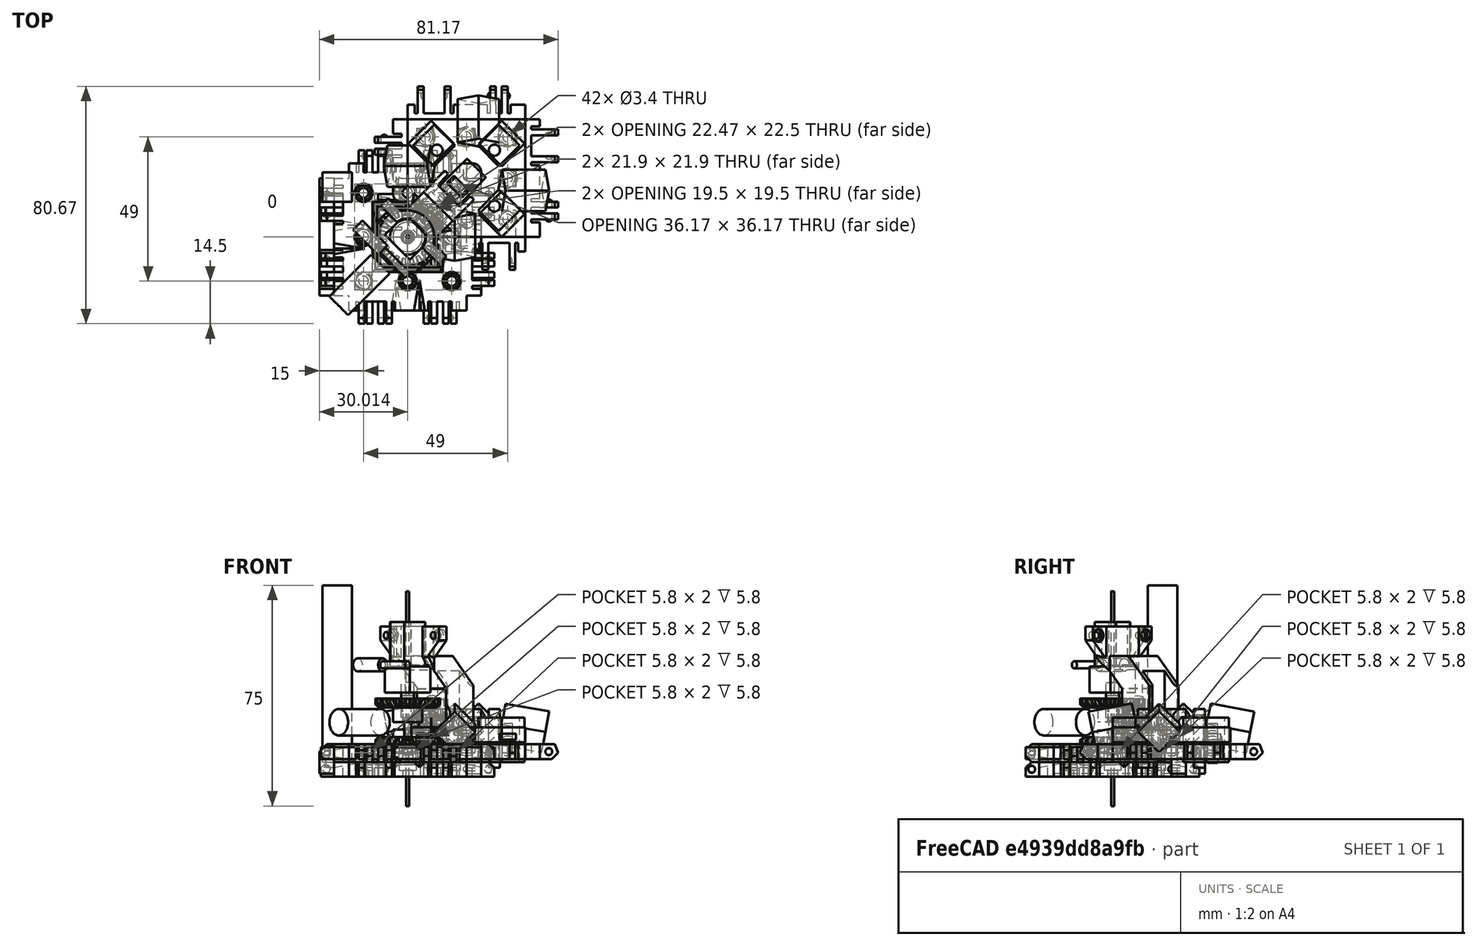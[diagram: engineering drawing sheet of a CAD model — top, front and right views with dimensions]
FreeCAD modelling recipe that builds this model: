
FCSTD DOCUMENT  (FreeCAD 0.18R16146 (Git))
Label: Robot 0.3
License: All rights reserved
LicenseURL: http://en.wikipedia.org/wiki/All_rights_reserved
objects: Part::Box×364, Part::Cut×148, Part::Sphere×107, Part::MultiFuse×99, Part::Cylinder×77, Part::Fuse×47, Part::Feature×40, Part::Chamfer×28, Drawing::FeatureViewAnnotation×12, Part::MultiCommon×5, Part::Fillet×5, App::DocumentObjectGroup×4, Part::FeaturePython×3, Part::Cone×2, Part::Mirroring×2, Drawing::FeaturePage×2
note: 927 computed .brp shape members not serialized (recipe doc carries the construction recipe); baked Part::Feature solids carry a one-line shape summary decoded from their .brp

FEATURE [Part::Box] Box  label="Cube"
  AttacherType = Attacher::AttachEngine3D
  Height = 5
  Length = 40
  Placement = pos=(-20,-20,-2) rot=(0,0,1;0rad)
  Width = 40
FEATURE [Part::Sphere] Sphere003  label="Mag Hole 3"
  Angle1 = -90
  Angle2 = 90
  Angle3 = 360
  AttacherType = Attacher::AttachEngine3D
  Placement = pos=(-15,15,1.7) rot=(0,0,1;0rad)
  Radius = 2.83
FEATURE [Part::Sphere] Sphere005  label="Mag Hole 2"
  Angle1 = -90
  Angle2 = 90
  Angle3 = 360
  AttacherType = Attacher::AttachEngine3D
  Placement = pos=(15,0,1.7) rot=(0,0,1;0rad)
  Radius = 2.825
FEATURE [Part::Sphere] Sphere  label="Mag Hole"
  Angle1 = -90
  Angle2 = 90
  Angle3 = 360
  AttacherType = Attacher::AttachEngine3D
  Placement = pos=(-15,-15,1.7) rot=(0,0,1;0rad)
  Radius = 2.83
FEATURE [Part::MultiFuse] Fusion004  label="Ball Holes"
  Shapes = -> [Sphere,Sphere005,Sphere003]
FEATURE [Part::Cut] Cut003
  Base = -> Box
  Tool = -> Fusion004
FEATURE [Part::Box] Box001  label="Cube001"
  AttacherType = Attacher::AttachEngine3D
  Height = 7
  Length = 5
  Placement = pos=(-5,0,-2) rot=(0,0,1;0rad)
  Width = 40
FEATURE [Part::Box] Box002  label="Cube002"
  AttacherType = Attacher::AttachEngine3D
  Height = 7
  Length = 10
  Placement = pos=(-15,6,-2) rot=(0,0,1;0rad)
  Width = 2
FEATURE [Part::Box] Box003  label="Cube003"
  AttacherType = Attacher::AttachEngine3D
  Height = 7
  Length = 10
  Placement = pos=(-15,10,-2) rot=(0,0,1;0rad)
  Width = 2
FEATURE [Part::Box] Box004  label="Cube004"
  AttacherType = Attacher::AttachEngine3D
  Height = 7
  Length = 10
  Placement = pos=(-15,25.4,-2) rot=(0,0,1;0rad)
  Width = 2
FEATURE [Part::Box] Box005  label="Cube005"
  AttacherType = Attacher::AttachEngine3D
  Height = 7
  Length = 10
  Placement = pos=(-15,34.6,-2) rot=(0,0,1;0rad)
  Width = 2
FEATURE [Part::Sphere] Sphere008
  Angle1 = -90
  Angle2 = 90
  Angle3 = 360
  AttacherType = Attacher::AttachEngine3D
  Placement = pos=(-7.5,6.5,0.5) rot=(0,0,1;0rad)
  Radius = 1.25
FEATURE [Part::Box] Box006  label="Chamfer Cube"
  AttacherType = Attacher::AttachEngine3D
  Height = 10
  Length = 13
  Placement = pos=(-11.69,0,-1.19) rot=(0,-1,0;0.785398rad)
  Width = 40
FEATURE [Part::Sphere] Sphere009
  Angle1 = -90
  Angle2 = 90
  Angle3 = 360
  AttacherType = Attacher::AttachEngine3D
  Placement = pos=(-7.5,11.5,0.5) rot=(0,0,1;0rad)
  Radius = 1.25
FEATURE [Part::Sphere] Sphere010
  Angle1 = -90
  Angle2 = 90
  Angle3 = 360
  AttacherType = Attacher::AttachEngine3D
  Placement = pos=(-7.5,28,0.5) rot=(0,0,1;0rad)
  Radius = 1.5
FEATURE [Part::Sphere] Sphere011
  Angle1 = -90
  Angle2 = 90
  Angle3 = 360
  AttacherType = Attacher::AttachEngine3D
  Placement = pos=(-7.5,34,0.5) rot=(0,0,1;0rad)
  Radius = 1.5
FEATURE [Part::Box] Box007  label="Cube007"
  AttacherType = Attacher::AttachEngine3D
  Height = 7
  Length = 4
  Placement = pos=(-6,5,-2) rot=(0,0,1;0rad)
  Width = 1
FEATURE [Part::Box] Box008  label="Cube008"
  AttacherType = Attacher::AttachEngine3D
  Height = 7
  Length = 4
  Placement = pos=(-6,8,-2) rot=(0,0,1;0rad)
  Width = 2
FEATURE [Part::Box] Box009  label="Cube009"
  AttacherType = Attacher::AttachEngine3D
  Height = 7
  Length = 4
  Placement = pos=(-6,12,-2) rot=(0,0,1;0rad)
  Width = 1
FEATURE [Part::Box] Box010  label="Cube010"
  AttacherType = Attacher::AttachEngine3D
  Height = 7
  Length = 4
  Placement = pos=(-6,24.4,-2) rot=(0,0,1;0rad)
  Width = 1
FEATURE [Part::Box] Box011  label="Cube011"
  AttacherType = Attacher::AttachEngine3D
  Height = 7
  Length = 4
  Placement = pos=(-6,36.6,-2) rot=(0,0,1;0rad)
  Width = 1
FEATURE [Part::Box] Box012  label="Cube012"
  AttacherType = Attacher::AttachEngine3D
  Height = 7
  Length = 4
  Placement = pos=(-6,27.4,-2) rot=(0,0,1;0rad)
  Width = 7.2
FEATURE [Part::MultiFuse] Fusion003  label="Extra Holes for Clips"
  Shapes = -> [Box012,Box009,Box011,Box008,Box010,Box007]
FEATURE [Part::Box] Box013  label="Re-level Edge Clip Block"
  AttacherType = Attacher::AttachEngine3D
  Height = 10
  Length = 20
  Placement = pos=(-19,-2,3) rot=(0,0,1;0rad)
  Width = 44
FEATURE [Part::Box] Box014  label="Cube014"
  AttacherType = Attacher::AttachEngine3D
  Height = 7
  Length = 10
  Placement = pos=(-10,34.6,0) rot=(0,0,1;0rad)
  Width = 2
FEATURE [Part::Box] Box015  label="Cube015"
  AttacherType = Attacher::AttachEngine3D
  Height = 7
  Length = 5
  Width = 40
FEATURE [Part::Box] Box016  label="Cube016"
  AttacherType = Attacher::AttachEngine3D
  Height = 7
  Length = 10
  Placement = pos=(-10,25.4,0) rot=(0,0,1;0rad)
  Width = 2
FEATURE [Part::Box] Box017  label="Cube017"
  AttacherType = Attacher::AttachEngine3D
  Height = 7
  Length = 10
  Placement = pos=(-10,10,0) rot=(0,0,1;0rad)
  Width = 2
FEATURE [Part::Box] Box018  label="Cube018"
  AttacherType = Attacher::AttachEngine3D
  Height = 7
  Length = 10
  Placement = pos=(-10,6,0) rot=(0,0,1;0rad)
  Width = 2
FEATURE [Part::Sphere] Sphere012
  Angle1 = -90
  Angle2 = 90
  Angle3 = 360
  AttacherType = Attacher::AttachEngine3D
  Placement = pos=(-3,6.5,2.5) rot=(0,0,1;0rad)
  Radius = 1.25
FEATURE [Part::Box] Box019  label="Cube019"
  AttacherType = Attacher::AttachEngine3D
  Height = 10
  Length = 13
  Placement = pos=(-10.19,0,-1.19) rot=(0,-1,0;0.785398rad)
  Width = 40
FEATURE [Part::Sphere] Sphere013
  Angle1 = -90
  Angle2 = 90
  Angle3 = 360
  AttacherType = Attacher::AttachEngine3D
  Placement = pos=(-3,11.5,2.5) rot=(0,0,1;0rad)
  Radius = 1.25
FEATURE [Part::Sphere] Sphere014
  Angle1 = -90
  Angle2 = 90
  Angle3 = 360
  AttacherType = Attacher::AttachEngine3D
  Placement = pos=(-3,28,2.5) rot=(0,0,1;0rad)
  Radius = 1.5
FEATURE [Part::Sphere] Sphere015
  Angle1 = -90
  Angle2 = 90
  Angle3 = 360
  AttacherType = Attacher::AttachEngine3D
  Placement = pos=(-3,34,2.5) rot=(0,0,1;0rad)
  Radius = 1.5
FEATURE [Part::MultiFuse] Fusion005
  Shapes = -> [Box015,Box018,Box017,Box016,Box014]
FEATURE [Part::Cut] Cut005
  Base = -> Fusion005
  Tool = -> Box019
FEATURE [Part::MultiFuse] Fusion006
  Shapes = -> [Sphere012,Sphere013,Cut005]
FEATURE [Part::MultiFuse] Fusion007
  Shapes = -> [Sphere015,Sphere014]
FEATURE [Part::Cut] Cut006
  Base = -> Fusion006
  Tool = -> Fusion007
FEATURE [Part::Chamfer] Chamfer002
  Base = -> Cut006
  Edges = 4 edges r=4: [Edge31,Edge37,Edge43,Edge46]
FEATURE [Part::Box] Box020  label="Cube020"
  AttacherType = Attacher::AttachEngine3D
  Height = 7
  Length = 4
  Placement = pos=(-1,5,0) rot=(0,0,1;0rad)
  Width = 1
FEATURE [Part::Box] Box021  label="Cube021"
  AttacherType = Attacher::AttachEngine3D
  Height = 7
  Length = 4
  Placement = pos=(-1,8,0) rot=(0,0,1;0rad)
  Width = 2
FEATURE [Part::Box] Box022  label="Cube022"
  AttacherType = Attacher::AttachEngine3D
  Height = 7
  Length = 4
  Placement = pos=(-1,12,0) rot=(0,0,1;0rad)
  Width = 1
FEATURE [Part::Box] Box023  label="Cube023"
  AttacherType = Attacher::AttachEngine3D
  Height = 7
  Length = 4
  Placement = pos=(-1,24.4,0) rot=(0,0,1;0rad)
  Width = 1
FEATURE [Part::Box] Box024  label="Cube024"
  AttacherType = Attacher::AttachEngine3D
  Height = 7
  Length = 4
  Placement = pos=(-1,36.6,0) rot=(0,0,1;0rad)
  Width = 1
FEATURE [Part::Box] Box025  label="Cube025"
  AttacherType = Attacher::AttachEngine3D
  Height = 7
  Length = 4
  Placement = pos=(-1,27.4,0) rot=(0,0,1;0rad)
  Width = 7.2
FEATURE [Part::MultiFuse] Fusion008
  Shapes = -> [Box025,Box022,Box024,Box021,Box023,Box020]
FEATURE [Part::Cut] Cut007
  Base = -> Chamfer002
  Placement = pos=(-5,40,3) rot=(1,0,0;3.14159rad)
  Tool = -> Fusion008
FEATURE [Part::Box] Box026  label="Cube026"
  AttacherType = Attacher::AttachEngine3D
  Height = 10
  Length = 12
  Placement = pos=(-11,-2,-12) rot=(0,0,1;0rad)
  Width = 44
FEATURE [Part::Cut] Cut008
  Base = -> Cut007
  Placement = pos=(40,0,0) rot=(0,0,1;1.5708rad)
  Tool = -> Box026
FEATURE [Part::Box] Box027  label="Cube027"
  AttacherType = Attacher::AttachEngine3D
  Height = 7
  Length = 4
  Placement = pos=(-1,12,0) rot=(0,0,1;0rad)
  Width = 1
FEATURE [Part::Box] Box028  label="Cube028"
  AttacherType = Attacher::AttachEngine3D
  Height = 10
  Length = 13
  Placement = pos=(-10.19,0,-1.19) rot=(0,-1,0;0.785398rad)
  Width = 40
FEATURE [Part::Box] Box029  label="Cube029"
  AttacherType = Attacher::AttachEngine3D
  Height = 7
  Length = 4
  Placement = pos=(-1,27.4,0) rot=(0,0,1;0rad)
  Width = 7.2
FEATURE [Part::Box] Box030  label="Cube030"
  AttacherType = Attacher::AttachEngine3D
  Height = 7
  Length = 4
  Placement = pos=(-1,5,0) rot=(0,0,1;0rad)
  Width = 1
FEATURE [Part::Box] Box031  label="Cube031"
  AttacherType = Attacher::AttachEngine3D
  Height = 7
  Length = 10
  Placement = pos=(-10,6,0) rot=(0,0,1;0rad)
  Width = 2
FEATURE [Part::Box] Box032  label="Cube032"
  AttacherType = Attacher::AttachEngine3D
  Height = 10
  Length = 12
  Placement = pos=(-11,-2,-12) rot=(0,0,1;0rad)
  Width = 44
FEATURE [Part::Sphere] Sphere016
  Angle1 = -90
  Angle2 = 90
  Angle3 = 360
  AttacherType = Attacher::AttachEngine3D
  Placement = pos=(-3,6.5,2.5) rot=(0,0,1;0rad)
  Radius = 1.25
FEATURE [Part::Box] Box033  label="Cube033"
  AttacherType = Attacher::AttachEngine3D
  Height = 7
  Length = 10
  Placement = pos=(-10,25.4,0) rot=(0,0,1;0rad)
  Width = 2
FEATURE [Part::Box] Box034  label="Cube034"
  AttacherType = Attacher::AttachEngine3D
  Height = 7
  Length = 10
  Placement = pos=(-10,10,0) rot=(0,0,1;0rad)
  Width = 2
FEATURE [Part::Sphere] Sphere017
  Angle1 = -90
  Angle2 = 90
  Angle3 = 360
  AttacherType = Attacher::AttachEngine3D
  Placement = pos=(-3,28,2.5) rot=(0,0,1;0rad)
  Radius = 1.5
FEATURE [Part::Sphere] Sphere018
  Angle1 = -90
  Angle2 = 90
  Angle3 = 360
  AttacherType = Attacher::AttachEngine3D
  Placement = pos=(-3,11.5,2.5) rot=(0,0,1;0rad)
  Radius = 1.25
FEATURE [Part::Box] Box035  label="Cube035"
  AttacherType = Attacher::AttachEngine3D
  Height = 7
  Length = 4
  Placement = pos=(-1,36.6,0) rot=(0,0,1;0rad)
  Width = 1
FEATURE [Part::Sphere] Sphere019
  Angle1 = -90
  Angle2 = 90
  Angle3 = 360
  AttacherType = Attacher::AttachEngine3D
  Placement = pos=(-3,34,2.5) rot=(0,0,1;0rad)
  Radius = 1.5
FEATURE [Part::MultiFuse] Fusion011
  Shapes = -> [Sphere019,Sphere017]
FEATURE [Part::Box] Box036  label="Cube036"
  AttacherType = Attacher::AttachEngine3D
  Height = 7
  Length = 4
  Placement = pos=(-1,8,0) rot=(0,0,1;0rad)
  Width = 2
FEATURE [Part::Box] Box037  label="Cube037"
  AttacherType = Attacher::AttachEngine3D
  Height = 7
  Length = 10
  Placement = pos=(-10,34.6,0) rot=(0,0,1;0rad)
  Width = 2
FEATURE [Part::Box] Box038  label="Cube038"
  AttacherType = Attacher::AttachEngine3D
  Height = 7
  Length = 4
  Placement = pos=(-1,24.4,0) rot=(0,0,1;0rad)
  Width = 1
FEATURE [Part::MultiFuse] Fusion009
  Shapes = -> [Box029,Box027,Box035,Box036,Box038,Box030]
FEATURE [Part::Box] Box039  label="Cube039"
  AttacherType = Attacher::AttachEngine3D
  Height = 7
  Length = 5
  Width = 40
FEATURE [Part::MultiFuse] Fusion012
  Shapes = -> [Box039,Box031,Box034,Box033,Box037]
FEATURE [Part::Cut] Cut011
  Base = -> Fusion012
  Tool = -> Box028
FEATURE [Part::MultiFuse] Fusion010
  Shapes = -> [Sphere016,Sphere018,Cut011]
FEATURE [Part::Cut] Cut012
  Base = -> Fusion010
  Tool = -> Fusion011
FEATURE [Part::Chamfer] Chamfer003
  Base = -> Cut012
  Edges = 4 edges r=4: [Edge31,Edge37,Edge43,Edge46]
FEATURE [Part::Cut] Cut010
  Base = -> Chamfer003
  Placement = pos=(-5,40,3) rot=(1,0,0;3.14159rad)
  Tool = -> Fusion009
FEATURE [Part::Cut] Cut009
  Base = -> Cut010
  Placement = pos=(40,40,0) rot=(0,0,1;3.14159rad)
  Tool = -> Box032
FEATURE [Part::Sphere] Sphere020
  Angle1 = -90
  Angle2 = 90
  Angle3 = 360
  AttacherType = Attacher::AttachEngine3D
  Placement = pos=(-3,11.5,2.5) rot=(0,0,1;0rad)
  Radius = 1.25
FEATURE [Part::Box] Box040  label="Cube040"
  AttacherType = Attacher::AttachEngine3D
  Height = 7
  Length = 10
  Placement = pos=(-10,6,0) rot=(0,0,1;0rad)
  Width = 2
FEATURE [Part::Box] Box041  label="Cube041"
  AttacherType = Attacher::AttachEngine3D
  Height = 7
  Length = 4
  Placement = pos=(-1,8,0) rot=(0,0,1;0rad)
  Width = 2
FEATURE [Part::Box] Box042  label="Cube042"
  AttacherType = Attacher::AttachEngine3D
  Height = 7
  Length = 10
  Placement = pos=(-10,10,0) rot=(0,0,1;0rad)
  Width = 2
FEATURE [Part::Box] Box043  label="Cube043"
  AttacherType = Attacher::AttachEngine3D
  Height = 10
  Length = 12
  Placement = pos=(-11,-2,-12) rot=(0,0,1;0rad)
  Width = 44
FEATURE [Part::Box] Box044  label="Cube044"
  AttacherType = Attacher::AttachEngine3D
  Height = 7
  Length = 4
  Placement = pos=(-1,5,0) rot=(0,0,1;0rad)
  Width = 1
FEATURE [Part::Sphere] Sphere021
  Angle1 = -90
  Angle2 = 90
  Angle3 = 360
  AttacherType = Attacher::AttachEngine3D
  Placement = pos=(-3,28,2.5) rot=(0,0,1;0rad)
  Radius = 1.5
FEATURE [Part::Sphere] Sphere022
  Angle1 = -90
  Angle2 = 90
  Angle3 = 360
  AttacherType = Attacher::AttachEngine3D
  Placement = pos=(-3,6.5,2.5) rot=(0,0,1;0rad)
  Radius = 1.25
FEATURE [Part::Sphere] Sphere023
  Angle1 = -90
  Angle2 = 90
  Angle3 = 360
  AttacherType = Attacher::AttachEngine3D
  Placement = pos=(-3,34,2.5) rot=(0,0,1;0rad)
  Radius = 1.5
FEATURE [Part::Box] Box045  label="Cube045"
  AttacherType = Attacher::AttachEngine3D
  Height = 7
  Length = 4
  Placement = pos=(-1,12,0) rot=(0,0,1;0rad)
  Width = 1
FEATURE [Part::Box] Box046  label="Cube046"
  AttacherType = Attacher::AttachEngine3D
  Height = 7
  Length = 5
  Width = 40
FEATURE [Part::Box] Box047  label="Cube047"
  AttacherType = Attacher::AttachEngine3D
  Height = 7
  Length = 4
  Placement = pos=(-1,36.6,0) rot=(0,0,1;0rad)
  Width = 1
FEATURE [Part::Box] Box048  label="Cube048"
  AttacherType = Attacher::AttachEngine3D
  Height = 7
  Length = 4
  Placement = pos=(-1,24.4,0) rot=(0,0,1;0rad)
  Width = 1
FEATURE [Part::Box] Box049  label="Cube049"
  AttacherType = Attacher::AttachEngine3D
  Height = 7
  Length = 10
  Placement = pos=(-10,25.4,0) rot=(0,0,1;0rad)
  Width = 2
FEATURE [Part::Box] Box050  label="Cube050"
  AttacherType = Attacher::AttachEngine3D
  Height = 10
  Length = 13
  Placement = pos=(-10.19,0,-1.19) rot=(0,-1,0;0.785398rad)
  Width = 40
FEATURE [Part::Box] Box051  label="Cube051"
  AttacherType = Attacher::AttachEngine3D
  Height = 7
  Length = 10
  Placement = pos=(-10,34.6,0) rot=(0,0,1;0rad)
  Width = 2
FEATURE [Part::MultiFuse] Fusion015
  Shapes = -> [Box046,Box040,Box042,Box049,Box051]
FEATURE [Part::Cut] Cut013
  Base = -> Fusion015
  Tool = -> Box050
FEATURE [Part::MultiFuse] Fusion013
  Shapes = -> [Sphere022,Sphere020,Cut013]
FEATURE [Part::MultiFuse] Fusion016
  Shapes = -> [Sphere023,Sphere021]
FEATURE [Part::Cut] Cut014
  Base = -> Fusion013
  Tool = -> Fusion016
FEATURE [Part::Chamfer] Chamfer004
  Base = -> Cut014
  Edges = 4 edges r=4: [Edge31,Edge37,Edge43,Edge46]
FEATURE [Part::Box] Box052  label="Cube052"
  AttacherType = Attacher::AttachEngine3D
  Height = 7
  Length = 4
  Placement = pos=(-1,27.4,0) rot=(0,0,1;0rad)
  Width = 7.2
FEATURE [Part::MultiFuse] Fusion014
  Shapes = -> [Box052,Box045,Box047,Box041,Box048,Box044]
FEATURE [Part::Cut] Cut016
  Base = -> Chamfer004
  Placement = pos=(-5,40,3) rot=(1,0,0;3.14159rad)
  Tool = -> Fusion014
FEATURE [Part::Cut] Cut015
  Base = -> Cut016
  Placement = pos=(0,40,0) rot=(0,0,-1;1.5708rad)
  Tool = -> Box043
FEATURE [Part::Box] Box054  label="Cube054"
  AttacherType = Attacher::AttachEngine3D
  Height = 15
  Length = 10
  Placement = pos=(9,2,-3) rot=(0,0,1;0.785398rad)
  Width = 10
FEATURE [Part::Box] Box055  label="Cube055"
  AttacherType = Attacher::AttachEngine3D
  Height = 15
  Length = 10
  Placement = pos=(31,24,-3) rot=(0,0,1;0.785398rad)
  Width = 10
FEATURE [Part::Box] Box056  label="Cube056"
  AttacherType = Attacher::AttachEngine3D
  Height = 15
  Length = 10
  Placement = pos=(31,2,-3) rot=(0,0,1;0.785398rad)
  Width = 10
FEATURE [Part::Box] Box057  label="Cube057"
  AttacherType = Attacher::AttachEngine3D
  Height = 15
  Length = 10
  Placement = pos=(9,24,-3) rot=(0,0,1;0.785398rad)
  Width = 10
FEATURE [Part::MultiFuse] Fusion017
  Shapes = -> [Box054,Box057,Box056,Box055]
FEATURE [Part::Box] Box058  label="Cube058"
  AttacherType = Attacher::AttachEngine3D
  Height = 5
  Length = 40
  Placement = pos=(0,0,3.7) rot=(0,0,1;0rad)
  Width = 40
FEATURE [Part::Box] Box059  label="Square Nut Hole 008"
  AttacherType = Attacher::AttachEngine3D
  Height = 2
  Length = 5.6
  Placement = pos=(17.2,31.2,4.6) rot=(0,0,1;0rad)
  Width = 5.6
FEATURE [Part::Box] Box060  label="Square Nut Hole 009"
  AttacherType = Attacher::AttachEngine3D
  Height = 2
  Length = 5.6
  Placement = pos=(17.2,-0.85,4.6) rot=(0,0,1;0rad)
  Width = 10
FEATURE [Part::Box] Box061  label="Square Nut Hole 010"
  AttacherType = Attacher::AttachEngine3D
  Height = 2
  Length = 5.6
  Placement = pos=(31.2,-0.85,4.6) rot=(0,0,1;0rad)
  Width = 10
FEATURE [Part::Box] Box062  label="Square Nut Hole 011"
  AttacherType = Attacher::AttachEngine3D
  Height = 2
  Length = 5.4
  Placement = pos=(31.3,17.3,4.6) rot=(0,0,1;0rad)
  Width = 5.4
FEATURE [Part::Box] Box063  label="Square Nut Hole 012"
  AttacherType = Attacher::AttachEngine3D
  Height = 2
  Length = 5.7
  Placement = pos=(3.15,31.15,4.6) rot=(0,0,1;0rad)
  Width = 5.7
FEATURE [Part::Box] Box064  label="Square Nut Hole 013"
  AttacherType = Attacher::AttachEngine3D
  Height = 2
  Length = 5.5
  Placement = pos=(31.25,31.25,4.6) rot=(0,0,1;0rad)
  Width = 5.5
FEATURE [Part::Box] Box065  label="Square Nut Hole 014"
  AttacherType = Attacher::AttachEngine3D
  Height = 2
  Length = 5.8
  Placement = pos=(3.1,17.1,4.6) rot=(0,0,1;0rad)
  Width = 5.8
FEATURE [Part::Box] Box066  label="Square Nut Hole 015"
  AttacherType = Attacher::AttachEngine3D
  Height = 2
  Length = 5.6
  Placement = pos=(3.2,-0.85,4.6) rot=(0,0,1;0rad)
  Width = 10
FEATURE [Part::Sphere] Sphere006  label="Nut Clearence1"
  Angle1 = -90
  Angle2 = 90
  Angle3 = 360
  AttacherType = Attacher::AttachEngine3D
  Placement = pos=(6,6,2.4) rot=(0,0,1;0rad)
  Radius = 3.35
FEATURE [Part::Sphere] Sphere024
  Angle1 = -90
  Angle2 = 90
  Angle3 = 360
  AttacherType = Attacher::AttachEngine3D
  Placement = pos=(6,34,2.4) rot=(0,0,1;0rad)
  Radius = 3.35
FEATURE [Part::Sphere] Sphere007
  Angle1 = -90
  Angle2 = 90
  Angle3 = 360
  AttacherType = Attacher::AttachEngine3D
  Placement = pos=(34,20,2.4) rot=(0,0,1;0rad)
  Radius = 3.35
FEATURE [Part::Sphere] Sphere001
  Angle1 = -90
  Angle2 = 90
  Angle3 = 360
  AttacherType = Attacher::AttachEngine3D
  Placement = pos=(34,6,2.4) rot=(0,0,1;0rad)
  Radius = 3.35
FEATURE [Part::Sphere] Sphere025
  Angle1 = -90
  Angle2 = 90
  Angle3 = 360
  AttacherType = Attacher::AttachEngine3D
  Placement = pos=(20,6,2.4) rot=(0,0,1;0rad)
  Radius = 3.35
FEATURE [Part::Sphere] Sphere026
  Angle1 = -90
  Angle2 = 90
  Angle3 = 360
  AttacherType = Attacher::AttachEngine3D
  Placement = pos=(20,34,2.4) rot=(0,0,1;0rad)
  Radius = 3.35
FEATURE [Part::Sphere] Sphere004
  Angle1 = -90
  Angle2 = 90
  Angle3 = 360
  AttacherType = Attacher::AttachEngine3D
  Placement = pos=(6,20,2.4) rot=(0,0,1;0rad)
  Radius = 3.35
FEATURE [Part::Sphere] Sphere002
  Angle1 = -90
  Angle2 = 90
  Angle3 = 360
  AttacherType = Attacher::AttachEngine3D
  Placement = pos=(34,34,2.4) rot=(0,0,1;0rad)
  Radius = 3.35
FEATURE [Part::Cylinder] Cylinder
  Angle = 360
  AttacherType = Attacher::AttachEngine3D
  Height = 10
  Placement = pos=(6,6,0) rot=(0,0,1;0rad)
  Radius = 1.7
FEATURE [Part::Cylinder] Cylinder002
  Angle = 360
  AttacherType = Attacher::AttachEngine3D
  Height = 10
  Placement = pos=(34,6,0) rot=(0,0,1;0rad)
  Radius = 1.7
FEATURE [Part::Cylinder] Cylinder001
  Angle = 360
  AttacherType = Attacher::AttachEngine3D
  Height = 10
  Placement = pos=(20,6,0) rot=(0,0,1;0rad)
  Radius = 1.7
FEATURE [Part::Cylinder] Cylinder003
  Angle = 360
  AttacherType = Attacher::AttachEngine3D
  Height = 10
  Placement = pos=(34,34,0) rot=(0,0,1;0rad)
  Radius = 1.7
FEATURE [Part::Cylinder] Cylinder004
  Angle = 360
  AttacherType = Attacher::AttachEngine3D
  Height = 10
  Placement = pos=(20,34,0) rot=(0,0,1;0rad)
  Radius = 1.7
FEATURE [Part::Cylinder] Cylinder005
  Angle = 360
  AttacherType = Attacher::AttachEngine3D
  Height = 10
  Placement = pos=(6,34,0) rot=(0,0,1;0rad)
  Radius = 1.7
FEATURE [Part::Cylinder] Cylinder006
  Angle = 360
  AttacherType = Attacher::AttachEngine3D
  Height = 10
  Placement = pos=(6,20,0) rot=(0,0,1;0rad)
  Radius = 1.7
FEATURE [Part::Cylinder] Cylinder007
  Angle = 360
  AttacherType = Attacher::AttachEngine3D
  Height = 10
  Placement = pos=(34,20,0) rot=(0,0,1;0rad)
  Radius = 1.7
FEATURE [Part::MultiFuse] Fusion018
  Shapes = -> [Cylinder,Cylinder004,Cylinder007,Cylinder005,Cylinder006,Cylinder001,Cylinder002,Cylinder003]
FEATURE [Part::MultiFuse] Fusion019
  Shapes = -> [Sphere007,Sphere024,Sphere006,Sphere025,Sphere001,Sphere026,Sphere004,Sphere002]
FEATURE [Part::MultiFuse] Fusion020
  Shapes = -> [Box061,Box065,Box062,Box063,Box064,Box066,Box059,Box060]
FEATURE [Part::Cut] Cut017
  Base = -> Box058
  Tool = -> Fusion020
FEATURE [Part::Cut] Cut019
  Base = -> Cut017
  Tool = -> Fusion019
FEATURE [Part::Cut] Cut018
  Base = -> Cut019
  Tool = -> Fusion018
FEATURE [Part::Cylinder] Cylinder008
  Angle = 360
  AttacherType = Attacher::AttachEngine3D
  Height = 20
  Placement = pos=(10,10.5,-5) rot=(0,0,1;0rad)
  Radius = 1.9
FEATURE [Part::Cylinder] Cylinder009
  Angle = 360
  AttacherType = Attacher::AttachEngine3D
  Height = 20
  Placement = pos=(29.5,10.5,-5) rot=(0,0,1;0rad)
  Radius = 1.9
FEATURE [Part::Cylinder] Cylinder010
  Angle = 360
  AttacherType = Attacher::AttachEngine3D
  Height = 20
  Placement = pos=(29.5,29.5,-5) rot=(0,0,1;0rad)
  Radius = 1.9
FEATURE [Part::Cylinder] Cylinder011
  Angle = 360
  AttacherType = Attacher::AttachEngine3D
  Height = 20
  Placement = pos=(10,29.5,-7) rot=(0,0,1;0rad)
  Radius = 1.9
FEATURE [Part::MultiFuse] Fusion021  label="M2 Screw holes"
  Shapes = -> [Cylinder008,Cylinder009,Cylinder011,Cylinder010]
FEATURE [Part::Box] Box067  label="Square Nut Hole 016"
  AttacherType = Attacher::AttachEngine3D
  Height = 2
  Length = 5.8
  Placement = pos=(31.1,17.1,4.6) rot=(0,0,1;0rad)
  Width = 5.8
FEATURE [Part::Box] Box068  label="Square Nut Hole 017"
  AttacherType = Attacher::AttachEngine3D
  Height = 2
  Length = 5.8
  Placement = pos=(17.1,36.9,2.1) rot=(1,0,0;3.14159rad)
  Width = 5.8
FEATURE [Part::Box] Box069  label="Square Nut Hole 018"
  AttacherType = Attacher::AttachEngine3D
  Height = 2
  Length = 5.8
  Placement = pos=(-2.9,2.9,2.1) rot=(1,0,0;3.14159rad)
  Width = 5.8
FEATURE [Part::Box] Box070  label="Square Nut Hole 019"
  AttacherType = Attacher::AttachEngine3D
  Height = 2
  Length = 5.8
  Placement = pos=(3.1,3.1,4.6) rot=(0,0,1;0rad)
  Width = 5.8
FEATURE [Part::Box] Box071  label="Square Nut Hole 020"
  AttacherType = Attacher::AttachEngine3D
  Height = 2
  Length = 5.8
  Placement = pos=(3.1,31.1,4.6) rot=(0,0,1;0rad)
  Width = 5.8
FEATURE [Part::Box] Box072  label="Square Nut Hole 021"
  AttacherType = Attacher::AttachEngine3D
  Height = 2
  Length = 5.8
  Placement = pos=(17.1,31.1,4.6) rot=(0,0,1;0rad)
  Width = 5.8
FEATURE [Part::Box] Box073  label="Square Nut Hole 022"
  AttacherType = Attacher::AttachEngine3D
  Height = 2
  Length = 5.8
  Placement = pos=(31.1,31.1,4.6) rot=(0,0,1;0rad)
  Width = 5.8
FEATURE [Part::Box] Box074  label="Square Nut Hole 023"
  AttacherType = Attacher::AttachEngine3D
  Height = 2
  Length = 5.8
  Placement = pos=(3.1,17.1,4.6) rot=(0,0,1;0rad)
  Width = 5.8
FEATURE [Part::Cylinder] Cylinder012
  Angle = 360
  AttacherType = Attacher::AttachEngine3D
  Height = 10
  Placement = pos=(6,6,0) rot=(0,0,1;0rad)
  Radius = 1.7
FEATURE [Part::Cylinder] Cylinder013
  Angle = 360
  AttacherType = Attacher::AttachEngine3D
  Height = 10
  Placement = pos=(34,34,0) rot=(0,0,1;0rad)
  Radius = 1.7
FEATURE [Part::Cylinder] Cylinder014
  Angle = 360
  AttacherType = Attacher::AttachEngine3D
  Height = 10
  Placement = pos=(20,34,0) rot=(0,0,1;0rad)
  Radius = 1.7
FEATURE [Part::Cylinder] Cylinder015
  Angle = 360
  AttacherType = Attacher::AttachEngine3D
  Height = 10
  Placement = pos=(6,34,0) rot=(0,0,1;0rad)
  Radius = 1.7
FEATURE [Part::Cylinder] Cylinder016
  Angle = 360
  AttacherType = Attacher::AttachEngine3D
  Height = 10
  Placement = pos=(6,20,0) rot=(0,0,1;0rad)
  Radius = 1.7
FEATURE [Part::Cylinder] Cylinder017
  Angle = 360
  AttacherType = Attacher::AttachEngine3D
  Height = 10
  Placement = pos=(34,20,0) rot=(0,0,1;0rad)
  Radius = 1.7
FEATURE [Part::Cylinder] Cylinder018
  Angle = 360
  AttacherType = Attacher::AttachEngine3D
  Height = 10
  Placement = pos=(0,0,6.7) rot=(1,0,0;3.14159rad)
  Radius = 1.7
FEATURE [Part::Cylinder] Cylinder019
  Angle = 360
  AttacherType = Attacher::AttachEngine3D
  Height = 10
  Placement = pos=(20,34,6.7) rot=(1,0,0;3.14159rad)
  Radius = 1.7
FEATURE [Part::Box] Box075  label="Cube059"
  AttacherType = Attacher::AttachEngine3D
  Height = 5
  Length = 40
  Placement = pos=(-20,-20,-2) rot=(0,0,1;0rad)
  Width = 40
FEATURE [Part::Sphere] Sphere027
  Angle1 = -90
  Angle2 = 90
  Angle3 = 360
  AttacherType = Attacher::AttachEngine3D
  Placement = pos=(34,20,2.4) rot=(0,0,1;0rad)
  Radius = 3.35
FEATURE [Part::Sphere] Sphere028  label="Nut Clearence002"
  Angle1 = -90
  Angle2 = 90
  Angle3 = 360
  AttacherType = Attacher::AttachEngine3D
  Placement = pos=(6,6,2.4) rot=(0,0,1;0rad)
  Radius = 3.35
FEATURE [Part::Sphere] Sphere029
  Angle1 = -90
  Angle2 = 90
  Angle3 = 360
  AttacherType = Attacher::AttachEngine3D
  Placement = pos=(34,34,2.4) rot=(0,0,1;0rad)
  Radius = 3.35
FEATURE [Part::Sphere] Sphere030
  Angle1 = -90
  Angle2 = 90
  Angle3 = 360
  AttacherType = Attacher::AttachEngine3D
  Placement = pos=(0,0,4.3) rot=(1,0,0;3.14159rad)
  Radius = 3.35
FEATURE [Part::Sphere] Sphere031
  Angle1 = -90
  Angle2 = 90
  Angle3 = 360
  AttacherType = Attacher::AttachEngine3D
  Placement = pos=(20,34,4.3) rot=(1,0,0;3.14159rad)
  Radius = 3.35
FEATURE [Part::Sphere] Sphere032
  Angle1 = -90
  Angle2 = 90
  Angle3 = 360
  AttacherType = Attacher::AttachEngine3D
  Placement = pos=(6,34,2.4) rot=(0,0,1;0rad)
  Radius = 3.35
FEATURE [Part::Sphere] Sphere033
  Angle1 = -90
  Angle2 = 90
  Angle3 = 360
  AttacherType = Attacher::AttachEngine3D
  Placement = pos=(6,20,2.4) rot=(0,0,1;0rad)
  Radius = 3.35
FEATURE [Part::Sphere] Sphere034
  Angle1 = -90
  Angle2 = 90
  Angle3 = 360
  AttacherType = Attacher::AttachEngine3D
  Placement = pos=(20,34,2.4) rot=(0,0,1;0rad)
  Radius = 3.35
FEATURE [Part::Box] Box076  label="Cube060"
  AttacherType = Attacher::AttachEngine3D
  Height = 15
  Length = 19.5
  Placement = pos=(-9.75,-9.75,-3) rot=(0,0,1;0rad)
  Width = 19.5
FEATURE [Part::Box] Box077  label="Cube061"
  AttacherType = Attacher::AttachEngine3D
  Height = 15
  Length = 11
  Placement = pos=(8,24,-3) rot=(0,0,1;0.785398rad)
  Width = 11
FEATURE [Part::Box] Box078  label="Cube062"
  AttacherType = Attacher::AttachEngine3D
  Height = 15
  Length = 11
  Placement = pos=(8,0,-3) rot=(0,0,1;0.785398rad)
  Width = 11
FEATURE [Part::Box] Box079  label="Cube063"
  AttacherType = Attacher::AttachEngine3D
  Height = 15
  Length = 11
  Placement = pos=(32,0,-3) rot=(0,0,1;0.785398rad)
  Width = 11
FEATURE [Part::Box] Box080  label="Cube064"
  AttacherType = Attacher::AttachEngine3D
  Height = 15
  Length = 11
  Placement = pos=(32,24,-3) rot=(0,0,1;0.785398rad)
  Width = 11
FEATURE [Part::MultiFuse] Fusion022
  Shapes = -> [Box078,Box077,Box079,Box080]
FEATURE [Part::Cylinder] Cylinder020
  Angle = 360
  AttacherType = Attacher::AttachEngine3D
  Height = 20
  Placement = pos=(29.5,10.5,-5) rot=(0,0,1;0rad)
  Radius = 1.9
FEATURE [Part::Cylinder] Cylinder021
  Angle = 360
  AttacherType = Attacher::AttachEngine3D
  Height = 20
  Placement = pos=(10,29.5,-7) rot=(0,0,1;0rad)
  Radius = 1.9
FEATURE [Part::Cylinder] Cylinder022
  Angle = 360
  AttacherType = Attacher::AttachEngine3D
  Height = 20
  Placement = pos=(10,10.5,-5) rot=(0,0,1;0rad)
  Radius = 1.9
FEATURE [Part::Cylinder] Cylinder023
  Angle = 360
  AttacherType = Attacher::AttachEngine3D
  Height = 20
  Placement = pos=(29.5,29.5,-5) rot=(0,0,1;0rad)
  Radius = 1.9
FEATURE [Part::MultiFuse] Fusion023  label="M2 Screw holes001"
  Shapes = -> [Cylinder022,Cylinder020,Cylinder021,Cylinder023]
FEATURE [App::DocumentObjectGroup] Group  label="Cubes"
  Group = -> [Fusion017,Fusion022]
FEATURE [Part::Box] Box083  label="Cube067"
  AttacherType = Attacher::AttachEngine3D
  Height = 10
  Length = 24
  Placement = pos=(-12,-12,2.1) rot=(0,0,1;0rad)
  Width = 24
FEATURE [Part::Box] Box084  label="Cube068"
  AttacherType = Attacher::AttachEngine3D
  Height = 14
  Length = 20
  Placement = pos=(-10,-10,0) rot=(0,0,1;0rad)
  Width = 20
FEATURE [Part::Cut] Cut020
  Base = -> Box083
  Tool = -> Box084
FEATURE [Part::Chamfer] Chamfer007  label="Glue Channel Ball"
  Base = -> Cut020
  Edges = 8 edges r=0.95: [Edge4,Edge5,Edge14,Edge16,Edge17,Edge18,Edge19,Edge20]
FEATURE [Part::Chamfer] Chamfer008  label="Octogon Ball"
  Base = -> Box076
  Edges = 4 edges r=4: [Edge1,Edge3,Edge5,Edge7]
FEATURE [Part::Box] Box085  label="Cube069"
  AttacherType = Attacher::AttachEngine3D
  Height = 15
  Length = 19.5
  Placement = pos=(-9.75,-9.75,-14) rot=(0,0,1;0rad)
  Width = 19.5
FEATURE [Part::Box] Box086  label="Cube070"
  AttacherType = Attacher::AttachEngine3D
  Height = 10
  Length = 10
  Placement = pos=(4,-26,1) rot=(0.205904,-0.974848,-0.085288;0.803573rad)
  Width = 15
FEATURE [Part::Box] Box089  label="Cube073"
  AttacherType = Attacher::AttachEngine3D
  Height = 10
  Length = 10
  Placement = pos=(17,32.0919,9.95) rot=(-0.225436,0.969773,-0.093378;0.807337rad)
  Width = 15
FEATURE [Part::Box] Box090  label="Cube074"
  AttacherType = Attacher::AttachEngine3D
  Height = 10
  Length = 15
  Placement = pos=(30.8481,15.8,2.86019) rot=(0.974848,0.205904,-0.085288;0.803573rad)
  Width = 10
FEATURE [Part::Box] Box091  label="Cube075"
  AttacherType = Attacher::AttachEngine3D
  Height = 10
  Length = 10
  Placement = pos=(7.9081,17,9.95) rot=(-0.450607,0.280623,0.847469;1.65638rad)
  Width = 15
FEATURE [Part::Box] Box092  label="Cube076"
  AttacherType = Attacher::AttachEngine3D
  Height = 10
  Length = 10
  Placement = pos=(23,7.9081,9.95) rot=(-0.381178,-0.08861,0.920245;3.06822rad)
  Width = 15
FEATURE [Part::Box] Box093  label="Cube077"
  AttacherType = Attacher::AttachEngine3D
  Height = 7
  Length = 5
  Width = 40
FEATURE [Part::Box] Box094  label="Cube078"
  AttacherType = Attacher::AttachEngine3D
  Height = 7
  Length = 10
  Placement = pos=(-10,6,0) rot=(0,0,1;0rad)
  Width = 2
FEATURE [Part::Box] Box095  label="Cube079"
  AttacherType = Attacher::AttachEngine3D
  Height = 7
  Length = 10
  Placement = pos=(-10,10,0) rot=(0,0,1;0rad)
  Width = 2
FEATURE [Part::Box] Box096  label="Cube080"
  AttacherType = Attacher::AttachEngine3D
  Height = 7
  Length = 10
  Placement = pos=(-10,25.4,0) rot=(0,0,1;0rad)
  Width = 2
FEATURE [Part::Box] Box097  label="Cube081"
  AttacherType = Attacher::AttachEngine3D
  Height = 7
  Length = 10
  Placement = pos=(-10,34.6,0) rot=(0,0,1;0rad)
  Width = 2
FEATURE [Part::Sphere] Sphere035
  Angle1 = -90
  Angle2 = 90
  Angle3 = 360
  AttacherType = Attacher::AttachEngine3D
  Placement = pos=(-3,6.5,2.5) rot=(0,0,1;0rad)
  Radius = 1.25
FEATURE [Part::Box] Box098  label="Cube082"
  AttacherType = Attacher::AttachEngine3D
  Height = 10
  Length = 13
  Placement = pos=(-10.19,0,-1.19) rot=(0,-1,0;0.785398rad)
  Width = 40
FEATURE [Part::Sphere] Sphere036
  Angle1 = -90
  Angle2 = 90
  Angle3 = 360
  AttacherType = Attacher::AttachEngine3D
  Placement = pos=(-3,11.5,2.5) rot=(0,0,1;0rad)
  Radius = 1.25
FEATURE [Part::Sphere] Sphere037
  Angle1 = -90
  Angle2 = 90
  Angle3 = 360
  AttacherType = Attacher::AttachEngine3D
  Placement = pos=(-3,28,2.5) rot=(0,0,1;0rad)
  Radius = 1.5
FEATURE [Part::Sphere] Sphere038
  Angle1 = -90
  Angle2 = 90
  Angle3 = 360
  AttacherType = Attacher::AttachEngine3D
  Placement = pos=(-3,34,2.5) rot=(0,0,1;0rad)
  Radius = 1.5
FEATURE [Part::MultiFuse] Fusion030
  Shapes = -> [Box093,Box094,Box095,Box096,Box097]
FEATURE [Part::Cut] Cut025
  Base = -> Fusion030
  Tool = -> Box098
FEATURE [Part::MultiFuse] Fusion031
  Shapes = -> [Sphere035,Sphere036,Cut025]
FEATURE [Part::MultiFuse] Fusion032
  Shapes = -> [Sphere038,Sphere037]
FEATURE [Part::Cut] Cut026
  Base = -> Fusion031
  Tool = -> Fusion032
FEATURE [Part::Chamfer] Chamfer009
  Base = -> Cut026
  Edges = 4 edges r=4: [Edge31,Edge37,Edge43,Edge46]
FEATURE [Part::Box] Box099  label="Cube083"
  AttacherType = Attacher::AttachEngine3D
  Height = 7
  Length = 4
  Placement = pos=(-1,5,0) rot=(0,0,1;0rad)
  Width = 1
FEATURE [Part::Box] Box100  label="Cube084"
  AttacherType = Attacher::AttachEngine3D
  Height = 7
  Length = 4
  Placement = pos=(-1,8,0) rot=(0,0,1;0rad)
  Width = 2
FEATURE [Part::Box] Box101  label="Cube085"
  AttacherType = Attacher::AttachEngine3D
  Height = 7
  Length = 4
  Placement = pos=(-1,12,0) rot=(0,0,1;0rad)
  Width = 1
FEATURE [Part::Box] Box102  label="Cube086"
  AttacherType = Attacher::AttachEngine3D
  Height = 7
  Length = 4
  Placement = pos=(-1,24.4,0) rot=(0,0,1;0rad)
  Width = 1
FEATURE [Part::Box] Box103  label="Cube087"
  AttacherType = Attacher::AttachEngine3D
  Height = 7
  Length = 4
  Placement = pos=(-1,36.6,0) rot=(0,0,1;0rad)
  Width = 1
FEATURE [Part::Box] Box104  label="Cube088"
  AttacherType = Attacher::AttachEngine3D
  Height = 7
  Length = 4
  Placement = pos=(-1,27.4,0) rot=(0,0,1;0rad)
  Width = 7.2
FEATURE [Part::MultiFuse] Fusion033
  Shapes = -> [Box104,Box101,Box103,Box100,Box102,Box099]
FEATURE [Part::Cut] Cut027
  Base = -> Chamfer009
  Placement = pos=(-5,40,3) rot=(1,0,0;3.14159rad)
  Tool = -> Fusion033
FEATURE [Part::Box] Box105  label="Cube089"
  AttacherType = Attacher::AttachEngine3D
  Height = 10
  Length = 12
  Placement = pos=(-11,-2,-12) rot=(0,0,1;0rad)
  Width = 44
FEATURE [Part::Cut] Cut028
  Base = -> Cut027
  Tool = -> Box105
FEATURE [Part::Box] Box106  label="Cube090"
  AttacherType = Attacher::AttachEngine3D
  Height = 7
  Length = 10
  Placement = pos=(-10,34.6,0) rot=(0,0,1;0rad)
  Width = 2
FEATURE [Part::Box] Box107  label="Cube091"
  AttacherType = Attacher::AttachEngine3D
  Height = 7
  Length = 5
  Width = 40
FEATURE [Part::Box] Box108  label="Cube092"
  AttacherType = Attacher::AttachEngine3D
  Height = 7
  Length = 10
  Placement = pos=(-10,25.4,0) rot=(0,0,1;0rad)
  Width = 2
FEATURE [Part::Box] Box109  label="Cube093"
  AttacherType = Attacher::AttachEngine3D
  Height = 7
  Length = 10
  Placement = pos=(-10,10,0) rot=(0,0,1;0rad)
  Width = 2
FEATURE [Part::Box] Box110  label="Cube094"
  AttacherType = Attacher::AttachEngine3D
  Height = 7
  Length = 10
  Placement = pos=(-10,6,0) rot=(0,0,1;0rad)
  Width = 2
FEATURE [Part::Sphere] Sphere039
  Angle1 = -90
  Angle2 = 90
  Angle3 = 360
  AttacherType = Attacher::AttachEngine3D
  Placement = pos=(-3,6.5,2.5) rot=(0,0,1;0rad)
  Radius = 1.25
FEATURE [Part::Box] Box111  label="Cube095"
  AttacherType = Attacher::AttachEngine3D
  Height = 10
  Length = 13
  Placement = pos=(-10.19,0,-1.19) rot=(0,-1,0;0.785398rad)
  Width = 40
FEATURE [Part::Sphere] Sphere040
  Angle1 = -90
  Angle2 = 90
  Angle3 = 360
  AttacherType = Attacher::AttachEngine3D
  Placement = pos=(-3,11.5,2.5) rot=(0,0,1;0rad)
  Radius = 1.25
FEATURE [Part::Sphere] Sphere041
  Angle1 = -90
  Angle2 = 90
  Angle3 = 360
  AttacherType = Attacher::AttachEngine3D
  Placement = pos=(-3,28,2.5) rot=(0,0,1;0rad)
  Radius = 1.5
FEATURE [Part::Sphere] Sphere042
  Angle1 = -90
  Angle2 = 90
  Angle3 = 360
  AttacherType = Attacher::AttachEngine3D
  Placement = pos=(-3,34,2.5) rot=(0,0,1;0rad)
  Radius = 1.5
FEATURE [Part::MultiFuse] Fusion034
  Shapes = -> [Box107,Box110,Box109,Box108,Box106]
FEATURE [Part::Cut] Cut029
  Base = -> Fusion034
  Tool = -> Box111
FEATURE [Part::MultiFuse] Fusion035
  Shapes = -> [Sphere039,Sphere040,Cut029]
FEATURE [Part::MultiFuse] Fusion036
  Shapes = -> [Sphere042,Sphere041]
FEATURE [Part::Cut] Cut030
  Base = -> Fusion035
  Tool = -> Fusion036
FEATURE [Part::Chamfer] Chamfer010
  Base = -> Cut030
  Edges = 4 edges r=4: [Edge31,Edge37,Edge43,Edge46]
FEATURE [Part::Box] Box112  label="Cube096"
  AttacherType = Attacher::AttachEngine3D
  Height = 7
  Length = 4
  Placement = pos=(-1,5,0) rot=(0,0,1;0rad)
  Width = 1
FEATURE [Part::Box] Box113  label="Cube097"
  AttacherType = Attacher::AttachEngine3D
  Height = 7
  Length = 4
  Placement = pos=(-1,8,0) rot=(0,0,1;0rad)
  Width = 2
FEATURE [Part::Box] Box114  label="Cube098"
  AttacherType = Attacher::AttachEngine3D
  Height = 7
  Length = 4
  Placement = pos=(-1,12,0) rot=(0,0,1;0rad)
  Width = 1
FEATURE [Part::Box] Box115  label="Cube099"
  AttacherType = Attacher::AttachEngine3D
  Height = 7
  Length = 4
  Placement = pos=(-1,24.4,0) rot=(0,0,1;0rad)
  Width = 1
FEATURE [Part::Box] Box116  label="Cube100"
  AttacherType = Attacher::AttachEngine3D
  Height = 7
  Length = 4
  Placement = pos=(-1,36.6,0) rot=(0,0,1;0rad)
  Width = 1
FEATURE [Part::Box] Box117  label="Cube101"
  AttacherType = Attacher::AttachEngine3D
  Height = 7
  Length = 4
  Placement = pos=(-1,27.4,0) rot=(0,0,1;0rad)
  Width = 7.2
FEATURE [Part::MultiFuse] Fusion037
  Shapes = -> [Box117,Box114,Box116,Box113,Box115,Box112]
FEATURE [Part::Cut] Cut031
  Base = -> Chamfer010
  Placement = pos=(-5,40,3) rot=(1,0,0;3.14159rad)
  Tool = -> Fusion037
FEATURE [Part::Box] Box118  label="Cube102"
  AttacherType = Attacher::AttachEngine3D
  Height = 10
  Length = 12
  Placement = pos=(-11,-2,-12) rot=(0,0,1;0rad)
  Width = 44
FEATURE [Part::Cut] Cut032
  Base = -> Cut031
  Placement = pos=(40,0,0) rot=(0,0,1;1.5708rad)
  Tool = -> Box118
FEATURE [Part::Box] Box119  label="Cube103"
  AttacherType = Attacher::AttachEngine3D
  Height = 7
  Length = 4
  Placement = pos=(-1,12,0) rot=(0,0,1;0rad)
  Width = 1
FEATURE [Part::Box] Box120  label="Cube104"
  AttacherType = Attacher::AttachEngine3D
  Height = 10
  Length = 13
  Placement = pos=(-10.19,0,-1.19) rot=(0,-1,0;0.785398rad)
  Width = 40
FEATURE [Part::Box] Box121  label="Cube105"
  AttacherType = Attacher::AttachEngine3D
  Height = 7
  Length = 4
  Placement = pos=(-1,27.4,0) rot=(0,0,1;0rad)
  Width = 7.2
FEATURE [Part::Box] Box122  label="Cube106"
  AttacherType = Attacher::AttachEngine3D
  Height = 7
  Length = 4
  Placement = pos=(-1,5,0) rot=(0,0,1;0rad)
  Width = 1
FEATURE [Part::Box] Box123  label="Cube107"
  AttacherType = Attacher::AttachEngine3D
  Height = 7
  Length = 10
  Placement = pos=(-10,6,0) rot=(0,0,1;0rad)
  Width = 2
FEATURE [Part::Box] Box124  label="Cube108"
  AttacherType = Attacher::AttachEngine3D
  Height = 10
  Length = 12
  Placement = pos=(-11,-2,-12) rot=(0,0,1;0rad)
  Width = 44
FEATURE [Part::Sphere] Sphere043
  Angle1 = -90
  Angle2 = 90
  Angle3 = 360
  AttacherType = Attacher::AttachEngine3D
  Placement = pos=(-3,6.5,2.5) rot=(0,0,1;0rad)
  Radius = 1.25
FEATURE [Part::Box] Box125  label="Cube109"
  AttacherType = Attacher::AttachEngine3D
  Height = 7
  Length = 10
  Placement = pos=(-10,25.4,0) rot=(0,0,1;0rad)
  Width = 2
FEATURE [Part::Box] Box126  label="Cube110"
  AttacherType = Attacher::AttachEngine3D
  Height = 7
  Length = 10
  Placement = pos=(-10,10,0) rot=(0,0,1;0rad)
  Width = 2
FEATURE [Part::Sphere] Sphere044
  Angle1 = -90
  Angle2 = 90
  Angle3 = 360
  AttacherType = Attacher::AttachEngine3D
  Placement = pos=(-3,28,2.5) rot=(0,0,1;0rad)
  Radius = 1.5
FEATURE [Part::Sphere] Sphere045
  Angle1 = -90
  Angle2 = 90
  Angle3 = 360
  AttacherType = Attacher::AttachEngine3D
  Placement = pos=(-3,11.5,2.5) rot=(0,0,1;0rad)
  Radius = 1.25
FEATURE [Part::Box] Box127  label="Cube111"
  AttacherType = Attacher::AttachEngine3D
  Height = 7
  Length = 4
  Placement = pos=(-1,36.6,0) rot=(0,0,1;0rad)
  Width = 1
FEATURE [Part::Sphere] Sphere046
  Angle1 = -90
  Angle2 = 90
  Angle3 = 360
  AttacherType = Attacher::AttachEngine3D
  Placement = pos=(-3,34,2.5) rot=(0,0,1;0rad)
  Radius = 1.5
FEATURE [Part::MultiFuse] Fusion040
  Shapes = -> [Sphere046,Sphere044]
FEATURE [Part::Box] Box128  label="Cube112"
  AttacherType = Attacher::AttachEngine3D
  Height = 7
  Length = 4
  Placement = pos=(-1,8,0) rot=(0,0,1;0rad)
  Width = 2
FEATURE [Part::Box] Box129  label="Cube113"
  AttacherType = Attacher::AttachEngine3D
  Height = 7
  Length = 10
  Placement = pos=(-10,34.6,0) rot=(0,0,1;0rad)
  Width = 2
FEATURE [Part::Box] Box130  label="Cube114"
  AttacherType = Attacher::AttachEngine3D
  Height = 7
  Length = 4
  Placement = pos=(-1,24.4,0) rot=(0,0,1;0rad)
  Width = 1
FEATURE [Part::MultiFuse] Fusion038
  Shapes = -> [Box121,Box119,Box127,Box128,Box130,Box122]
FEATURE [Part::Box] Box131  label="Cube115"
  AttacherType = Attacher::AttachEngine3D
  Height = 7
  Length = 5
  Width = 40
FEATURE [Part::MultiFuse] Fusion041
  Shapes = -> [Box131,Box123,Box126,Box125,Box129]
FEATURE [Part::Cut] Cut035
  Base = -> Fusion041
  Tool = -> Box120
FEATURE [Part::MultiFuse] Fusion039
  Shapes = -> [Sphere043,Sphere045,Cut035]
FEATURE [Part::Cut] Cut036
  Base = -> Fusion039
  Tool = -> Fusion040
FEATURE [Part::Chamfer] Chamfer011
  Base = -> Cut036
  Edges = 4 edges r=4: [Edge31,Edge37,Edge43,Edge46]
FEATURE [Part::Cut] Cut034
  Base = -> Chamfer011
  Placement = pos=(-5,40,3) rot=(1,0,0;3.14159rad)
  Tool = -> Fusion038
FEATURE [Part::Cut] Cut033
  Base = -> Cut034
  Placement = pos=(40,40,0) rot=(0,0,1;3.14159rad)
  Tool = -> Box124
FEATURE [Part::Sphere] Sphere047
  Angle1 = -90
  Angle2 = 90
  Angle3 = 360
  AttacherType = Attacher::AttachEngine3D
  Placement = pos=(-3,11.5,2.5) rot=(0,0,1;0rad)
  Radius = 1.25
FEATURE [Part::Box] Box132  label="Cube116"
  AttacherType = Attacher::AttachEngine3D
  Height = 7
  Length = 10
  Placement = pos=(-10,6,0) rot=(0,0,1;0rad)
  Width = 2
FEATURE [Part::Box] Box133  label="Cube117"
  AttacherType = Attacher::AttachEngine3D
  Height = 7
  Length = 4
  Placement = pos=(-1,8,0) rot=(0,0,1;0rad)
  Width = 2
FEATURE [Part::Box] Box134  label="Cube118"
  AttacherType = Attacher::AttachEngine3D
  Height = 7
  Length = 10
  Placement = pos=(-10,10,0) rot=(0,0,1;0rad)
  Width = 2
FEATURE [Part::Box] Box135  label="Cube119"
  AttacherType = Attacher::AttachEngine3D
  Height = 10
  Length = 12
  Placement = pos=(-11,-2,-12) rot=(0,0,1;0rad)
  Width = 44
FEATURE [Part::Box] Box136  label="Cube120"
  AttacherType = Attacher::AttachEngine3D
  Height = 7
  Length = 4
  Placement = pos=(-1,5,0) rot=(0,0,1;0rad)
  Width = 1
FEATURE [Part::Sphere] Sphere048
  Angle1 = -90
  Angle2 = 90
  Angle3 = 360
  AttacherType = Attacher::AttachEngine3D
  Placement = pos=(-3,28,2.5) rot=(0,0,1;0rad)
  Radius = 1.5
FEATURE [Part::Sphere] Sphere049
  Angle1 = -90
  Angle2 = 90
  Angle3 = 360
  AttacherType = Attacher::AttachEngine3D
  Placement = pos=(-3,6.5,2.5) rot=(0,0,1;0rad)
  Radius = 1.25
FEATURE [Part::Sphere] Sphere050
  Angle1 = -90
  Angle2 = 90
  Angle3 = 360
  AttacherType = Attacher::AttachEngine3D
  Placement = pos=(-3,34,2.5) rot=(0,0,1;0rad)
  Radius = 1.5
FEATURE [Part::Box] Box137  label="Cube121"
  AttacherType = Attacher::AttachEngine3D
  Height = 7
  Length = 4
  Placement = pos=(-1,12,0) rot=(0,0,1;0rad)
  Width = 1
FEATURE [Part::Box] Box138  label="Cube122"
  AttacherType = Attacher::AttachEngine3D
  Height = 7
  Length = 5
  Width = 40
FEATURE [Part::Box] Box139  label="Cube123"
  AttacherType = Attacher::AttachEngine3D
  Height = 7
  Length = 4
  Placement = pos=(-1,36.6,0) rot=(0,0,1;0rad)
  Width = 1
FEATURE [Part::Box] Box140  label="Cube124"
  AttacherType = Attacher::AttachEngine3D
  Height = 7
  Length = 4
  Placement = pos=(-1,24.4,0) rot=(0,0,1;0rad)
  Width = 1
FEATURE [Part::Box] Box141  label="Cube125"
  AttacherType = Attacher::AttachEngine3D
  Height = 7
  Length = 10
  Placement = pos=(-10,25.4,0) rot=(0,0,1;0rad)
  Width = 2
FEATURE [Part::Box] Box142  label="Cube126"
  AttacherType = Attacher::AttachEngine3D
  Height = 10
  Length = 13
  Placement = pos=(-10.19,0,-1.19) rot=(0,-1,0;0.785398rad)
  Width = 40
FEATURE [Part::Box] Box143  label="Cube127"
  AttacherType = Attacher::AttachEngine3D
  Height = 7
  Length = 10
  Placement = pos=(-10,34.6,0) rot=(0,0,1;0rad)
  Width = 2
FEATURE [Part::MultiFuse] Fusion044
  Shapes = -> [Box138,Box132,Box134,Box141,Box143]
FEATURE [Part::Cut] Cut037
  Base = -> Fusion044
  Tool = -> Box142
FEATURE [Part::MultiFuse] Fusion042
  Shapes = -> [Sphere049,Sphere047,Cut037]
FEATURE [Part::MultiFuse] Fusion045
  Shapes = -> [Sphere050,Sphere048]
FEATURE [Part::Cut] Cut038
  Base = -> Fusion042
  Tool = -> Fusion045
FEATURE [Part::Chamfer] Chamfer012
  Base = -> Cut038
  Edges = 4 edges r=4: [Edge31,Edge37,Edge43,Edge46]
FEATURE [Part::Box] Box144  label="Cube128"
  AttacherType = Attacher::AttachEngine3D
  Height = 7
  Length = 4
  Placement = pos=(-1,27.4,0) rot=(0,0,1;0rad)
  Width = 7.2
FEATURE [Part::MultiFuse] Fusion043
  Shapes = -> [Box144,Box137,Box139,Box133,Box140,Box136]
FEATURE [Part::Cut] Cut040
  Base = -> Chamfer012
  Placement = pos=(-5,40,3) rot=(1,0,0;3.14159rad)
  Tool = -> Fusion043
FEATURE [Part::Cut] Cut039
  Base = -> Cut040
  Placement = pos=(0,40,0) rot=(0,0,-1;1.5708rad)
  Tool = -> Box135
FEATURE [Part::MultiFuse] Fusion048
  Shapes = -> [Box089,Box091,Box090,Box092]
FEATURE [Part::Box] Box145  label="Cube129"
  AttacherType = Attacher::AttachEngine3D
  Height = 15
  Length = 19.5
  Placement = pos=(-9.75,-9.75,-14) rot=(0,0,1;0rad)
  Width = 19.5
FEATURE [Part::Box] Box146  label="Cube130"
  AttacherType = Attacher::AttachEngine3D
  Height = 15
  Length = 19.5
  Placement = pos=(-9.75,-9.75,-3) rot=(0,0,1;0rad)
  Width = 19.5
FEATURE [Part::Chamfer] Chamfer013  label="Octagon"
  Base = -> Box146
  Edges = 4 edges r=4: [Edge1,Edge3,Edge5,Edge7]
FEATURE [Part::Box] Box147  label="Cube131"
  AttacherType = Attacher::AttachEngine3D
  Height = 10
  Length = 24
  Placement = pos=(-12,-12,2.1) rot=(0,0,1;0rad)
  Width = 24
FEATURE [Part::Box] Box148  label="Cube132"
  AttacherType = Attacher::AttachEngine3D
  Height = 14
  Length = 20
  Placement = pos=(-10,-10,0) rot=(0,0,1;0rad)
  Width = 20
FEATURE [Part::Cut] Cut043
  Base = -> Box147
  Tool = -> Box148
FEATURE [Part::Chamfer] Chamfer014  label="Glue Channel"
  Base = -> Cut043
  Edges = 8 edges r=0.95: [Edge4,Edge5,Edge14,Edge16,Edge17,Edge18,Edge19,Edge20]
FEATURE [Part::Cut] Cut047
  Base = -> Cut003
  Tool = -> Chamfer007
FEATURE [Part::Cylinder] Cylinder024
  Angle = 360
  AttacherType = Attacher::AttachEngine3D
  Height = 10
  Placement = pos=(-15,-15,-5) rot=(0,0,1;0rad)
  Radius = 1.7
FEATURE [Part::Cylinder] Cylinder025
  Angle = 360
  AttacherType = Attacher::AttachEngine3D
  Height = 10
  Placement = pos=(15,0,-5) rot=(0,0,1;0rad)
  Radius = 1.7
FEATURE [Part::Cylinder] Cylinder026
  Angle = 360
  AttacherType = Attacher::AttachEngine3D
  Height = 10
  Placement = pos=(-15,15,-5) rot=(0,0,1;0rad)
  Radius = 1.7
FEATURE [Part::MultiFuse] Fusion052  label="Screw Holes to remove ball mags"
  Shapes = -> [Cylinder024,Cylinder025,Cylinder026]
FEATURE [Drawing::FeatureViewAnnotation] Annotation
  Font = Sans
  Rotation = 0
  Scale = 7
  Text = 0.4Added in Holes to Mag plate for removal of magnet
  ViewResult = <g transform="translate(14,23) rotate(0)">\n<text id="Annotation"\n font-family="Sans"\n font-size="7"\n fill="#000000">\n<tspan x="0" dy="1em">0.4Added in Holes to Mag plate for removal of magnet</tspan>\n</text>\n</g>
  Visible = false
  X = 14
  Y = 23
FEATURE [Part::Box] Box149  label="Re-level Edge Clip Block001"
  AttacherType = Attacher::AttachEngine3D
  Height = 10
  Length = 12
  Placement = pos=(-21.5,-2,-7) rot=(0,0,1;0rad)
  Width = 44
FEATURE [Part::Fuse] Fusion  label="Bumps"
  Base = -> Sphere008
  Tool = -> Sphere009
FEATURE [Part::Fuse] Fusion053  label="Holes"
  Base = -> Sphere010
  Tool = -> Sphere011
FEATURE [Part::MultiFuse] Fusion054
  Shapes = -> [Box001,Box002,Box003,Box004,Box005]
FEATURE [Part::Fuse] Fusion055
  Base = -> Fusion
  Tool = -> Fusion054
FEATURE [Part::Cut] Cut
  Base = -> Fusion055
  Tool = -> Fusion053
FEATURE [Part::Cut] Cut056
  Base = -> Cut
  Tool = -> Fusion003
FEATURE [Part::Cut] Cut057
  Base = -> Cut056
  Tool = -> Box013
FEATURE [Part::Cut] Cut058
  Base = -> Cut057
  Tool = -> Box149
FEATURE [Part::Cut] Cut059  label="Edge Clips Master"
  Base = -> Cut058
  Placement = pos=(-20,-20,0) rot=(0,0,1;0rad)
  Tool = -> Box006
FEATURE [Part::Box] Box150  label="Cube133"
  AttacherType = Attacher::AttachEngine3D
  Height = 7
  Length = 5
  Placement = pos=(-5,0,-2) rot=(0,0,1;0rad)
  Width = 40
FEATURE [Part::Box] Box151  label="Cube134"
  AttacherType = Attacher::AttachEngine3D
  Height = 7
  Length = 10
  Placement = pos=(-15,6,-2) rot=(0,0,1;0rad)
  Width = 2
FEATURE [Part::Box] Box152  label="Cube135"
  AttacherType = Attacher::AttachEngine3D
  Height = 7
  Length = 10
  Placement = pos=(-15,10,-2) rot=(0,0,1;0rad)
  Width = 2
FEATURE [Part::Box] Box153  label="Cube136"
  AttacherType = Attacher::AttachEngine3D
  Height = 7
  Length = 10
  Placement = pos=(-15,25.4,-2) rot=(0,0,1;0rad)
  Width = 2
FEATURE [Part::Box] Box154  label="Cube137"
  AttacherType = Attacher::AttachEngine3D
  Height = 7
  Length = 10
  Placement = pos=(-15,34.6,-2) rot=(0,0,1;0rad)
  Width = 2
FEATURE [Part::Sphere] Sphere051
  Angle1 = -90
  Angle2 = 90
  Angle3 = 360
  AttacherType = Attacher::AttachEngine3D
  Placement = pos=(-7.5,6.5,0.5) rot=(0,0,1;0rad)
  Radius = 1.25
FEATURE [Part::Box] Box155  label="Chamfer Cube001"
  AttacherType = Attacher::AttachEngine3D
  Height = 10
  Length = 13
  Placement = pos=(-11.69,0,-1.19) rot=(0,-1,0;0.785398rad)
  Width = 40
FEATURE [Part::Sphere] Sphere052
  Angle1 = -90
  Angle2 = 90
  Angle3 = 360
  AttacherType = Attacher::AttachEngine3D
  Placement = pos=(-7.5,11.5,0.5) rot=(0,0,1;0rad)
  Radius = 1.25
FEATURE [Part::Sphere] Sphere053
  Angle1 = -90
  Angle2 = 90
  Angle3 = 360
  AttacherType = Attacher::AttachEngine3D
  Placement = pos=(-7.5,28,0.5) rot=(0,0,1;0rad)
  Radius = 1.5
FEATURE [Part::Sphere] Sphere054
  Angle1 = -90
  Angle2 = 90
  Angle3 = 360
  AttacherType = Attacher::AttachEngine3D
  Placement = pos=(-7.5,34,0.5) rot=(0,0,1;0rad)
  Radius = 1.5
FEATURE [Part::Box] Box156  label="Cube138"
  AttacherType = Attacher::AttachEngine3D
  Height = 7
  Length = 4
  Placement = pos=(-6,5,-2) rot=(0,0,1;0rad)
  Width = 1
FEATURE [Part::Box] Box157  label="Cube139"
  AttacherType = Attacher::AttachEngine3D
  Height = 7
  Length = 4
  Placement = pos=(-6,8,-2) rot=(0,0,1;0rad)
  Width = 2
FEATURE [Part::Box] Box158  label="Cube140"
  AttacherType = Attacher::AttachEngine3D
  Height = 7
  Length = 4
  Placement = pos=(-6,12,-2) rot=(0,0,1;0rad)
  Width = 1
FEATURE [Part::Box] Box159  label="Cube141"
  AttacherType = Attacher::AttachEngine3D
  Height = 7
  Length = 4
  Placement = pos=(-6,24.4,-2) rot=(0,0,1;0rad)
  Width = 1
FEATURE [Part::Box] Box160  label="Cube142"
  AttacherType = Attacher::AttachEngine3D
  Height = 7
  Length = 4
  Placement = pos=(-6,36.6,-2) rot=(0,0,1;0rad)
  Width = 1
FEATURE [Part::Box] Box161  label="Cube143"
  AttacherType = Attacher::AttachEngine3D
  Height = 7
  Length = 4
  Placement = pos=(-6,27.4,-2) rot=(0,0,1;0rad)
  Width = 7.2
FEATURE [Part::MultiFuse] Fusion056  label="Extra Holes for Clips001"
  Shapes = -> [Box161,Box158,Box160,Box157,Box159,Box156]
FEATURE [Part::Box] Box162  label="Re-level Edge Clip Block002"
  AttacherType = Attacher::AttachEngine3D
  Height = 10
  Length = 20
  Placement = pos=(-19,-2,3) rot=(0,0,1;0rad)
  Width = 44
FEATURE [Part::Box] Box163  label="Re-level Edge Clip Block003"
  AttacherType = Attacher::AttachEngine3D
  Height = 10
  Length = 12
  Placement = pos=(-21.5,-2,-7) rot=(0,0,1;0rad)
  Width = 44
FEATURE [Part::Fuse] Fusion057  label="Bumps001"
  Base = -> Sphere051
  Tool = -> Sphere052
FEATURE [Part::Fuse] Fusion058  label="Holes001"
  Base = -> Sphere053
  Tool = -> Sphere054
FEATURE [Part::MultiFuse] Fusion059
  Shapes = -> [Box150,Box151,Box152,Box153,Box154]
FEATURE [Part::Fuse] Fusion060
  Base = -> Fusion057
  Tool = -> Fusion059
FEATURE [Part::Cut] Cut060
  Base = -> Fusion060
  Tool = -> Fusion058
FEATURE [Part::Cut] Cut061
  Base = -> Cut060
  Tool = -> Fusion056
FEATURE [Part::Cut] Cut062
  Base = -> Cut061
  Tool = -> Box162
FEATURE [Part::Cut] Cut063
  Base = -> Cut062
  Tool = -> Box163
FEATURE [Part::Cut] Cut064  label="Copy Edge Clip"
  Base = -> Cut063
  Placement = pos=(-27,20,-7) rot=(0.707107,0,-0.707107;3.14159rad)
  Tool = -> Box155
FEATURE [Part::Box] Box164  label="Cube144"
  AttacherType = Attacher::AttachEngine3D
  Height = 7
  Length = 5
  Placement = pos=(-5,0,-2) rot=(0,0,1;0rad)
  Width = 40
FEATURE [Part::Box] Box165  label="Cube145"
  AttacherType = Attacher::AttachEngine3D
  Height = 7
  Length = 10
  Placement = pos=(-15,6,-2) rot=(0,0,1;0rad)
  Width = 2
FEATURE [Part::Box] Box166  label="Cube146"
  AttacherType = Attacher::AttachEngine3D
  Height = 7
  Length = 10
  Placement = pos=(-15,10,-2) rot=(0,0,1;0rad)
  Width = 2
FEATURE [Part::Box] Box167  label="Cube147"
  AttacherType = Attacher::AttachEngine3D
  Height = 7
  Length = 10
  Placement = pos=(-15,25.4,-2) rot=(0,0,1;0rad)
  Width = 2
FEATURE [Part::Box] Box168  label="Cube148"
  AttacherType = Attacher::AttachEngine3D
  Height = 7
  Length = 10
  Placement = pos=(-15,34.6,-2) rot=(0,0,1;0rad)
  Width = 2
FEATURE [Part::Sphere] Sphere055
  Angle1 = -90
  Angle2 = 90
  Angle3 = 360
  AttacherType = Attacher::AttachEngine3D
  Placement = pos=(-7.5,6.5,0.5) rot=(0,0,1;0rad)
  Radius = 1.25
FEATURE [Part::Box] Box169  label="Chamfer Cube002"
  AttacherType = Attacher::AttachEngine3D
  Height = 10
  Length = 13
  Placement = pos=(-11.69,0,-1.19) rot=(0,-1,0;0.785398rad)
  Width = 40
FEATURE [Part::Sphere] Sphere056
  Angle1 = -90
  Angle2 = 90
  Angle3 = 360
  AttacherType = Attacher::AttachEngine3D
  Placement = pos=(-7.5,11.5,0.5) rot=(0,0,1;0rad)
  Radius = 1.25
FEATURE [Part::Sphere] Sphere057
  Angle1 = -90
  Angle2 = 90
  Angle3 = 360
  AttacherType = Attacher::AttachEngine3D
  Placement = pos=(-7.5,28,0.5) rot=(0,0,1;0rad)
  Radius = 1.5
FEATURE [Part::Sphere] Sphere058
  Angle1 = -90
  Angle2 = 90
  Angle3 = 360
  AttacherType = Attacher::AttachEngine3D
  Placement = pos=(-7.5,34,0.5) rot=(0,0,1;0rad)
  Radius = 1.5
FEATURE [Part::Box] Box170  label="Cube149"
  AttacherType = Attacher::AttachEngine3D
  Height = 7
  Length = 4
  Placement = pos=(-6,5,-2) rot=(0,0,1;0rad)
  Width = 1
FEATURE [Part::Box] Box171  label="Cube150"
  AttacherType = Attacher::AttachEngine3D
  Height = 7
  Length = 4
  Placement = pos=(-6,8,-2) rot=(0,0,1;0rad)
  Width = 2
FEATURE [Part::Box] Box172  label="Cube151"
  AttacherType = Attacher::AttachEngine3D
  Height = 7
  Length = 4
  Placement = pos=(-6,12,-2) rot=(0,0,1;0rad)
  Width = 1
FEATURE [Part::Box] Box173  label="Cube152"
  AttacherType = Attacher::AttachEngine3D
  Height = 7
  Length = 4
  Placement = pos=(-6,24.4,-2) rot=(0,0,1;0rad)
  Width = 1
FEATURE [Part::Box] Box174  label="Cube153"
  AttacherType = Attacher::AttachEngine3D
  Height = 7
  Length = 4
  Placement = pos=(-6,36.6,-2) rot=(0,0,1;0rad)
  Width = 1
FEATURE [Part::Box] Box175  label="Cube154"
  AttacherType = Attacher::AttachEngine3D
  Height = 7
  Length = 4
  Placement = pos=(-6,27.4,-2) rot=(0,0,1;0rad)
  Width = 7.2
FEATURE [Part::MultiFuse] Fusion061  label="Extra Holes for Clips002"
  Shapes = -> [Box175,Box172,Box174,Box171,Box173,Box170]
FEATURE [Part::Box] Box176  label="Re-level Edge Clip Block004"
  AttacherType = Attacher::AttachEngine3D
  Height = 10
  Length = 20
  Placement = pos=(-19,-2,3) rot=(0,0,1;0rad)
  Width = 44
FEATURE [Part::Box] Box177  label="Re-level Edge Clip Block005"
  AttacherType = Attacher::AttachEngine3D
  Height = 10
  Length = 12
  Placement = pos=(-21.5,-2,-7) rot=(0,0,1;0rad)
  Width = 44
FEATURE [Part::Fuse] Fusion062  label="Bumps002"
  Base = -> Sphere055
  Tool = -> Sphere056
FEATURE [Part::Fuse] Fusion063  label="Holes002"
  Base = -> Sphere057
  Tool = -> Sphere058
FEATURE [Part::MultiFuse] Fusion064
  Shapes = -> [Box164,Box165,Box166,Box167,Box168]
FEATURE [Part::Fuse] Fusion065
  Base = -> Fusion062
  Tool = -> Fusion064
FEATURE [Part::Cut] Cut065
  Base = -> Fusion065
  Tool = -> Fusion063
FEATURE [Part::Cut] Cut066
  Base = -> Cut065
  Tool = -> Fusion061
FEATURE [Part::Cut] Cut067
  Base = -> Cut066
  Tool = -> Box176
FEATURE [Part::Cut] Cut068
  Base = -> Cut067
  Tool = -> Box177
FEATURE [Part::Cut] Cut069  label="Edge Clips001"
  Base = -> Cut068
  Placement = pos=(20,-20,0) rot=(0,0,1;1.5708rad)
  Tool = -> Box169
FEATURE [Part::Box] Box178  label="Cube155"
  AttacherType = Attacher::AttachEngine3D
  Height = 7
  Length = 5
  Placement = pos=(-5,0,-2) rot=(0,0,1;0rad)
  Width = 40
FEATURE [Part::Box] Box179  label="Cube156"
  AttacherType = Attacher::AttachEngine3D
  Height = 7
  Length = 10
  Placement = pos=(-15,10,-2) rot=(0,0,1;0rad)
  Width = 2
FEATURE [Part::Box] Box180  label="Re-level Edge Clip Block006"
  AttacherType = Attacher::AttachEngine3D
  Height = 10
  Length = 20
  Placement = pos=(-19,-2,3) rot=(0,0,1;0rad)
  Width = 44
FEATURE [Part::Box] Box181  label="Cube157"
  AttacherType = Attacher::AttachEngine3D
  Height = 7
  Length = 4
  Placement = pos=(-6,27.4,-2) rot=(0,0,1;0rad)
  Width = 7.2
FEATURE [Part::Box] Box182  label="Cube158"
  AttacherType = Attacher::AttachEngine3D
  Height = 7
  Length = 4
  Placement = pos=(-6,12,-2) rot=(0,0,1;0rad)
  Width = 1
FEATURE [Part::Sphere] Sphere059
  Angle1 = -90
  Angle2 = 90
  Angle3 = 360
  AttacherType = Attacher::AttachEngine3D
  Placement = pos=(-7.5,6.5,0.5) rot=(0,0,1;0rad)
  Radius = 1.25
FEATURE [Part::Box] Box183  label="Cube159"
  AttacherType = Attacher::AttachEngine3D
  Height = 7
  Length = 10
  Placement = pos=(-15,25.4,-2) rot=(0,0,1;0rad)
  Width = 2
FEATURE [Part::Box] Box184  label="Cube160"
  AttacherType = Attacher::AttachEngine3D
  Height = 7
  Length = 4
  Placement = pos=(-6,36.6,-2) rot=(0,0,1;0rad)
  Width = 1
FEATURE [Part::Sphere] Sphere060
  Angle1 = -90
  Angle2 = 90
  Angle3 = 360
  AttacherType = Attacher::AttachEngine3D
  Placement = pos=(-7.5,34,0.5) rot=(0,0,1;0rad)
  Radius = 1.5
FEATURE [Part::Box] Box185  label="Cube161"
  AttacherType = Attacher::AttachEngine3D
  Height = 7
  Length = 4
  Placement = pos=(-6,24.4,-2) rot=(0,0,1;0rad)
  Width = 1
FEATURE [Part::Box] Box186  label="Cube162"
  AttacherType = Attacher::AttachEngine3D
  Height = 7
  Length = 4
  Placement = pos=(-6,8,-2) rot=(0,0,1;0rad)
  Width = 2
FEATURE [Part::Box] Box187  label="Re-level Edge Clip Block007"
  AttacherType = Attacher::AttachEngine3D
  Height = 10
  Length = 12
  Placement = pos=(-21.5,-2,-7) rot=(0,0,1;0rad)
  Width = 44
FEATURE [Part::Sphere] Sphere061
  Angle1 = -90
  Angle2 = 90
  Angle3 = 360
  AttacherType = Attacher::AttachEngine3D
  Placement = pos=(-7.5,11.5,0.5) rot=(0,0,1;0rad)
  Radius = 1.25
FEATURE [Part::Sphere] Sphere062
  Angle1 = -90
  Angle2 = 90
  Angle3 = 360
  AttacherType = Attacher::AttachEngine3D
  Placement = pos=(-7.5,28,0.5) rot=(0,0,1;0rad)
  Radius = 1.5
FEATURE [Part::Fuse] Fusion066  label="Holes003"
  Base = -> Sphere062
  Tool = -> Sphere060
FEATURE [Part::Box] Box188  label="Cube163"
  AttacherType = Attacher::AttachEngine3D
  Height = 7
  Length = 10
  Placement = pos=(-15,34.6,-2) rot=(0,0,1;0rad)
  Width = 2
FEATURE [Part::Box] Box189  label="Cube164"
  AttacherType = Attacher::AttachEngine3D
  Height = 7
  Length = 4
  Placement = pos=(-6,5,-2) rot=(0,0,1;0rad)
  Width = 1
FEATURE [Part::MultiFuse] Fusion067  label="Extra Holes for Clips003"
  Shapes = -> [Box181,Box182,Box184,Box186,Box185,Box189]
FEATURE [Part::Box] Box190  label="Cube165"
  AttacherType = Attacher::AttachEngine3D
  Height = 7
  Length = 10
  Placement = pos=(-15,6,-2) rot=(0,0,1;0rad)
  Width = 2
FEATURE [Part::MultiFuse] Fusion069
  Shapes = -> [Box178,Box190,Box179,Box183,Box188]
FEATURE [Part::Fuse] Fusion070  label="Bumps003"
  Base = -> Sphere059
  Tool = -> Sphere061
FEATURE [Part::Fuse] Fusion068
  Base = -> Fusion070
  Tool = -> Fusion069
FEATURE [Part::Cut] Cut073
  Base = -> Fusion068
  Tool = -> Fusion066
FEATURE [Part::Cut] Cut070
  Base = -> Cut073
  Tool = -> Fusion067
FEATURE [Part::Cut] Cut071
  Base = -> Cut070
  Tool = -> Box180
FEATURE [Part::Cut] Cut072
  Base = -> Cut071
  Tool = -> Box187
FEATURE [Part::Box] Box191  label="Chamfer Cube003"
  AttacherType = Attacher::AttachEngine3D
  Height = 10
  Length = 13
  Placement = pos=(-11.69,0,-1.19) rot=(0,-1,0;0.785398rad)
  Width = 40
FEATURE [Part::Cut] Cut074  label="Edge Clips002"
  Base = -> Cut072
  Placement = pos=(20,20,0) rot=(0,0,1;3.14159rad)
  Tool = -> Box191
FEATURE [Part::Box] Box192  label="Cube166"
  AttacherType = Attacher::AttachEngine3D
  Height = 7
  Length = 10
  Placement = pos=(-15,6,-2) rot=(0,0,1;0rad)
  Width = 2
FEATURE [Part::Box] Box193  label="Chamfer Cube004"
  AttacherType = Attacher::AttachEngine3D
  Height = 10
  Length = 13
  Placement = pos=(-11.69,0,-1.19) rot=(0,-1,0;0.785398rad)
  Width = 40
FEATURE [Part::Box] Box194  label="Re-level Edge Clip Block008"
  AttacherType = Attacher::AttachEngine3D
  Height = 10
  Length = 20
  Placement = pos=(-19,-2,3) rot=(0,0,1;0rad)
  Width = 44
FEATURE [Part::Box] Box195  label="Cube167"
  AttacherType = Attacher::AttachEngine3D
  Height = 7
  Length = 10
  Placement = pos=(-15,10,-2) rot=(0,0,1;0rad)
  Width = 2
FEATURE [Part::Box] Box196  label="Cube168"
  AttacherType = Attacher::AttachEngine3D
  Height = 7
  Length = 5
  Placement = pos=(-5,0,-2) rot=(0,0,1;0rad)
  Width = 40
FEATURE [Part::Box] Box197  label="Cube169"
  AttacherType = Attacher::AttachEngine3D
  Height = 7
  Length = 4
  Placement = pos=(-6,5,-2) rot=(0,0,1;0rad)
  Width = 1
FEATURE [Part::Box] Box198  label="Cube170"
  AttacherType = Attacher::AttachEngine3D
  Height = 7
  Length = 4
  Placement = pos=(-6,12,-2) rot=(0,0,1;0rad)
  Width = 1
FEATURE [Part::Box] Box199  label="Cube171"
  AttacherType = Attacher::AttachEngine3D
  Height = 7
  Length = 4
  Placement = pos=(-6,27.4,-2) rot=(0,0,1;0rad)
  Width = 7.2
FEATURE [Part::Box] Box200  label="Cube172"
  AttacherType = Attacher::AttachEngine3D
  Height = 7
  Length = 4
  Placement = pos=(-6,24.4,-2) rot=(0,0,1;0rad)
  Width = 1
FEATURE [Part::Sphere] Sphere063
  Angle1 = -90
  Angle2 = 90
  Angle3 = 360
  AttacherType = Attacher::AttachEngine3D
  Placement = pos=(-7.5,28,0.5) rot=(0,0,1;0rad)
  Radius = 1.5
FEATURE [Part::Sphere] Sphere064
  Angle1 = -90
  Angle2 = 90
  Angle3 = 360
  AttacherType = Attacher::AttachEngine3D
  Placement = pos=(-7.5,11.5,0.5) rot=(0,0,1;0rad)
  Radius = 1.25
FEATURE [Part::Box] Box201  label="Cube173"
  AttacherType = Attacher::AttachEngine3D
  Height = 7
  Length = 4
  Placement = pos=(-6,8,-2) rot=(0,0,1;0rad)
  Width = 2
FEATURE [Part::Box] Box202  label="Cube174"
  AttacherType = Attacher::AttachEngine3D
  Height = 7
  Length = 10
  Placement = pos=(-15,25.4,-2) rot=(0,0,1;0rad)
  Width = 2
FEATURE [Part::Sphere] Sphere065
  Angle1 = -90
  Angle2 = 90
  Angle3 = 360
  AttacherType = Attacher::AttachEngine3D
  Placement = pos=(-7.5,6.5,0.5) rot=(0,0,1;0rad)
  Radius = 1.25
FEATURE [Part::Fuse] Fusion073  label="Bumps004"
  Base = -> Sphere065
  Tool = -> Sphere064
FEATURE [Part::Sphere] Sphere066
  Angle1 = -90
  Angle2 = 90
  Angle3 = 360
  AttacherType = Attacher::AttachEngine3D
  Placement = pos=(-7.5,34,0.5) rot=(0,0,1;0rad)
  Radius = 1.5
FEATURE [Part::Fuse] Fusion071  label="Holes004"
  Base = -> Sphere063
  Tool = -> Sphere066
FEATURE [Part::Box] Box203  label="Re-level Edge Clip Block009"
  AttacherType = Attacher::AttachEngine3D
  Height = 10
  Length = 12
  Placement = pos=(-21.5,-2,-7) rot=(0,0,1;0rad)
  Width = 44
FEATURE [Part::Box] Box204  label="Cube175"
  AttacherType = Attacher::AttachEngine3D
  Height = 7
  Length = 4
  Placement = pos=(-6,36.6,-2) rot=(0,0,1;0rad)
  Width = 1
FEATURE [Part::MultiFuse] Fusion074  label="Extra Holes for Clips004"
  Shapes = -> [Box199,Box198,Box204,Box201,Box200,Box197]
FEATURE [Part::Box] Box205  label="Cube176"
  AttacherType = Attacher::AttachEngine3D
  Height = 7
  Length = 10
  Placement = pos=(-15,34.6,-2) rot=(0,0,1;0rad)
  Width = 2
FEATURE [Part::MultiFuse] Fusion072
  Shapes = -> [Box196,Box192,Box195,Box202,Box205]
FEATURE [Part::Fuse] Fusion075
  Base = -> Fusion073
  Tool = -> Fusion072
FEATURE [Part::Cut] Cut075
  Base = -> Fusion075
  Tool = -> Fusion071
FEATURE [Part::Cut] Cut076
  Base = -> Cut075
  Tool = -> Fusion074
FEATURE [Part::Cut] Cut078
  Base = -> Cut076
  Tool = -> Box194
FEATURE [Part::Cut] Cut077
  Base = -> Cut078
  Tool = -> Box203
FEATURE [Part::Cut] Cut079  label="Edge Clips003"
  Base = -> Cut077
  Placement = pos=(-20,20,0) rot=(0,0,-1;1.5708rad)
  Tool = -> Box193
FEATURE [Part::MultiFuse] Fusion076  label="Edge Clips Fusion"
  Shapes = -> [Cut059,Cut069,Cut074,Cut079]
FEATURE [Part::Box] Box206  label="Cube177"
  AttacherType = Attacher::AttachEngine3D
  Height = 10
  Length = 10
  Placement = pos=(26,4,1) rot=(0.442189,-0.287968,0.849437;1.66134rad)
  Width = 15
FEATURE [Part::Box] Box207  label="Cube178"
  AttacherType = Attacher::AttachEngine3D
  Height = 10
  Length = 10
  Placement = pos=(-4,26,1) rot=(0.381439,0.080566,0.920876;3.07487rad)
  Width = 15
FEATURE [Part::Box] Box208  label="Cube179"
  AttacherType = Attacher::AttachEngine3D
  Height = 10
  Length = 10
  Placement = pos=(-26,-4,1) rot=(-0.273007,-0.419215,-0.865867;1.78566rad)
  Width = 15
FEATURE [Part::MultiFuse] Fusion078  label="Glue Dents"
  Shapes = -> [Box086,Box208,Box207,Box206]
FEATURE [Part::Box] Box209  label="Cube180"
  AttacherType = Attacher::AttachEngine3D
  Height = 7
  Length = 5
  Placement = pos=(-5,0,-2) rot=(0,0,1;0rad)
  Width = 40
FEATURE [Part::Box] Box210  label="Cube181"
  AttacherType = Attacher::AttachEngine3D
  Height = 7
  Length = 10
  Placement = pos=(-15,6,-2) rot=(0,0,1;0rad)
  Width = 2
FEATURE [Part::Box] Box211  label="Cube182"
  AttacherType = Attacher::AttachEngine3D
  Height = 7
  Length = 10
  Placement = pos=(-15,10,-2) rot=(0,0,1;0rad)
  Width = 2
FEATURE [Part::Box] Box212  label="Cube183"
  AttacherType = Attacher::AttachEngine3D
  Height = 7
  Length = 10
  Placement = pos=(-15,25.4,-2) rot=(0,0,1;0rad)
  Width = 2
FEATURE [Part::Box] Box213  label="Cube184"
  AttacherType = Attacher::AttachEngine3D
  Height = 7
  Length = 10
  Placement = pos=(-15,34.6,-2) rot=(0,0,1;0rad)
  Width = 2
FEATURE [Part::Sphere] Sphere067
  Angle1 = -90
  Angle2 = 90
  Angle3 = 360
  AttacherType = Attacher::AttachEngine3D
  Placement = pos=(-7.5,6.5,0.5) rot=(0,0,1;0rad)
  Radius = 1.25
FEATURE [Part::Box] Box214  label="Chamfer Cube005"
  AttacherType = Attacher::AttachEngine3D
  Height = 10
  Length = 13
  Placement = pos=(-11.69,0,-1.19) rot=(0,-1,0;0.785398rad)
  Width = 40
FEATURE [Part::Sphere] Sphere068
  Angle1 = -90
  Angle2 = 90
  Angle3 = 360
  AttacherType = Attacher::AttachEngine3D
  Placement = pos=(-7.5,11.5,0.5) rot=(0,0,1;0rad)
  Radius = 1.25
FEATURE [Part::Sphere] Sphere069
  Angle1 = -90
  Angle2 = 90
  Angle3 = 360
  AttacherType = Attacher::AttachEngine3D
  Placement = pos=(-7.5,28,0.5) rot=(0,0,1;0rad)
  Radius = 1.5
FEATURE [Part::Sphere] Sphere070
  Angle1 = -90
  Angle2 = 90
  Angle3 = 360
  AttacherType = Attacher::AttachEngine3D
  Placement = pos=(-7.5,34,0.5) rot=(0,0,1;0rad)
  Radius = 1.5
FEATURE [Part::Box] Box215  label="Cube185"
  AttacherType = Attacher::AttachEngine3D
  Height = 7
  Length = 4
  Placement = pos=(-6,5,-2) rot=(0,0,1;0rad)
  Width = 1
FEATURE [Part::Box] Box216  label="Cube186"
  AttacherType = Attacher::AttachEngine3D
  Height = 7
  Length = 4
  Placement = pos=(-6,8,-2) rot=(0,0,1;0rad)
  Width = 2
FEATURE [Part::Box] Box217  label="Cube187"
  AttacherType = Attacher::AttachEngine3D
  Height = 7
  Length = 4
  Placement = pos=(-6,12,-2) rot=(0,0,1;0rad)
  Width = 1
FEATURE [Part::Box] Box218  label="Cube188"
  AttacherType = Attacher::AttachEngine3D
  Height = 7
  Length = 4
  Placement = pos=(-6,24.4,-2) rot=(0,0,1;0rad)
  Width = 1
FEATURE [Part::Box] Box219  label="Cube189"
  AttacherType = Attacher::AttachEngine3D
  Height = 7
  Length = 4
  Placement = pos=(-6,36.6,-2) rot=(0,0,1;0rad)
  Width = 1
FEATURE [Part::Box] Box220  label="Cube190"
  AttacherType = Attacher::AttachEngine3D
  Height = 7
  Length = 4
  Placement = pos=(-6,27.4,-2) rot=(0,0,1;0rad)
  Width = 7.2
FEATURE [Part::MultiFuse] Fusion079  label="Extra Holes for Clips005"
  Shapes = -> [Box220,Box217,Box219,Box216,Box218,Box215]
FEATURE [Part::Box] Box221  label="Re-level Edge Clip Block010"
  AttacherType = Attacher::AttachEngine3D
  Height = 10
  Length = 20
  Placement = pos=(-19,-2,3) rot=(0,0,1;0rad)
  Width = 44
FEATURE [Part::Box] Box222  label="Re-level Edge Clip Block011"
  AttacherType = Attacher::AttachEngine3D
  Height = 10
  Length = 12
  Placement = pos=(-21.5,-2,-7) rot=(0,0,1;0rad)
  Width = 44
FEATURE [Part::Fuse] Fusion080  label="Bumps005"
  Base = -> Sphere067
  Tool = -> Sphere068
FEATURE [Part::Fuse] Fusion081  label="Holes005"
  Base = -> Sphere069
  Tool = -> Sphere070
FEATURE [Part::MultiFuse] Fusion082
  Shapes = -> [Box209,Box210,Box211,Box212,Box213]
FEATURE [Part::Fuse] Fusion083
  Base = -> Fusion080
  Tool = -> Fusion082
FEATURE [Part::Cut] Cut082
  Base = -> Fusion083
  Tool = -> Fusion081
FEATURE [Part::Cut] Cut083
  Base = -> Cut082
  Tool = -> Fusion079
FEATURE [Part::Cut] Cut084
  Base = -> Cut083
  Tool = -> Box221
FEATURE [Part::Cut] Cut085
  Base = -> Cut084
  Tool = -> Box222
FEATURE [Part::Cut] Cut086  label="Edge Clips Master001"
  Base = -> Cut085
  Placement = pos=(-20,-20,0) rot=(0,0,1;0rad)
  Tool = -> Box214
FEATURE [Part::Box] Box223  label="Cube191"
  AttacherType = Attacher::AttachEngine3D
  Height = 7
  Length = 5
  Placement = pos=(-5,0,-2) rot=(0,0,1;0rad)
  Width = 40
FEATURE [Part::Box] Box224  label="Cube192"
  AttacherType = Attacher::AttachEngine3D
  Height = 7
  Length = 4
  Placement = pos=(-6,8,-2) rot=(0,0,1;0rad)
  Width = 2
FEATURE [Part::Box] Box225  label="Chamfer Cube006"
  AttacherType = Attacher::AttachEngine3D
  Height = 10
  Length = 13
  Placement = pos=(-11.69,0,-1.19) rot=(0,-1,0;0.785398rad)
  Width = 40
FEATURE [Part::Box] Box226  label="Cube193"
  AttacherType = Attacher::AttachEngine3D
  Height = 7
  Length = 10
  Placement = pos=(-15,6,-2) rot=(0,0,1;0rad)
  Width = 2
FEATURE [Part::Sphere] Sphere071
  Angle1 = -90
  Angle2 = 90
  Angle3 = 360
  AttacherType = Attacher::AttachEngine3D
  Placement = pos=(-7.5,11.5,0.5) rot=(0,0,1;0rad)
  Radius = 1.25
FEATURE [Part::Box] Box227  label="Cube194"
  AttacherType = Attacher::AttachEngine3D
  Height = 7
  Length = 4
  Placement = pos=(-6,27.4,-2) rot=(0,0,1;0rad)
  Width = 7.2
FEATURE [Part::Box] Box228  label="Cube195"
  AttacherType = Attacher::AttachEngine3D
  Height = 7
  Length = 4
  Placement = pos=(-6,12,-2) rot=(0,0,1;0rad)
  Width = 1
FEATURE [Part::Box] Box229  label="Cube196"
  AttacherType = Attacher::AttachEngine3D
  Height = 7
  Length = 4
  Placement = pos=(-6,24.4,-2) rot=(0,0,1;0rad)
  Width = 1
FEATURE [Part::Sphere] Sphere072
  Angle1 = -90
  Angle2 = 90
  Angle3 = 360
  AttacherType = Attacher::AttachEngine3D
  Placement = pos=(-7.5,6.5,0.5) rot=(0,0,1;0rad)
  Radius = 1.25
FEATURE [Part::Box] Box230  label="Cube197"
  AttacherType = Attacher::AttachEngine3D
  Height = 7
  Length = 4
  Placement = pos=(-6,36.6,-2) rot=(0,0,1;0rad)
  Width = 1
FEATURE [Part::Box] Box231  label="Cube198"
  AttacherType = Attacher::AttachEngine3D
  Height = 7
  Length = 10
  Placement = pos=(-15,10,-2) rot=(0,0,1;0rad)
  Width = 2
FEATURE [Part::Sphere] Sphere073
  Angle1 = -90
  Angle2 = 90
  Angle3 = 360
  AttacherType = Attacher::AttachEngine3D
  Placement = pos=(-7.5,34,0.5) rot=(0,0,1;0rad)
  Radius = 1.5
FEATURE [Part::Box] Box232  label="Cube199"
  AttacherType = Attacher::AttachEngine3D
  Height = 7
  Length = 4
  Placement = pos=(-6,5,-2) rot=(0,0,1;0rad)
  Width = 1
FEATURE [Part::MultiFuse] Fusion085  label="Extra Holes for Clips006"
  Shapes = -> [Box227,Box228,Box230,Box224,Box229,Box232]
FEATURE [Part::Box] Box233  label="Re-level Edge Clip Block012"
  AttacherType = Attacher::AttachEngine3D
  Height = 10
  Length = 20
  Placement = pos=(-19,-2,3) rot=(0,0,1;0rad)
  Width = 44
FEATURE [Part::Box] Box234  label="Cube200"
  AttacherType = Attacher::AttachEngine3D
  Height = 7
  Length = 10
  Placement = pos=(-15,34.6,-2) rot=(0,0,1;0rad)
  Width = 2
FEATURE [Part::Box] Box235  label="Cube201"
  AttacherType = Attacher::AttachEngine3D
  Height = 7
  Length = 10
  Placement = pos=(-15,25.4,-2) rot=(0,0,1;0rad)
  Width = 2
FEATURE [Part::MultiFuse] Fusion086
  Shapes = -> [Box223,Box226,Box231,Box235,Box234]
FEATURE [Part::Fuse] Fusion087  label="Bumps006"
  Base = -> Sphere072
  Tool = -> Sphere071
FEATURE [Part::Fuse] Fusion084
  Base = -> Fusion087
  Tool = -> Fusion086
FEATURE [Part::Sphere] Sphere074
  Angle1 = -90
  Angle2 = 90
  Angle3 = 360
  AttacherType = Attacher::AttachEngine3D
  Placement = pos=(-7.5,28,0.5) rot=(0,0,1;0rad)
  Radius = 1.5
FEATURE [Part::Fuse] Fusion088  label="Holes006"
  Base = -> Sphere074
  Tool = -> Sphere073
FEATURE [Part::Box] Box236  label="Re-level Edge Clip Block013"
  AttacherType = Attacher::AttachEngine3D
  Height = 10
  Length = 12
  Placement = pos=(-21.5,-2,-7) rot=(0,0,1;0rad)
  Width = 44
FEATURE [Part::Cut] Cut087
  Base = -> Fusion084
  Tool = -> Fusion088
FEATURE [Part::Cut] Cut088
  Base = -> Cut087
  Tool = -> Fusion085
FEATURE [Part::Cut] Cut089
  Base = -> Cut088
  Tool = -> Box233
FEATURE [Part::Cut] Cut090
  Base = -> Cut089
  Tool = -> Box236
FEATURE [Part::Cut] Cut091  label="Edge Clips004"
  Base = -> Cut090
  Placement = pos=(20,-20,0) rot=(0,0,1;1.5708rad)
  Tool = -> Box225
FEATURE [Part::Box] Box237  label="Re-level Edge Clip Block014"
  AttacherType = Attacher::AttachEngine3D
  Height = 10
  Length = 12
  Placement = pos=(-21.5,-2,-7) rot=(0,0,1;0rad)
  Width = 44
FEATURE [Part::Box] Box238  label="Cube202"
  AttacherType = Attacher::AttachEngine3D
  Height = 7
  Length = 4
  Placement = pos=(-6,36.6,-2) rot=(0,0,1;0rad)
  Width = 1
FEATURE [Part::Box] Box239  label="Cube203"
  AttacherType = Attacher::AttachEngine3D
  Height = 7
  Length = 10
  Placement = pos=(-15,10,-2) rot=(0,0,1;0rad)
  Width = 2
FEATURE [Part::Box] Box240  label="Cube204"
  AttacherType = Attacher::AttachEngine3D
  Height = 7
  Length = 10
  Placement = pos=(-15,25.4,-2) rot=(0,0,1;0rad)
  Width = 2
FEATURE [Part::Box] Box241  label="Re-level Edge Clip Block015"
  AttacherType = Attacher::AttachEngine3D
  Height = 10
  Length = 20
  Placement = pos=(-19,-2,3) rot=(0,0,1;0rad)
  Width = 44
FEATURE [Part::Box] Box242  label="Cube205"
  AttacherType = Attacher::AttachEngine3D
  Height = 7
  Length = 10
  Placement = pos=(-15,34.6,-2) rot=(0,0,1;0rad)
  Width = 2
FEATURE [Part::Sphere] Sphere075
  Angle1 = -90
  Angle2 = 90
  Angle3 = 360
  AttacherType = Attacher::AttachEngine3D
  Placement = pos=(-7.5,34,0.5) rot=(0,0,1;0rad)
  Radius = 1.5
FEATURE [Part::Sphere] Sphere076
  Angle1 = -90
  Angle2 = 90
  Angle3 = 360
  AttacherType = Attacher::AttachEngine3D
  Placement = pos=(-7.5,28,0.5) rot=(0,0,1;0rad)
  Radius = 1.5
FEATURE [Part::Fuse] Fusion089  label="Holes007"
  Base = -> Sphere076
  Tool = -> Sphere075
FEATURE [Part::Box] Box243  label="Cube206"
  AttacherType = Attacher::AttachEngine3D
  Height = 7
  Length = 4
  Placement = pos=(-6,5,-2) rot=(0,0,1;0rad)
  Width = 1
FEATURE [Part::Box] Box244  label="Cube207"
  AttacherType = Attacher::AttachEngine3D
  Height = 7
  Length = 4
  Placement = pos=(-6,24.4,-2) rot=(0,0,1;0rad)
  Width = 1
FEATURE [Part::Sphere] Sphere077
  Angle1 = -90
  Angle2 = 90
  Angle3 = 360
  AttacherType = Attacher::AttachEngine3D
  Placement = pos=(-7.5,11.5,0.5) rot=(0,0,1;0rad)
  Radius = 1.25
FEATURE [Part::Box] Box245  label="Cube208"
  AttacherType = Attacher::AttachEngine3D
  Height = 7
  Length = 4
  Placement = pos=(-6,12,-2) rot=(0,0,1;0rad)
  Width = 1
FEATURE [Part::Box] Box246  label="Chamfer Cube007"
  AttacherType = Attacher::AttachEngine3D
  Height = 10
  Length = 13
  Placement = pos=(-11.69,0,-1.19) rot=(0,-1,0;0.785398rad)
  Width = 40
FEATURE [Part::Sphere] Sphere078
  Angle1 = -90
  Angle2 = 90
  Angle3 = 360
  AttacherType = Attacher::AttachEngine3D
  Placement = pos=(-7.5,6.5,0.5) rot=(0,0,1;0rad)
  Radius = 1.25
FEATURE [Part::Fuse] Fusion090  label="Bumps007"
  Base = -> Sphere078
  Tool = -> Sphere077
FEATURE [Part::Box] Box247  label="Cube209"
  AttacherType = Attacher::AttachEngine3D
  Height = 7
  Length = 5
  Placement = pos=(-5,0,-2) rot=(0,0,1;0rad)
  Width = 40
FEATURE [Part::Box] Box248  label="Cube210"
  AttacherType = Attacher::AttachEngine3D
  Height = 7
  Length = 4
  Placement = pos=(-6,27.4,-2) rot=(0,0,1;0rad)
  Width = 7.2
FEATURE [Part::Box] Box249  label="Cube211"
  AttacherType = Attacher::AttachEngine3D
  Height = 7
  Length = 4
  Placement = pos=(-6,8,-2) rot=(0,0,1;0rad)
  Width = 2
FEATURE [Part::MultiFuse] Fusion091  label="Extra Holes for Clips007"
  Shapes = -> [Box248,Box245,Box238,Box249,Box244,Box243]
FEATURE [Part::Box] Box250  label="Cube212"
  AttacherType = Attacher::AttachEngine3D
  Height = 7
  Length = 10
  Placement = pos=(-15,6,-2) rot=(0,0,1;0rad)
  Width = 2
FEATURE [Part::MultiFuse] Fusion092
  Shapes = -> [Box247,Box250,Box239,Box240,Box242]
FEATURE [Part::Fuse] Fusion093
  Base = -> Fusion090
  Tool = -> Fusion092
FEATURE [Part::Cut] Cut093
  Base = -> Fusion093
  Tool = -> Fusion089
FEATURE [Part::Cut] Cut094
  Base = -> Cut093
  Tool = -> Fusion091
FEATURE [Part::Cut] Cut095
  Base = -> Cut094
  Tool = -> Box241
FEATURE [Part::Cut] Cut096
  Base = -> Cut095
  Tool = -> Box237
FEATURE [Part::Cut] Cut092  label="Edge Clips005"
  Base = -> Cut096
  Placement = pos=(20,20,0) rot=(0,0,1;3.14159rad)
  Tool = -> Box246
FEATURE [Part::Box] Box251  label="Re-level Edge Clip Block016"
  AttacherType = Attacher::AttachEngine3D
  Height = 10
  Length = 12
  Placement = pos=(-21.5,-2,-7) rot=(0,0,1;0rad)
  Width = 44
FEATURE [Part::Box] Box252  label="Cube213"
  AttacherType = Attacher::AttachEngine3D
  Height = 7
  Length = 10
  Placement = pos=(-15,10,-2) rot=(0,0,1;0rad)
  Width = 2
FEATURE [Part::Box] Box253  label="Cube214"
  AttacherType = Attacher::AttachEngine3D
  Height = 7
  Length = 4
  Placement = pos=(-6,12,-2) rot=(0,0,1;0rad)
  Width = 1
FEATURE [Part::Box] Box254  label="Chamfer Cube008"
  AttacherType = Attacher::AttachEngine3D
  Height = 10
  Length = 13
  Placement = pos=(-11.69,0,-1.19) rot=(0,-1,0;0.785398rad)
  Width = 40
FEATURE [Part::Sphere] Sphere079
  Angle1 = -90
  Angle2 = 90
  Angle3 = 360
  AttacherType = Attacher::AttachEngine3D
  Placement = pos=(-7.5,6.5,0.5) rot=(0,0,1;0rad)
  Radius = 1.25
FEATURE [Part::Box] Box255  label="Cube215"
  AttacherType = Attacher::AttachEngine3D
  Height = 7
  Length = 5
  Placement = pos=(-5,0,-2) rot=(0,0,1;0rad)
  Width = 40
FEATURE [Part::Box] Box256  label="Cube216"
  AttacherType = Attacher::AttachEngine3D
  Height = 7
  Length = 4
  Placement = pos=(-6,27.4,-2) rot=(0,0,1;0rad)
  Width = 7.2
FEATURE [Part::Box] Box257  label="Cube217"
  AttacherType = Attacher::AttachEngine3D
  Height = 7
  Length = 4
  Placement = pos=(-6,8,-2) rot=(0,0,1;0rad)
  Width = 2
FEATURE [Part::Box] Box258  label="Cube218"
  AttacherType = Attacher::AttachEngine3D
  Height = 7
  Length = 10
  Placement = pos=(-15,6,-2) rot=(0,0,1;0rad)
  Width = 2
FEATURE [Part::Sphere] Sphere080
  Angle1 = -90
  Angle2 = 90
  Angle3 = 360
  AttacherType = Attacher::AttachEngine3D
  Placement = pos=(-7.5,28,0.5) rot=(0,0,1;0rad)
  Radius = 1.5
FEATURE [Part::Box] Box259  label="Cube219"
  AttacherType = Attacher::AttachEngine3D
  Height = 7
  Length = 4
  Placement = pos=(-6,5,-2) rot=(0,0,1;0rad)
  Width = 1
FEATURE [Part::Box] Box260  label="Cube220"
  AttacherType = Attacher::AttachEngine3D
  Height = 7
  Length = 4
  Placement = pos=(-6,24.4,-2) rot=(0,0,1;0rad)
  Width = 1
FEATURE [Part::Sphere] Sphere081
  Angle1 = -90
  Angle2 = 90
  Angle3 = 360
  AttacherType = Attacher::AttachEngine3D
  Placement = pos=(-7.5,11.5,0.5) rot=(0,0,1;0rad)
  Radius = 1.25
FEATURE [Part::Box] Box261  label="Re-level Edge Clip Block017"
  AttacherType = Attacher::AttachEngine3D
  Height = 10
  Length = 20
  Placement = pos=(-19,-2,3) rot=(0,0,1;0rad)
  Width = 44
FEATURE [Part::Box] Box262  label="Cube221"
  AttacherType = Attacher::AttachEngine3D
  Height = 7
  Length = 10
  Placement = pos=(-15,34.6,-2) rot=(0,0,1;0rad)
  Width = 2
FEATURE [Part::Box] Box263  label="Cube222"
  AttacherType = Attacher::AttachEngine3D
  Height = 7
  Length = 10
  Placement = pos=(-15,25.4,-2) rot=(0,0,1;0rad)
  Width = 2
FEATURE [Part::MultiFuse] Fusion096
  Shapes = -> [Box255,Box258,Box252,Box263,Box262]
FEATURE [Part::Box] Box264  label="Cube223"
  AttacherType = Attacher::AttachEngine3D
  Height = 7
  Length = 4
  Placement = pos=(-6,36.6,-2) rot=(0,0,1;0rad)
  Width = 1
FEATURE [Part::MultiFuse] Fusion095  label="Extra Holes for Clips008"
  Shapes = -> [Box256,Box253,Box264,Box257,Box260,Box259]
FEATURE [Part::Fuse] Fusion098  label="Bumps008"
  Base = -> Sphere079
  Tool = -> Sphere081
FEATURE [Part::Fuse] Fusion094
  Base = -> Fusion098
  Tool = -> Fusion096
FEATURE [Part::Sphere] Sphere082
  Angle1 = -90
  Angle2 = 90
  Angle3 = 360
  AttacherType = Attacher::AttachEngine3D
  Placement = pos=(-7.5,34,0.5) rot=(0,0,1;0rad)
  Radius = 1.5
FEATURE [Part::Fuse] Fusion097  label="Holes008"
  Base = -> Sphere080
  Tool = -> Sphere082
FEATURE [Part::Cut] Cut101
  Base = -> Fusion094
  Tool = -> Fusion097
FEATURE [Part::Cut] Cut097
  Base = -> Cut101
  Tool = -> Fusion095
FEATURE [Part::Cut] Cut098
  Base = -> Cut097
  Tool = -> Box261
FEATURE [Part::Cut] Cut099
  Base = -> Cut098
  Tool = -> Box251
FEATURE [Part::Cut] Cut100  label="Edge Clips006"
  Base = -> Cut099
  Placement = pos=(-20,20,0) rot=(0,0,-1;1.5708rad)
  Tool = -> Box254
FEATURE [Part::Box] Box265  label="Cube224"
  AttacherType = Attacher::AttachEngine3D
  Height = 10
  Length = 10
  Placement = pos=(4,-26,1) rot=(0.205904,-0.974848,-0.085288;0.803573rad)
  Width = 15
FEATURE [Part::Box] Box266  label="Cube225"
  AttacherType = Attacher::AttachEngine3D
  Height = 10
  Length = 10
  Placement = pos=(-26,-4,1) rot=(-0.273007,-0.419215,-0.865867;1.78566rad)
  Width = 15
FEATURE [Part::Box] Box267  label="Cube226"
  AttacherType = Attacher::AttachEngine3D
  Height = 10
  Length = 10
  Placement = pos=(-4,26,1) rot=(0.381439,0.080566,0.920876;3.07487rad)
  Width = 15
FEATURE [Part::Box] Box268  label="Cube227"
  AttacherType = Attacher::AttachEngine3D
  Height = 10
  Length = 10
  Placement = pos=(26,4,1) rot=(0.442189,-0.287968,0.849437;1.66134rad)
  Width = 15
FEATURE [Part::MultiFuse] Fusion099  label="Glue Dents001"
  Shapes = -> [Box265,Box266,Box267,Box268]
FEATURE [Part::MultiFuse] Fusion100  label="Edge Clips Fusion001"
  Shapes = -> [Cut100,Cut086,Cut091,Cut092]
FEATURE [Drawing::FeatureViewAnnotation] Annotation001
  Font = Sans
  Rotation = 0
  Scale = 7
  Text = 0.5 rejigged whole thing, stopped clips overhang and moved bump and holes back 0.5
  ViewResult = <g transform="translate(14,30) rotate(0)">\n<text id="Annotation001"\n font-family="Sans"\n font-size="7"\n fill="#000000">\n<tspan x="0" dy="1em">0.5 rejigged whole thing, stopped clips overhang and moved bump and holes back 0.5</tspan>\n</text>\n</g>
  Visible = false
  X = 14
  Y = 30
FEATURE [Part::Cylinder] Cylinder027  label="z-axis"
  Angle = 360
  AttacherType = Attacher::AttachEngine3D
  Height = 73
  Placement = pos=(0,0,-18) rot=(0,0,1;0rad)
  Radius = 0.5
FEATURE [Part::MultiFuse] Fusion101
  Placement = pos=(-15,-15,0) rot=(0,0,1;0rad)
  Shapes = -> [Box069,Cylinder018,Sphere030]
FEATURE [App::DocumentObjectGroup] Group002  label="Old 0.1"
  Group = -> [Sphere027,Sphere028,Sphere029,Sphere031,Sphere032,Sphere033,Sphere034,Cylinder012,Cylinder016,Cylinder015,Cylinder014,Cylinder013,Cylinder017,Cylinder019,Box067,Box073,Box071,Box068,Box070,Box072,Box074]
FEATURE [Part::Box] Box269  label="Square Nut Hole 024"
  AttacherType = Attacher::AttachEngine3D
  Height = 2
  Length = 5.8
  Placement = pos=(-2.9,2.9,2.1) rot=(1,0,0;3.14159rad)
  Width = 5.8
FEATURE [Part::Cylinder] Cylinder028
  Angle = 360
  AttacherType = Attacher::AttachEngine3D
  Height = 10
  Placement = pos=(0,0,6.7) rot=(1,0,0;3.14159rad)
  Radius = 1.7
FEATURE [Part::Sphere] Sphere083
  Angle1 = -90
  Angle2 = 90
  Angle3 = 360
  AttacherType = Attacher::AttachEngine3D
  Placement = pos=(0,0,4.3) rot=(1,0,0;3.14159rad)
  Radius = 3.35
FEATURE [Part::MultiFuse] Fusion102
  Placement = pos=(-15,0,0) rot=(0,0,1;0rad)
  Shapes = -> [Box269,Cylinder028,Sphere083]
FEATURE [Part::Fuse] Fusion103
  Base = -> Fusion101
  Tool = -> Fusion102
FEATURE [Part::Feature] Fusion103001
  Placement = pos=(0,0,0) rot=(0,0,1;1.5708rad)
  shape: bbox 21.7 x 6.7 x 10.95 mm, 18 faces, 2 solids (baked)
FEATURE [Part::Feature] Fusion103002
  Placement = pos=(0,0,0) rot=(0,0,1;3.14159rad)
  shape: bbox 6.7 x 21.7 x 10.95 mm, 18 faces, 2 solids (baked)
FEATURE [Part::Feature] Fusion103003
  Placement = pos=(0,0,0) rot=(0,0,-1;1.5708rad)
  shape: bbox 21.7 x 6.7 x 10.95 mm, 18 faces, 2 solids (baked)
FEATURE [Part::MultiFuse] Fusion103004  label="Nut Holes"
  Shapes = -> [Fusion103,Fusion103001,Fusion103002,Fusion103003]
FEATURE [Part::Fuse] Fusion103005  label="Cube with Edge Clips"
  Base = -> Box075
  Tool = -> Fusion100
FEATURE [Part::Cut] Cut102
  Base = -> Fusion103005
  Tool = -> Fusion099
FEATURE [Part::Cut] Cut103
  Base = -> Cut102
  Tool = -> Fusion103004
FEATURE [Part::Cut] Cut104
  Base = -> Cut103
  Tool = -> Chamfer014
FEATURE [Part::Cut] Cut105
  Base = -> Cut104
  Tool = -> Chamfer013
FEATURE [Part::Cut] Cut106  label="Nut Plate 1.1"
  Base = -> Cut105
  Tool = -> Box145
FEATURE [Part::Fuse] Fusion103006
  Base = -> Cut047
  Tool = -> Fusion076
FEATURE [Part::Cut] Cut107
  Base = -> Fusion103006
  Tool = -> Fusion052
FEATURE [Part::Cut] Cut108
  Base = -> Cut107
  Tool = -> Chamfer008
FEATURE [Part::Cut] Cut109
  Base = -> Cut108
  Tool = -> Box085
FEATURE [Part::Cut] Cut110  label="Ball Plate 1.1"
  Base = -> Cut109
  Tool = -> Fusion078
FEATURE [Drawing::FeatureViewAnnotation] Annotation002
  Font = Sans
  Rotation = 0
  Scale = 7
  ViewResult = <g transform="translate(10,10) rotate(0)">\n<text id="Annotation002"\n font-family="Sans"\n font-size="7"\n fill="#000000">\n<tspan x="0" dy="1em"></tspan>\n</text>\n</g>
  Visible = true
  X = 10
  Y = 10
FEATURE [Drawing::FeatureViewAnnotation] Annotation003
  Font = Sans
  Rotation = 0
  Scale = 7
  Text = Robot 0.X
  ViewResult = <g transform="translate(14,18) rotate(0)">\n<text id="Annotation003"\n font-family="Sans"\n font-size="7"\n fill="#000000">\n<tspan x="0" dy="1em">Robot 0.X</tspan>\n</text>\n</g>
  Visible = true
  X = 14
  Y = 18
FEATURE [Drawing::FeatureViewAnnotation] Annotation004
  Font = Sans
  Rotation = 0
  Scale = 7
  ViewResult = <g transform="translate(10,10) rotate(0)">\n<text id="Annotation004"\n font-family="Sans"\n font-size="7"\n fill="#000000">\n<tspan x="0" dy="1em"></tspan>\n</text>\n</g>
  Visible = true
  X = 10
  Y = 10
FEATURE [Drawing::FeatureViewAnnotation] Annotation005
  Font = Sans
  Rotation = 0
  Scale = 5
  Text = Robot 0.1 - AB added Gripper Mecanism to SB\'s Plates
  ViewResult = <g transform="translate(10,30) rotate(0)">\n<text id="Annotation005"\n font-family="Sans"\n font-size="5"\n fill="#000000">\n<tspan x="0" dy="1em">Robot 0.1 - AB added Gripper Mecanism to SB\'s Plates</tspan>\n</text>\n</g>
  Visible = true
  X = 10
  Y = 30
FEATURE [Drawing::FeatureViewAnnotation] Annotation006
  Font = Sans
  Rotation = 0
  Scale = 5
  Text = Robot 0.2 - Reduced tooth size on small gear
  ViewResult = <g transform="translate(10,40) rotate(0)">\n<text id="Annotation006"\n font-family="Sans"\n font-size="5"\n fill="#000000">\n<tspan x="0" dy="1em">Robot 0.2 - Reduced tooth size on small gear</tspan>\n<tspan x="0" dy="1em"></tspan>\n</text>\n</g>
  Visible = true
  X = 10
  Y = 40
FEATURE [Part::Cylinder] Cylinder029
  Angle = 360
  AttacherType = Attacher::AttachEngine3D
  Height = 10
  Placement = pos=(15,-15,-5) rot=(0,0,1;1.5708rad)
  Radius = 1.7
FEATURE [Part::Sphere] Sphere084  label="Mag Hole001"
  Angle1 = -90
  Angle2 = 90
  Angle3 = 360
  AttacherType = Attacher::AttachEngine3D
  Placement = pos=(15,-15,1.7) rot=(0,0,1;1.5708rad)
  Radius = 2.83
FEATURE [Part::Sphere] Sphere085  label="Mag Hole002"
  Angle1 = -90
  Angle2 = 90
  Angle3 = 360
  AttacherType = Attacher::AttachEngine3D
  Placement = pos=(15,15,1.7) rot=(0,0,1;3.14159rad)
  Radius = 2.83
FEATURE [Part::Sphere] Sphere086  label="Mag Hole 004"
  Angle1 = -90
  Angle2 = 90
  Angle3 = 360
  AttacherType = Attacher::AttachEngine3D
  Placement = pos=(3e-15,15,1.7) rot=(0,0,1;1.5708rad)
  Radius = 2.825
FEATURE [Part::Sphere] Sphere087  label="Mag Hole 005"
  Angle1 = -90
  Angle2 = 90
  Angle3 = 360
  AttacherType = Attacher::AttachEngine3D
  Placement = pos=(-15,2e-15,1.7) rot=(0,0,1;3.14159rad)
  Radius = 2.825
FEATURE [Part::Sphere] Sphere088  label="Mag Hole 006"
  Angle1 = -90
  Angle2 = 90
  Angle3 = 360
  AttacherType = Attacher::AttachEngine3D
  Placement = pos=(-3e-15,-15,1.7) rot=(0,0,-1;1.5708rad)
  Radius = 2.825
FEATURE [Part::Cylinder] Cylinder030
  Angle = 360
  AttacherType = Attacher::AttachEngine3D
  Height = 10
  Placement = pos=(15,15,-5) rot=(0,0,1;3.14159rad)
  Radius = 1.7
FEATURE [Part::Cylinder] Cylinder031
  Angle = 360
  AttacherType = Attacher::AttachEngine3D
  Height = 10
  Placement = pos=(3e-15,15,-5) rot=(0,0,1;1.5708rad)
  Radius = 1.7
FEATURE [Part::Cylinder] Cylinder032
  Angle = 360
  AttacherType = Attacher::AttachEngine3D
  Height = 10
  Placement = pos=(-15,6e-15,-5) rot=(0,0,1;3.14159rad)
  Radius = 1.7
FEATURE [Part::Cylinder] Cylinder033
  Angle = 360
  AttacherType = Attacher::AttachEngine3D
  Height = 10
  Placement = pos=(-9e-15,-15,-5) rot=(0,0,-1;1.5708rad)
  Radius = 1.7
FEATURE [Part::MultiFuse] Fusion103007
  Shapes = -> [Cylinder029,Sphere087,Sphere084,Sphere086,Sphere088,Cylinder032,Cylinder033,Sphere085,Cylinder031,Cylinder030]
FEATURE [Part::Cut] Cut111  label="Ball Plate with Extra Holes"
  Base = -> Cut110
  Tool = -> Fusion103007
FEATURE [Part::Cylinder] Cylinder034
  Angle = 360
  AttacherType = Attacher::AttachEngine3D
  Height = 4
  Placement = pos=(-9.75,-9.75,-3) rot=(0,0,1;0rad)
  Radius = 1.5
FEATURE [Part::Cylinder] Cylinder035
  Angle = 360
  AttacherType = Attacher::AttachEngine3D
  Height = 4
  Placement = pos=(9.75,9.75,-3) rot=(0,0,1;0rad)
  Radius = 1.5
FEATURE [Part::Cylinder] Cylinder036
  Angle = 360
  AttacherType = Attacher::AttachEngine3D
  Height = 4
  Placement = pos=(-9.75,9.75,-3) rot=(0,0,1;0rad)
  Radius = 1.5
FEATURE [Part::Cylinder] Cylinder037
  Angle = 360
  AttacherType = Attacher::AttachEngine3D
  Height = 4
  Placement = pos=(9.75,-9.75,-3) rot=(0,0,1;0rad)
  Radius = 1.5
FEATURE [Part::MultiFuse] Fusion103008
  Shapes = -> [Cylinder034,Cylinder037,Cylinder036,Cylinder035]
FEATURE [Part::Cut] Cut112  label="Ball Plate 1.2"
  Base = -> Cut111
  Tool = -> Fusion103008
FEATURE [Part::Cylinder] Cylinder038
  Angle = 360
  AttacherType = Attacher::AttachEngine3D
  Height = 4
  Placement = pos=(-9.75,-9.75,-3) rot=(0,0,1;0rad)
  Radius = 1.5
FEATURE [Part::Cylinder] Cylinder039
  Angle = 360
  AttacherType = Attacher::AttachEngine3D
  Height = 4
  Placement = pos=(9.75,-9.75,-3) rot=(0,0,1;0rad)
  Radius = 1.5
FEATURE [Part::Cylinder] Cylinder040
  Angle = 360
  AttacherType = Attacher::AttachEngine3D
  Height = 4
  Placement = pos=(-9.75,9.75,-3) rot=(0,0,1;0rad)
  Radius = 1.5
FEATURE [Part::Cylinder] Cylinder041
  Angle = 360
  AttacherType = Attacher::AttachEngine3D
  Height = 4
  Placement = pos=(9.75,9.75,-3) rot=(0,0,1;0rad)
  Radius = 1.5
FEATURE [Part::MultiFuse] Fusion103009
  Shapes = -> [Cylinder038,Cylinder041,Cylinder039,Cylinder040]
FEATURE [Part::Cut] Cut113  label="Nut Plate 1.2"
  Base = -> Cut106
  Tool = -> Fusion103009
FEATURE [Drawing::FeatureViewAnnotation] Annotation007
  Font = Sans
  Rotation = 0
  Scale = 7
  ViewResult = <g transform="translate(10,10) rotate(0)">\n<text id="Annotation007"\n font-family="Sans"\n font-size="7"\n fill="#000000">\n<tspan x="0" dy="1em"></tspan>\n</text>\n</g>
  Visible = true
  X = 10
  Y = 10
FEATURE [Drawing::FeatureViewAnnotation] Annotation008
  Font = Sans
  Rotation = 0
  Scale = 7
  ViewResult = <g transform="translate(10,10) rotate(0)">\n<text id="Annotation008"\n font-family="Sans"\n font-size="7"\n fill="#000000">\n<tspan x="0" dy="1em"></tspan>\n</text>\n</g>
  Visible = true
  X = 10
  Y = 10
FEATURE [Drawing::FeatureViewAnnotation] Annotation009
  Font = Sans
  Rotation = 0
  Scale = 5
  Text = Robot 0.3 Reduced size of tooth on big gear and added boss. Rotated 180
  ViewResult = <g transform="translate(10,50) rotate(0)">\n<text id="Annotation009"\n font-family="Sans"\n font-size="5"\n fill="#000000">\n<tspan x="0" dy="1em">Robot 0.3 Reduced size of tooth on big gear and added boss. Rotated 180</tspan>\n<tspan x="0" dy="1em"></tspan>\n<tspan x="0" dy="1em"></tspan>\n</text>\n</g>
  Visible = true
  X = 10
  Y = 50
FEATURE [Part::Feature] Fusion103010
  Placement = pos=(0,0,0) rot=(0,0,-1;1.5708rad)
  shape: bbox 21.7 x 6.7 x 10.95 mm, 18 faces, 2 solids (baked)
FEATURE [Part::Feature] Fusion103011
  Placement = pos=(0,0,0) rot=(0,0,1;3.14159rad)
  shape: bbox 6.7 x 21.7 x 10.95 mm, 18 faces, 2 solids (baked)
FEATURE [Part::Feature] Fusion103012
  Placement = pos=(0,0,0) rot=(0,0,1;1.5708rad)
  shape: bbox 21.7 x 6.7 x 10.95 mm, 18 faces, 2 solids (baked)
FEATURE [Part::Box] Box270  label="Square Nut Hole 025"
  AttacherType = Attacher::AttachEngine3D
  Height = 2
  Length = 5.8
  Placement = pos=(-2.9,2.9,2.1) rot=(1,0,0;3.14159rad)
  Width = 5.8
FEATURE [Part::Cylinder] Cylinder042
  Angle = 360
  AttacherType = Attacher::AttachEngine3D
  Height = 10
  Placement = pos=(0,0,6.7) rot=(1,0,0;3.14159rad)
  Radius = 1.7
FEATURE [Part::Box] Box271  label="Cube228"
  AttacherType = Attacher::AttachEngine3D
  Height = 5
  Length = 40
  Placement = pos=(-20,-20,-2) rot=(0,0,1;0rad)
  Width = 40
FEATURE [Part::Sphere] Sphere089
  Angle1 = -90
  Angle2 = 90
  Angle3 = 360
  AttacherType = Attacher::AttachEngine3D
  Placement = pos=(0,0,4.3) rot=(1,0,0;3.14159rad)
  Radius = 3.35
FEATURE [Part::Box] Box272  label="Cube229"
  AttacherType = Attacher::AttachEngine3D
  Height = 15
  Length = 19.5
  Placement = pos=(-9.75,-9.75,-14) rot=(0,0,1;0rad)
  Width = 19.5
FEATURE [Part::Box] Box273  label="Cube230"
  AttacherType = Attacher::AttachEngine3D
  Height = 15
  Length = 19.5
  Placement = pos=(-9.75,-9.75,-3) rot=(0,0,1;0rad)
  Width = 19.5
FEATURE [Part::Chamfer] Chamfer015  label="Octagon001"
  Base = -> Box273
  Edges = 4 edges r=4: [Edge1,Edge3,Edge5,Edge7]
FEATURE [Part::Box] Box274  label="Cube231"
  AttacherType = Attacher::AttachEngine3D
  Height = 10
  Length = 24
  Placement = pos=(-12,-12,2.1) rot=(0,0,1;0rad)
  Width = 24
FEATURE [Part::Box] Box275  label="Cube232"
  AttacherType = Attacher::AttachEngine3D
  Height = 14
  Length = 20
  Placement = pos=(-10,-10,0) rot=(0,0,1;0rad)
  Width = 20
FEATURE [Part::Cut] Cut116
  Base = -> Box274
  Tool = -> Box275
FEATURE [Part::Chamfer] Chamfer016  label="Glue Channel001"
  Base = -> Cut116
  Edges = 8 edges r=0.95: [Edge4,Edge5,Edge14,Edge16,Edge17,Edge18,Edge19,Edge20]
FEATURE [Part::Box] Box276  label="Cube233"
  AttacherType = Attacher::AttachEngine3D
  Height = 7
  Length = 5
  Placement = pos=(-5,0,-2) rot=(0,0,1;0rad)
  Width = 40
FEATURE [Part::Box] Box277  label="Cube234"
  AttacherType = Attacher::AttachEngine3D
  Height = 7
  Length = 10
  Placement = pos=(-15,6,-2) rot=(0,0,1;0rad)
  Width = 2
FEATURE [Part::Box] Box278  label="Cube235"
  AttacherType = Attacher::AttachEngine3D
  Height = 7
  Length = 10
  Placement = pos=(-15,10,-2) rot=(0,0,1;0rad)
  Width = 2
FEATURE [Part::Box] Box279  label="Cube236"
  AttacherType = Attacher::AttachEngine3D
  Height = 7
  Length = 10
  Placement = pos=(-15,25.4,-2) rot=(0,0,1;0rad)
  Width = 2
FEATURE [Part::Box] Box280  label="Cube237"
  AttacherType = Attacher::AttachEngine3D
  Height = 7
  Length = 10
  Placement = pos=(-15,34.6,-2) rot=(0,0,1;0rad)
  Width = 2
FEATURE [Part::Sphere] Sphere090
  Angle1 = -90
  Angle2 = 90
  Angle3 = 360
  AttacherType = Attacher::AttachEngine3D
  Placement = pos=(-7.5,6.5,0.5) rot=(0,0,1;0rad)
  Radius = 1.25
FEATURE [Part::Box] Box281  label="Chamfer Cube009"
  AttacherType = Attacher::AttachEngine3D
  Height = 10
  Length = 13
  Placement = pos=(-11.69,0,-1.19) rot=(0,-1,0;0.785398rad)
  Width = 40
FEATURE [Part::Sphere] Sphere091
  Angle1 = -90
  Angle2 = 90
  Angle3 = 360
  AttacherType = Attacher::AttachEngine3D
  Placement = pos=(-7.5,11.5,0.5) rot=(0,0,1;0rad)
  Radius = 1.25
FEATURE [Part::Sphere] Sphere092
  Angle1 = -90
  Angle2 = 90
  Angle3 = 360
  AttacherType = Attacher::AttachEngine3D
  Placement = pos=(-7.5,28,0.5) rot=(0,0,1;0rad)
  Radius = 1.5
FEATURE [Part::Sphere] Sphere093
  Angle1 = -90
  Angle2 = 90
  Angle3 = 360
  AttacherType = Attacher::AttachEngine3D
  Placement = pos=(-7.5,34,0.5) rot=(0,0,1;0rad)
  Radius = 1.5
FEATURE [Part::Box] Box282  label="Cube238"
  AttacherType = Attacher::AttachEngine3D
  Height = 7
  Length = 4
  Placement = pos=(-6,5,-2) rot=(0,0,1;0rad)
  Width = 1
FEATURE [Part::Box] Box283  label="Cube239"
  AttacherType = Attacher::AttachEngine3D
  Height = 7
  Length = 4
  Placement = pos=(-6,8,-2) rot=(0,0,1;0rad)
  Width = 2
FEATURE [Part::Box] Box284  label="Cube240"
  AttacherType = Attacher::AttachEngine3D
  Height = 7
  Length = 4
  Placement = pos=(-6,12,-2) rot=(0,0,1;0rad)
  Width = 1
FEATURE [Part::Box] Box285  label="Cube241"
  AttacherType = Attacher::AttachEngine3D
  Height = 7
  Length = 4
  Placement = pos=(-6,24.4,-2) rot=(0,0,1;0rad)
  Width = 1
FEATURE [Part::Box] Box286  label="Cube242"
  AttacherType = Attacher::AttachEngine3D
  Height = 7
  Length = 4
  Placement = pos=(-6,36.6,-2) rot=(0,0,1;0rad)
  Width = 1
FEATURE [Part::Box] Box287  label="Cube243"
  AttacherType = Attacher::AttachEngine3D
  Height = 7
  Length = 4
  Placement = pos=(-6,27.4,-2) rot=(0,0,1;0rad)
  Width = 7.2
FEATURE [Part::MultiFuse] Fusion103013  label="Extra Holes for Clips009"
  Shapes = -> [Box287,Box284,Box286,Box283,Box285,Box282]
FEATURE [Part::Box] Box288  label="Re-level Edge Clip Block018"
  AttacherType = Attacher::AttachEngine3D
  Height = 10
  Length = 20
  Placement = pos=(-19,-2,3) rot=(0,0,1;0rad)
  Width = 44
FEATURE [Part::Box] Box289  label="Re-level Edge Clip Block019"
  AttacherType = Attacher::AttachEngine3D
  Height = 10
  Length = 12
  Placement = pos=(-21.5,-2,-7) rot=(0,0,1;0rad)
  Width = 44
FEATURE [Part::Fuse] Fusion103014  label="Bumps009"
  Base = -> Sphere090
  Tool = -> Sphere091
FEATURE [Part::Fuse] Fusion103015  label="Holes009"
  Base = -> Sphere092
  Tool = -> Sphere093
FEATURE [Part::MultiFuse] Fusion103016
  Shapes = -> [Box276,Box277,Box278,Box279,Box280]
FEATURE [Part::Fuse] Fusion103017
  Base = -> Fusion103014
  Tool = -> Fusion103016
FEATURE [Part::Cut] Cut117
  Base = -> Fusion103017
  Tool = -> Fusion103015
FEATURE [Part::Cut] Cut118
  Base = -> Cut117
  Tool = -> Fusion103013
FEATURE [Part::Cut] Cut119
  Base = -> Cut118
  Tool = -> Box288
FEATURE [Part::Cut] Cut120
  Base = -> Cut119
  Tool = -> Box289
FEATURE [Part::Cut] Cut121  label="Edge Clips Master002"
  Base = -> Cut120
  Placement = pos=(-20,-20,0) rot=(0,0,1;0rad)
  Tool = -> Box281
FEATURE [Part::Box] Box290  label="Cube244"
  AttacherType = Attacher::AttachEngine3D
  Height = 7
  Length = 5
  Placement = pos=(-5,0,-2) rot=(0,0,1;0rad)
  Width = 40
FEATURE [Part::Box] Box291  label="Cube245"
  AttacherType = Attacher::AttachEngine3D
  Height = 7
  Length = 4
  Placement = pos=(-6,8,-2) rot=(0,0,1;0rad)
  Width = 2
FEATURE [Part::Box] Box292  label="Chamfer Cube010"
  AttacherType = Attacher::AttachEngine3D
  Height = 10
  Length = 13
  Placement = pos=(-11.69,0,-1.19) rot=(0,-1,0;0.785398rad)
  Width = 40
FEATURE [Part::Box] Box293  label="Cube246"
  AttacherType = Attacher::AttachEngine3D
  Height = 7
  Length = 10
  Placement = pos=(-15,6,-2) rot=(0,0,1;0rad)
  Width = 2
FEATURE [Part::Sphere] Sphere094
  Angle1 = -90
  Angle2 = 90
  Angle3 = 360
  AttacherType = Attacher::AttachEngine3D
  Placement = pos=(-7.5,11.5,0.5) rot=(0,0,1;0rad)
  Radius = 1.25
FEATURE [Part::Box] Box294  label="Cube247"
  AttacherType = Attacher::AttachEngine3D
  Height = 7
  Length = 4
  Placement = pos=(-6,27.4,-2) rot=(0,0,1;0rad)
  Width = 7.2
FEATURE [Part::Box] Box295  label="Cube248"
  AttacherType = Attacher::AttachEngine3D
  Height = 7
  Length = 4
  Placement = pos=(-6,12,-2) rot=(0,0,1;0rad)
  Width = 1
FEATURE [Part::Box] Box296  label="Cube249"
  AttacherType = Attacher::AttachEngine3D
  Height = 7
  Length = 4
  Placement = pos=(-6,24.4,-2) rot=(0,0,1;0rad)
  Width = 1
FEATURE [Part::Sphere] Sphere095
  Angle1 = -90
  Angle2 = 90
  Angle3 = 360
  AttacherType = Attacher::AttachEngine3D
  Placement = pos=(-7.5,6.5,0.5) rot=(0,0,1;0rad)
  Radius = 1.25
FEATURE [Part::Box] Box297  label="Cube250"
  AttacherType = Attacher::AttachEngine3D
  Height = 7
  Length = 4
  Placement = pos=(-6,36.6,-2) rot=(0,0,1;0rad)
  Width = 1
FEATURE [Part::Box] Box298  label="Cube251"
  AttacherType = Attacher::AttachEngine3D
  Height = 7
  Length = 10
  Placement = pos=(-15,10,-2) rot=(0,0,1;0rad)
  Width = 2
FEATURE [Part::Sphere] Sphere096
  Angle1 = -90
  Angle2 = 90
  Angle3 = 360
  AttacherType = Attacher::AttachEngine3D
  Placement = pos=(-7.5,34,0.5) rot=(0,0,1;0rad)
  Radius = 1.5
FEATURE [Part::Box] Box299  label="Cube252"
  AttacherType = Attacher::AttachEngine3D
  Height = 7
  Length = 4
  Placement = pos=(-6,5,-2) rot=(0,0,1;0rad)
  Width = 1
FEATURE [Part::MultiFuse] Fusion103019  label="Extra Holes for Clips010"
  Shapes = -> [Box294,Box295,Box297,Box291,Box296,Box299]
FEATURE [Part::Box] Box300  label="Re-level Edge Clip Block020"
  AttacherType = Attacher::AttachEngine3D
  Height = 10
  Length = 20
  Placement = pos=(-19,-2,3) rot=(0,0,1;0rad)
  Width = 44
FEATURE [Part::Box] Box301  label="Cube253"
  AttacherType = Attacher::AttachEngine3D
  Height = 7
  Length = 10
  Placement = pos=(-15,34.6,-2) rot=(0,0,1;0rad)
  Width = 2
FEATURE [Part::Box] Box302  label="Cube254"
  AttacherType = Attacher::AttachEngine3D
  Height = 7
  Length = 10
  Placement = pos=(-15,25.4,-2) rot=(0,0,1;0rad)
  Width = 2
FEATURE [Part::MultiFuse] Fusion103020
  Shapes = -> [Box290,Box293,Box298,Box302,Box301]
FEATURE [Part::Fuse] Fusion103021  label="Bumps010"
  Base = -> Sphere095
  Tool = -> Sphere094
FEATURE [Part::Fuse] Fusion103018
  Base = -> Fusion103021
  Tool = -> Fusion103020
FEATURE [Part::Sphere] Sphere097
  Angle1 = -90
  Angle2 = 90
  Angle3 = 360
  AttacherType = Attacher::AttachEngine3D
  Placement = pos=(-7.5,28,0.5) rot=(0,0,1;0rad)
  Radius = 1.5
FEATURE [Part::Fuse] Fusion103022  label="Holes010"
  Base = -> Sphere097
  Tool = -> Sphere096
FEATURE [Part::Box] Box303  label="Re-level Edge Clip Block021"
  AttacherType = Attacher::AttachEngine3D
  Height = 10
  Length = 12
  Placement = pos=(-21.5,-2,-7) rot=(0,0,1;0rad)
  Width = 44
FEATURE [Part::Cut] Cut122
  Base = -> Fusion103018
  Tool = -> Fusion103022
FEATURE [Part::Cut] Cut123
  Base = -> Cut122
  Tool = -> Fusion103019
FEATURE [Part::Cut] Cut124
  Base = -> Cut123
  Tool = -> Box300
FEATURE [Part::Cut] Cut125
  Base = -> Cut124
  Tool = -> Box303
FEATURE [Part::Cut] Cut126  label="Edge Clips007"
  Base = -> Cut125
  Placement = pos=(20,-20,0) rot=(0,0,1;1.5708rad)
  Tool = -> Box292
FEATURE [Part::Box] Box304  label="Re-level Edge Clip Block022"
  AttacherType = Attacher::AttachEngine3D
  Height = 10
  Length = 12
  Placement = pos=(-21.5,-2,-7) rot=(0,0,1;0rad)
  Width = 44
FEATURE [Part::Box] Box305  label="Cube255"
  AttacherType = Attacher::AttachEngine3D
  Height = 7
  Length = 4
  Placement = pos=(-6,36.6,-2) rot=(0,0,1;0rad)
  Width = 1
FEATURE [Part::Box] Box306  label="Cube256"
  AttacherType = Attacher::AttachEngine3D
  Height = 7
  Length = 10
  Placement = pos=(-15,10,-2) rot=(0,0,1;0rad)
  Width = 2
FEATURE [Part::Box] Box307  label="Cube257"
  AttacherType = Attacher::AttachEngine3D
  Height = 7
  Length = 10
  Placement = pos=(-15,25.4,-2) rot=(0,0,1;0rad)
  Width = 2
FEATURE [Part::Box] Box308  label="Re-level Edge Clip Block023"
  AttacherType = Attacher::AttachEngine3D
  Height = 10
  Length = 20
  Placement = pos=(-19,-2,3) rot=(0,0,1;0rad)
  Width = 44
FEATURE [Part::Box] Box309  label="Cube258"
  AttacherType = Attacher::AttachEngine3D
  Height = 7
  Length = 10
  Placement = pos=(-15,34.6,-2) rot=(0,0,1;0rad)
  Width = 2
FEATURE [Part::Sphere] Sphere098
  Angle1 = -90
  Angle2 = 90
  Angle3 = 360
  AttacherType = Attacher::AttachEngine3D
  Placement = pos=(-7.5,34,0.5) rot=(0,0,1;0rad)
  Radius = 1.5
FEATURE [Part::Sphere] Sphere099
  Angle1 = -90
  Angle2 = 90
  Angle3 = 360
  AttacherType = Attacher::AttachEngine3D
  Placement = pos=(-7.5,28,0.5) rot=(0,0,1;0rad)
  Radius = 1.5
FEATURE [Part::Fuse] Fusion103023  label="Holes011"
  Base = -> Sphere099
  Tool = -> Sphere098
FEATURE [Part::Box] Box310  label="Cube259"
  AttacherType = Attacher::AttachEngine3D
  Height = 7
  Length = 4
  Placement = pos=(-6,5,-2) rot=(0,0,1;0rad)
  Width = 1
FEATURE [Part::Box] Box311  label="Cube260"
  AttacherType = Attacher::AttachEngine3D
  Height = 7
  Length = 4
  Placement = pos=(-6,24.4,-2) rot=(0,0,1;0rad)
  Width = 1
FEATURE [Part::Sphere] Sphere100
  Angle1 = -90
  Angle2 = 90
  Angle3 = 360
  AttacherType = Attacher::AttachEngine3D
  Placement = pos=(-7.5,11.5,0.5) rot=(0,0,1;0rad)
  Radius = 1.25
FEATURE [Part::Box] Box312  label="Cube261"
  AttacherType = Attacher::AttachEngine3D
  Height = 7
  Length = 4
  Placement = pos=(-6,12,-2) rot=(0,0,1;0rad)
  Width = 1
FEATURE [Part::Box] Box313  label="Chamfer Cube011"
  AttacherType = Attacher::AttachEngine3D
  Height = 10
  Length = 13
  Placement = pos=(-11.69,0,-1.19) rot=(0,-1,0;0.785398rad)
  Width = 40
FEATURE [Part::Sphere] Sphere101
  Angle1 = -90
  Angle2 = 90
  Angle3 = 360
  AttacherType = Attacher::AttachEngine3D
  Placement = pos=(-7.5,6.5,0.5) rot=(0,0,1;0rad)
  Radius = 1.25
FEATURE [Part::Fuse] Fusion103024  label="Bumps011"
  Base = -> Sphere101
  Tool = -> Sphere100
FEATURE [Part::Box] Box314  label="Cube262"
  AttacherType = Attacher::AttachEngine3D
  Height = 7
  Length = 5
  Placement = pos=(-5,0,-2) rot=(0,0,1;0rad)
  Width = 40
FEATURE [Part::Box] Box315  label="Cube263"
  AttacherType = Attacher::AttachEngine3D
  Height = 7
  Length = 4
  Placement = pos=(-6,27.4,-2) rot=(0,0,1;0rad)
  Width = 7.2
FEATURE [Part::Box] Box316  label="Cube264"
  AttacherType = Attacher::AttachEngine3D
  Height = 7
  Length = 4
  Placement = pos=(-6,8,-2) rot=(0,0,1;0rad)
  Width = 2
FEATURE [Part::MultiFuse] Fusion103025  label="Extra Holes for Clips011"
  Shapes = -> [Box315,Box312,Box305,Box316,Box311,Box310]
FEATURE [Part::Box] Box317  label="Cube265"
  AttacherType = Attacher::AttachEngine3D
  Height = 7
  Length = 10
  Placement = pos=(-15,6,-2) rot=(0,0,1;0rad)
  Width = 2
FEATURE [Part::MultiFuse] Fusion103026
  Shapes = -> [Box314,Box317,Box306,Box307,Box309]
FEATURE [Part::Fuse] Fusion103027
  Base = -> Fusion103024
  Tool = -> Fusion103026
FEATURE [Part::Cut] Cut128
  Base = -> Fusion103027
  Tool = -> Fusion103023
FEATURE [Part::Cut] Cut114
  Base = -> Cut128
  Tool = -> Fusion103025
FEATURE [Part::Cut] Cut129
  Base = -> Cut114
  Tool = -> Box308
FEATURE [Part::Cut] Cut115
  Base = -> Cut129
  Tool = -> Box304
FEATURE [Part::Cut] Cut127  label="Edge Clips008"
  Base = -> Cut115
  Placement = pos=(20,20,0) rot=(0,0,1;3.14159rad)
  Tool = -> Box313
FEATURE [Part::Box] Box318  label="Re-level Edge Clip Block024"
  AttacherType = Attacher::AttachEngine3D
  Height = 10
  Length = 12
  Placement = pos=(-21.5,-2,-7) rot=(0,0,1;0rad)
  Width = 44
FEATURE [Part::Box] Box319  label="Cube266"
  AttacherType = Attacher::AttachEngine3D
  Height = 7
  Length = 10
  Placement = pos=(-15,10,-2) rot=(0,0,1;0rad)
  Width = 2
FEATURE [Part::Box] Box320  label="Cube267"
  AttacherType = Attacher::AttachEngine3D
  Height = 7
  Length = 4
  Placement = pos=(-6,12,-2) rot=(0,0,1;0rad)
  Width = 1
FEATURE [Part::Box] Box321  label="Chamfer Cube012"
  AttacherType = Attacher::AttachEngine3D
  Height = 10
  Length = 13
  Placement = pos=(-11.69,0,-1.19) rot=(0,-1,0;0.785398rad)
  Width = 40
FEATURE [Part::Sphere] Sphere102
  Angle1 = -90
  Angle2 = 90
  Angle3 = 360
  AttacherType = Attacher::AttachEngine3D
  Placement = pos=(-7.5,6.5,0.5) rot=(0,0,1;0rad)
  Radius = 1.25
FEATURE [Part::Box] Box322  label="Cube268"
  AttacherType = Attacher::AttachEngine3D
  Height = 7
  Length = 5
  Placement = pos=(-5,0,-2) rot=(0,0,1;0rad)
  Width = 40
FEATURE [Part::Box] Box323  label="Cube269"
  AttacherType = Attacher::AttachEngine3D
  Height = 7
  Length = 4
  Placement = pos=(-6,27.4,-2) rot=(0,0,1;0rad)
  Width = 7.2
FEATURE [Part::Box] Box324  label="Cube270"
  AttacherType = Attacher::AttachEngine3D
  Height = 7
  Length = 4
  Placement = pos=(-6,8,-2) rot=(0,0,1;0rad)
  Width = 2
FEATURE [Part::Box] Box325  label="Cube271"
  AttacherType = Attacher::AttachEngine3D
  Height = 7
  Length = 10
  Placement = pos=(-15,6,-2) rot=(0,0,1;0rad)
  Width = 2
FEATURE [Part::Sphere] Sphere103
  Angle1 = -90
  Angle2 = 90
  Angle3 = 360
  AttacherType = Attacher::AttachEngine3D
  Placement = pos=(-7.5,28,0.5) rot=(0,0,1;0rad)
  Radius = 1.5
FEATURE [Part::Box] Box326  label="Cube272"
  AttacherType = Attacher::AttachEngine3D
  Height = 7
  Length = 4
  Placement = pos=(-6,5,-2) rot=(0,0,1;0rad)
  Width = 1
FEATURE [Part::Box] Box327  label="Cube273"
  AttacherType = Attacher::AttachEngine3D
  Height = 7
  Length = 4
  Placement = pos=(-6,24.4,-2) rot=(0,0,1;0rad)
  Width = 1
FEATURE [Part::Sphere] Sphere104
  Angle1 = -90
  Angle2 = 90
  Angle3 = 360
  AttacherType = Attacher::AttachEngine3D
  Placement = pos=(-7.5,11.5,0.5) rot=(0,0,1;0rad)
  Radius = 1.25
FEATURE [Part::Box] Box328  label="Re-level Edge Clip Block025"
  AttacherType = Attacher::AttachEngine3D
  Height = 10
  Length = 20
  Placement = pos=(-19,-2,3) rot=(0,0,1;0rad)
  Width = 44
FEATURE [Part::Box] Box329  label="Cube274"
  AttacherType = Attacher::AttachEngine3D
  Height = 7
  Length = 10
  Placement = pos=(-15,34.6,-2) rot=(0,0,1;0rad)
  Width = 2
FEATURE [Part::Box] Box330  label="Cube275"
  AttacherType = Attacher::AttachEngine3D
  Height = 7
  Length = 10
  Placement = pos=(-15,25.4,-2) rot=(0,0,1;0rad)
  Width = 2
FEATURE [Part::MultiFuse] Fusion103030
  Shapes = -> [Box322,Box325,Box319,Box330,Box329]
FEATURE [Part::Box] Box331  label="Cube276"
  AttacherType = Attacher::AttachEngine3D
  Height = 7
  Length = 4
  Placement = pos=(-6,36.6,-2) rot=(0,0,1;0rad)
  Width = 1
FEATURE [Part::MultiFuse] Fusion103029  label="Extra Holes for Clips012"
  Shapes = -> [Box323,Box320,Box331,Box324,Box327,Box326]
FEATURE [Part::Fuse] Fusion103032  label="Bumps012"
  Base = -> Sphere102
  Tool = -> Sphere104
FEATURE [Part::Fuse] Fusion103028
  Base = -> Fusion103032
  Tool = -> Fusion103030
FEATURE [Part::Sphere] Sphere105
  Angle1 = -90
  Angle2 = 90
  Angle3 = 360
  AttacherType = Attacher::AttachEngine3D
  Placement = pos=(-7.5,34,0.5) rot=(0,0,1;0rad)
  Radius = 1.5
FEATURE [Part::Fuse] Fusion103031  label="Holes012"
  Base = -> Sphere103
  Tool = -> Sphere105
FEATURE [Part::Cut] Cut134
  Base = -> Fusion103028
  Tool = -> Fusion103031
FEATURE [Part::Cut] Cut130
  Base = -> Cut134
  Tool = -> Fusion103029
FEATURE [Part::Cut] Cut131
  Base = -> Cut130
  Tool = -> Box328
FEATURE [Part::Cut] Cut132
  Base = -> Cut131
  Tool = -> Box318
FEATURE [Part::Cut] Cut133  label="Edge Clips009"
  Base = -> Cut132
  Placement = pos=(-20,20,0) rot=(0,0,-1;1.5708rad)
  Tool = -> Box321
FEATURE [Part::Box] Box332  label="Cube277"
  AttacherType = Attacher::AttachEngine3D
  Height = 10
  Length = 10
  Placement = pos=(4,-26,1) rot=(0.205904,-0.974848,-0.085288;0.803573rad)
  Width = 15
FEATURE [Part::Box] Box333  label="Cube278"
  AttacherType = Attacher::AttachEngine3D
  Height = 10
  Length = 10
  Placement = pos=(-26,-4,1) rot=(-0.273007,-0.419215,-0.865867;1.78566rad)
  Width = 15
FEATURE [Part::Box] Box334  label="Cube279"
  AttacherType = Attacher::AttachEngine3D
  Height = 10
  Length = 10
  Placement = pos=(-4,26,1) rot=(0.381439,0.080566,0.920876;3.07487rad)
  Width = 15
FEATURE [Part::Box] Box335  label="Cube280"
  AttacherType = Attacher::AttachEngine3D
  Height = 10
  Length = 10
  Placement = pos=(26,4,1) rot=(0.442189,-0.287968,0.849437;1.66134rad)
  Width = 15
FEATURE [Part::MultiFuse] Fusion103033  label="Glue Dents002"
  Shapes = -> [Box332,Box333,Box334,Box335]
FEATURE [Part::MultiFuse] Fusion103034  label="Edge Clips Fusion002"
  Shapes = -> [Cut133,Cut121,Cut126,Cut127]
FEATURE [Part::MultiFuse] Fusion103035
  Placement = pos=(-15,-15,0) rot=(0,0,1;0rad)
  Shapes = -> [Box270,Cylinder042,Sphere089]
FEATURE [Part::Box] Box336  label="Square Nut Hole 026"
  AttacherType = Attacher::AttachEngine3D
  Height = 2
  Length = 5.8
  Placement = pos=(-2.9,2.9,2.1) rot=(1,0,0;3.14159rad)
  Width = 5.8
FEATURE [Part::Cylinder] Cylinder043
  Angle = 360
  AttacherType = Attacher::AttachEngine3D
  Height = 10
  Placement = pos=(0,0,6.7) rot=(1,0,0;3.14159rad)
  Radius = 1.7
FEATURE [Part::Sphere] Sphere106
  Angle1 = -90
  Angle2 = 90
  Angle3 = 360
  AttacherType = Attacher::AttachEngine3D
  Placement = pos=(0,0,4.3) rot=(1,0,0;3.14159rad)
  Radius = 3.35
FEATURE [Part::MultiFuse] Fusion103036
  Placement = pos=(-15,0,0) rot=(0,0,1;0rad)
  Shapes = -> [Box336,Cylinder043,Sphere106]
FEATURE [Part::Fuse] Fusion103037
  Base = -> Fusion103035
  Tool = -> Fusion103036
FEATURE [Part::MultiFuse] Fusion103038  label="Nut Holes001"
  Shapes = -> [Fusion103037,Fusion103012,Fusion103011,Fusion103010]
FEATURE [Part::Fuse] Fusion103039  label="Cube with Edge Clips001"
  Base = -> Box271
  Tool = -> Fusion103034
FEATURE [Part::Cut] Cut135
  Base = -> Fusion103039
  Tool = -> Fusion103033
FEATURE [Part::Cut] Cut136
  Base = -> Cut135
  Tool = -> Fusion103038
FEATURE [Part::Cut] Cut137
  Base = -> Cut136
  Tool = -> Chamfer016
FEATURE [Part::Cut] Cut138
  Base = -> Cut137
  Tool = -> Chamfer015
FEATURE [Part::Cut] Cut139  label="Nut Plate 1.003"
  Base = -> Cut138
  Tool = -> Box272
FEATURE [Part::Cylinder] Cylinder044
  Angle = 360
  AttacherType = Attacher::AttachEngine3D
  Height = 4
  Placement = pos=(-9.75,-9.75,-3) rot=(0,0,1;0rad)
  Radius = 1.5
FEATURE [Part::Cylinder] Cylinder045
  Angle = 360
  AttacherType = Attacher::AttachEngine3D
  Height = 4
  Placement = pos=(9.75,-9.75,-3) rot=(0,0,1;0rad)
  Radius = 1.5
FEATURE [Part::Cylinder] Cylinder046
  Angle = 360
  AttacherType = Attacher::AttachEngine3D
  Height = 4
  Placement = pos=(-9.75,9.75,-3) rot=(0,0,1;0rad)
  Radius = 1.5
FEATURE [Part::Cylinder] Cylinder047
  Angle = 360
  AttacherType = Attacher::AttachEngine3D
  Height = 4
  Placement = pos=(9.75,9.75,-3) rot=(0,0,1;0rad)
  Radius = 1.5
FEATURE [Part::MultiFuse] Fusion103040
  Shapes = -> [Cylinder044,Cylinder047,Cylinder045,Cylinder046]
FEATURE [Part::Cut] Cut140  label="Nut Plate 1.004"
  Base = -> Cut139
  Placement = pos=(0,0,-6) rot=(0,0,1;0rad)
  Tool = -> Fusion103040
FEATURE [App::DocumentObjectGroup] Group003  label="Cube-components"
  Group = -> [Cut112,Cut113]
FEATURE [Part::Box] Box404  label="Cube334"
  AttacherType = Attacher::AttachEngine3D
  Height = 14
  Length = 5
  Placement = pos=(20,20,-7) rot=(0,0,1;0rad)
  Width = 5
FEATURE [Part::Box] Box405  label="Cube335"
  AttacherType = Attacher::AttachEngine3D
  Height = 13
  Length = 15
  Placement = pos=(10,10,2) rot=(0,0,1;0rad)
  Width = 15
FEATURE [Part::FeaturePython] BevelGear001  # WARN: FeaturePython — macro-defined, semantics opaque (R4)
  Placement = pos=(7.81,7.81,10.5) rot=(0.862856,-0.357407,-0.357407;1.71777rad)
  backlash = 0
  beta = 0
  clearance = 0.1
  height = 3
  m = 1
  numpoints = 6
  pitch_angle = 45
  pressure_angle = 20
  reset_origin = true
  teeth = 10
FEATURE [Part::Cylinder] Cylinder054
  Angle = 360
  AttacherType = Attacher::AttachEngine3D
  Height = 22
  Radius = 11
FEATURE [Part::Cone] Cone
  Angle = 360
  AttacherType = Attacher::AttachEngine3D
  Height = 9
  Placement = pos=(8.52,8.52,10.5) rot=(0.862856,-0.357407,-0.357407;1.71777rad)
  Radius1 = 8
  Radius2 = 1.5
FEATURE [Part::Box] Box406004  label="Square Nut Hole 029"
  AttacherType = Attacher::AttachEngine3D
  Height = 2
  Length = 5.8
  Placement = pos=(15.7,19.8,7.6) rot=(0.862856,-0.357407,-0.357407;1.71777rad)
  Width = 14.8
FEATURE [Part::Box] Box406005  label="60mm-high"
  AttacherType = Attacher::AttachEngine3D
  Height = 60
  Length = 10
  Placement = pos=(-29,12,-3) rot=(0,0,1;0rad)
  Width = 10
FEATURE [Part::Cylinder] Cylinder057  label="small-gear-hub"
  Angle = 360
  AttacherType = Attacher::AttachEngine3D
  Height = 5
  Placement = pos=(7.5,7.5,10.5) rot=(0.862856,-0.357407,-0.357407;1.71777rad)
  Radius = 4
FEATURE [Part::Feature] Shape001  label="M3-hex-cavity"
  Placement = pos=(-0.5,-0.5,10.5) rot=(0.281085,0.678598,0.678598;2.59356rad)
  shape: bbox 11.56 x 11.56 x 5.5 mm, 8 faces (baked)
FEATURE [Part::Cylinder] Cylinder058  label="M3-screw-drive001"
  Angle = 360
  AttacherType = Attacher::AttachEngine3D
  Height = 33
  Placement = pos=(23.37,23.37,10.5) rot=(0.862856,-0.357407,-0.357407;1.71777rad)
  Radius = 1.75
FEATURE [Part::Box] Box406007  label="Cube338"
  AttacherType = Attacher::AttachEngine3D
  Height = 14
  Length = 14
  Placement = pos=(1.78,11.68,2) rot=(0,0,-1;0.785398rad)
  Width = 10
FEATURE [Part::Box] Box406008  label="slot-1"
  AttacherType = Attacher::AttachEngine3D
  Height = 36
  Length = 10.5
  Placement = pos=(10.22,17.65,0) rot=(0,0,-1;0.785398rad)
  Width = 28
FEATURE [Part::Cylinder] Cylinder059  label="M3-screw-drive002"
  Angle = 360
  AttacherType = Attacher::AttachEngine3D
  Height = 80
  Placement = pos=(26.8701,26.8701,10.5) rot=(0.862856,-0.357407,-0.357407;1.71777rad)
  Radius = 2.15
FEATURE [Part::Cylinder] Cylinder066  label="M3-screw-drive003"
  Angle = 360
  AttacherType = Attacher::AttachEngine3D
  Height = 33
  Placement = pos=(26.8701,26.8701,10.5) rot=(0.862856,-0.357407,-0.357407;1.71777rad)
  Radius = 1.75
FEATURE [Part::MultiFuse] Fusion103077010  label="finger-cavity"
  Shapes = -> [Cylinder066,Box406004]
FEATURE [Part::Box] Box406015  label="motor-clamp-0"
  AttacherType = Attacher::AttachEngine3D
  Height = 31
  Length = 53.28
  Placement = pos=(-13.8876,-23.7871,2) rot=(0,0,1;0.785398rad)
  Width = 14
FEATURE [Part::Box] Box406016  label="clamp-slot"
  AttacherType = Attacher::AttachEngine3D
  Height = 32
  Length = 49
  Placement = pos=(17.31,-15.9,17) rot=(0,0,1;2.35619rad)
  Width = 2
FEATURE [Part::Cylinder] Cylinder067
  Angle = 360
  AttacherType = Attacher::AttachEngine3D
  Height = 26
  Placement = pos=(0,0,20) rot=(0,0,1;0rad)
  Radius = 6.25
FEATURE [Part::Box] Box406017  label="gearbox001"
  AttacherType = Attacher::AttachEngine3D
  Height = 28
  Length = 16
  Placement = pos=(-8,-5.25,18) rot=(0,0,1;0rad)
  Width = 10.5
FEATURE [Part::MultiCommon] Common004  label="motor-hole"
  Placement = pos=(0,0,0) rot=(0,0,-1;0.785398rad)
  Shapes = -> [Cylinder067,Box406017]
FEATURE [Part::Cylinder] Cylinder068
  Angle = 360
  AttacherType = Attacher::AttachEngine3D
  Height = 12
  Placement = pos=(0,0,40) rot=(0.281085,0.678598,0.678598;2.59356rad)
  Radius = 1.2
FEATURE [Part::Cylinder] Cylinder069
  Angle = 360
  AttacherType = Attacher::AttachEngine3D
  Height = 12
  Placement = pos=(8.48528,8.48528,40) rot=(0.281085,0.678598,0.678598;2.59356rad)
  Radius = 2.2
FEATURE [Part::MultiFuse] Fusion103077013  label="M2-screw001"
  Placement = pos=(2,-14,0) rot=(0,0,1;0rad)
  Shapes = -> [Cylinder068,Cylinder069]
FEATURE [Part::Feature] Fusion103077013001
  Placement = pos=(-2e-15,-13,30) rot=(-0.281085,0.678598,0.678598;3.68962rad)
  shape: bbox 19.37 x 19.37 x 4.4 mm, 5 faces (baked)
FEATURE [Part::Cylinder] Cylinder070
  Angle = 360
  AttacherType = Attacher::AttachEngine3D
  Height = 12
  Placement = pos=(0,0,12) rot=(0,0,1;0rad)
  Radius = 2.2
FEATURE [Part::Cylinder] Cylinder071
  Angle = 360
  AttacherType = Attacher::AttachEngine3D
  Height = 12
  Radius = 1.2
FEATURE [Part::Cylinder] Cylinder072  label="M3-cap-screw-head"
  Angle = 360
  AttacherType = Attacher::AttachEngine3D
  Height = 10
  Placement = pos=(0,15,4) rot=(0,0,1;0rad)
  Radius = 3
FEATURE [Part::FeaturePython] BevelGear002  # WARN: FeaturePython — macro-defined, semantics opaque (R4)
  Placement = pos=(0,0,2.5) rot=(0,0,1;0rad)
  backlash = 0
  beta = 0
  clearance = 0.1
  height = 3
  m = 1
  numpoints = 6
  pitch_angle = 45
  pressure_angle = 20
  reset_origin = true
  teeth = 20
FEATURE [Part::MultiCommon] Common  label="big-gear-a"
  Shapes = -> [BevelGear002,Cylinder054]
FEATURE [Part::MultiCommon] Common005  label="small-gear-1"
  Shapes = -> [Cone,BevelGear001]
FEATURE [Part::MultiFuse] Fusion103077013004005  label="small-gear-2"
  Shapes = -> [Common005,Cylinder057]
FEATURE [Part::MultiFuse] Fusion103077013004006  label="small-gear-cavity"
  Shapes = -> [Cylinder058,Shape001]
FEATURE [Part::Cut] Cut173011005  label="small-gear"
  Base = -> Fusion103077013004005
  Tool = -> Fusion103077013004006
FEATURE [Part::Cylinder] Cylinder073  label="motor-bulge"
  Angle = 360
  AttacherType = Attacher::AttachEngine3D
  Height = 20
  Placement = pos=(0,0,23) rot=(0,0,1;0rad)
  Radius = 9
FEATURE [Part::Cylinder] Cylinder074  label="big-gear-clearance"
  Angle = 360
  AttacherType = Attacher::AttachEngine3D
  Height = 22
  Radius = 12
FEATURE [Part::Cylinder] Cylinder075  label="M3-cap-screw-head001"
  Angle = 360
  AttacherType = Attacher::AttachEngine3D
  Height = 10
  Placement = pos=(0,15,-6) rot=(0,0,1;0rad)
  Radius = 1.7
FEATURE [Part::MultiFuse] Fusion103077013004011  label="M3-cap-screw"
  Placement = pos=(0,0,5) rot=(0,0,1;0rad)
  Shapes = -> [Cylinder075,Cylinder072]
FEATURE [Part::Box] Box406019  label="motor-clamp-print-45"
  AttacherType = Attacher::AttachEngine3D
  Height = 30
  Length = 16.46
  Placement = pos=(-19.23,2.77,22) rot=(0.707107,0.707107,0;1.5708rad)
  Width = 16.46
FEATURE [Part::Feature] Box406008001  label="slot-2"
  Placement = pos=(-10.22,-17.65,0) rot=(0,0,1;2.35619rad)
  shape: bbox 27.22 x 27.22 x 36 mm, 6 faces (baked)
FEATURE [Part::Box] Box406008002  label="Cube339"
  AttacherType = Attacher::AttachEngine3D
  Height = 24
  Length = 23
  Placement = pos=(-1.06066,-15.2,-2) rot=(0,0,1;0.785398rad)
  Width = 20
FEATURE [Part::MultiFuse] Fusion103077013004013  label="finger-slots"
  Shapes = -> [Box406008,Box406008001]
FEATURE [Part::Chamfer] Chamfer024  label="motor-clamp-1"
  Base = -> Box406015
  Edges = 2 edges r=12: [Edge2,Edge6]
FEATURE [Part::Chamfer] Chamfer025  label="motor-clamp-2"
  Base = -> Chamfer024
  Edges = 4 edges r=2: [Edge1,Edge4,Edge5,Edge14]
FEATURE [Part::MultiFuse] Fusion103077013004016  label="motor-clamp-3"
  Shapes = -> [Chamfer025,Cylinder073]
FEATURE [Part::Box] Box406008003  label="Cube340"
  AttacherType = Attacher::AttachEngine3D
  Height = 6
  Length = 15
  Placement = pos=(-5,10,2) rot=(0,0,1;0rad)
  Width = 10
FEATURE [Part::Cut] Cut173011007  label="screw-land-1"
  Base = -> Box406008003
  Tool = -> Cylinder074
FEATURE [Part::Cone] Cone001
  Angle = 360
  AttacherType = Attacher::AttachEngine3D
  Height = 9
  Placement = pos=(8.52,8.52,10.5) rot=(0.862856,-0.357407,-0.357407;1.71777rad)
  Radius1 = 9
  Radius2 = 2.5
FEATURE [Part::Box] Box406008004  label="gearbox004"
  AttacherType = Attacher::AttachEngine3D
  Height = 9
  Length = 12
  Placement = pos=(-6,-5,0) rot=(0,0,1;0rad)
  Width = 10
FEATURE [Part::Cylinder] Cylinder076  label="boss002"
  Angle = 360
  AttacherType = Attacher::AttachEngine3D
  Height = 1
  Placement = pos=(0,0,-1) rot=(0,0,1;0rad)
  Radius = 2
FEATURE [Part::Cylinder] Cylinder077
  Angle = 360
  AttacherType = Attacher::AttachEngine3D
  Height = 15
  Placement = pos=(0,0,9) rot=(0,0,1;0rad)
  Radius = 6
FEATURE [Part::Box] Box406008005  label="gearbox005"
  AttacherType = Attacher::AttachEngine3D
  Height = 27
  Length = 16
  Placement = pos=(-8,-5,0) rot=(0,0,1;0rad)
  Width = 10
FEATURE [Part::MultiCommon] Common001  label="motor002"
  Shapes = -> [Cylinder077,Box406008005]
FEATURE [Part::Cylinder] Cylinder078  label="shaft-002"
  Angle = 360
  AttacherType = Attacher::AttachEngine3D
  Height = 10
  Placement = pos=(0,0,-10) rot=(0,0,1;0rad)
  Radius = 1.5
FEATURE [Part::Box] Box406008006  label="Cube341"
  AttacherType = Attacher::AttachEngine3D
  Height = 12
  Length = 10
  Placement = pos=(-5,1,-11) rot=(0,0,1;0rad)
  Width = 10
FEATURE [Part::Cut] Cut001  label="shaft002"
  Base = -> Cylinder078
  Tool = -> Box406008006
FEATURE [Part::MultiFuse] Fusion103077013004017004  label="motor-assembled"
  Placement = pos=(0,0,20.5) rot=(0,0,-1;0.785398rad)
  Shapes = -> [Box406008004,Cylinder076,Common001,Cut001]
FEATURE [Part::Cylinder] Cylinder079  label="shaft-003"
  Angle = 360
  AttacherType = Attacher::AttachEngine3D
  Height = 10
  Placement = pos=(0,0,-2) rot=(0,0,1;0rad)
  Radius = 1.75
FEATURE [Part::Box] Box406008007  label="Cube342"
  AttacherType = Attacher::AttachEngine3D
  Height = 12
  Length = 10
  Placement = pos=(-5,1.125,-2) rot=(0,0,1;0rad)
  Width = 10
FEATURE [Part::Cut] Cut173011011  label="motor-shaft"
  Base = -> Cylinder079
  Tool = -> Box406008007
FEATURE [Part::Cut] Cut173011012  label="big-gear-2"
  Base = -> Common
  Tool = -> Cut173011011
FEATURE [Part::Box] Box406008008  label="Cube343"
  AttacherType = Attacher::AttachEngine3D
  Height = 2
  Length = 19
  Placement = pos=(-9.5,-9.5,0) rot=(0,0,1;0rad)
  Width = 19
FEATURE [Part::Cylinder] Cylinder080  label="Cylinder078"
  Angle = 360
  AttacherType = Attacher::AttachEngine3D
  Height = 10
  Placement = pos=(0,0,-4) rot=(0,0,1;0rad)
  Radius = 1.8
FEATURE [Part::Cut] Cut173011013  label="filler-plate-1"
  Base = -> Box406008008
  Tool = -> Cylinder080
FEATURE [Part::Chamfer] Chamfer026  label="filler-plate-2"
  Base = -> Cut173011013
  Edges = 1 edges r=0.5: [Edge10]
FEATURE [Part::Chamfer] Chamfer027  label="filler-plate"
  Base = -> Chamfer026
  Edges = 4 edges r=0.5: [Edge10,Edge11,Edge13,Edge15]
FEATURE [Part::Box] Box406008009  label="Cube344"
  AttacherType = Attacher::AttachEngine3D
  Height = 3
  Length = 6
  Placement = pos=(19,19,-7) rot=(0,0,1;0rad)
  Width = 6
FEATURE [Part::Chamfer] Chamfer029  label="grip-1"
  Base = -> Box406008009
  Edges = 2 edges r=1: [Edge2,Edge10]
FEATURE [Part::Chamfer] Chamfer030  label="grip-2"
  Base = -> Chamfer029
  Edges = 1 edges r=1: [Edge1]
FEATURE [Part::Cut] Cut173011016  label="mounting-plate"
  Base = -> Cut139
  Placement = pos=(0,0,0) rot=(1,0,0;3.14159rad)
  Tool = -> Fusion103040
FEATURE [Part::Chamfer] Chamfer032  label="big-gear"
  Base = -> Cut173011012
  Edges = 3 edges r=0.5: [Edge124,Edge125,Edge126]
FEATURE [Part::Feature] Shape002  label="M3-head-cover"
  Placement = pos=(5,5,10.5) rot=(0.862856,-0.357407,-0.357407;1.71777rad)
  shape: bbox 5.347 x 5.347 x 5.25 mm, 8 faces (baked)
FEATURE [Part::Cylinder] Cylinder081  label="M3-screw-drive004"
  Angle = 360
  AttacherType = Attacher::AttachEngine3D
  Height = 20
  Placement = pos=(23.4,23.4,10.5) rot=(0.862856,-0.357407,-0.357407;1.71777rad)
  Radius = 4.5
FEATURE [Part::Feature] Cylinder081001
  Placement = pos=(-23.4,-23.4,10.5) rot=(0.281085,0.678598,0.678598;2.59356rad)
  shape: bbox 20.51 x 20.51 x 9 mm, 3 faces (baked)
FEATURE [Part::MultiFuse] Fusion103077013004017006  label="nut-cavities"
  Shapes = -> [Cylinder081001,Cylinder081]
FEATURE [App::DocumentObjectGroup] Group001  label="Old"
  Group = -> [Cut008,Cut009,Cut015,Cut018,Fusion021,Fusion023,Group,Cut039,Cut028,Cut032,Cut033,Fusion048,Cylinder068,Cylinder069,Cylinder071,Cylinder070,Fusion103077013004017006]
FEATURE [Part::Chamfer] Chamfer  label="finger-1"
  Base = -> Box405
  Edges = 2 edges r=8.5: [Edge3,Edge5]
FEATURE [Part::Cut] Cut173011017  label="finger-2"
  Base = -> Chamfer
  Tool = -> Box406007
FEATURE [Part::Fillet] Fillet  label="finger-3"
  Base = -> Cut173011017
  Edges = 2 edges r=1.5: [Edge8,Edge14]
FEATURE [Part::Chamfer] Chamfer033  label="grip-3"
  Base = -> Chamfer030
  Edges = 3 edges r=1: [Edge4,Edge10,Edge15]
FEATURE [Part::MultiFuse] Fusion103077013004017007  label="finger-4"
  Shapes = -> [Chamfer033,Box404,Fillet]
FEATURE [Part::Fillet] Fillet006  label="finger-5"
  Base = -> Fusion103077013004017007
  Edges = 4 edges r=3: [Edge33,Edge41,Edge51,Edge59]
FEATURE [Part::Cut] Cut173011018  label="finger-6"
  Base = -> Fillet006
  Tool = -> Fusion103077010
FEATURE [Part::Chamfer] Chamfer034  label="finger"
  Base = -> Cut173011018
  Edges = 4 edges r=0.7: [Edge81,Edge82,Edge83,Edge84]
FEATURE [Part::Box] Box406008010  label="Cube345"
  AttacherType = Attacher::AttachEngine3D
  Height = 5
  Length = 10
  Placement = pos=(4,5,0.8) rot=(0,0,1;0.785398rad)
  Width = 1
FEATURE [Part::Box] Box406008011  label="Cube346"
  AttacherType = Attacher::AttachEngine3D
  Height = 5
  Length = 10
  Placement = pos=(7.3,5,0.8) rot=(0,0,1;0.785398rad)
  Width = 1
FEATURE [Part::Fuse] Fusion103077013004017008
  Base = -> Box406008010
  Tool = -> Box406008011
FEATURE [Part::Feature] Fusion103077013004017008001
  Placement = pos=(-4.36408,4.36408,2.00532) rot=(0.707107,0.707107,0;0.628319rad)
  shape: bbox 12.71 x 10.04 x 6.004 mm, 12 faces, 2 solids (baked)
FEATURE [Part::Feature] Fusion103077013004017008002
  Placement = pos=(-7.06123,7.06123,7.25532) rot=(0.707107,0.707107,0;1.25664rad)
  shape: bbox 12.81 x 11.79 x 4.715 mm, 12 faces, 2 solids (baked)
FEATURE [Part::Feature] Fusion103077013004017008003
  Placement = pos=(-7.06123,7.06123,13.7447) rot=(0.707107,0.707107,0;1.88496rad)
  shape: bbox 11.79 x 12.81 x 4.715 mm, 12 faces, 2 solids (baked)
FEATURE [Part::Feature] Fusion103077013004017008004
  Placement = pos=(-4.36408,4.36408,18.9947) rot=(0.707107,0.707107,0;2.51327rad)
  shape: bbox 10.04 x 12.71 x 6.004 mm, 12 faces, 2 solids (baked)
FEATURE [Part::Feature] Fusion103077013004017008005
  Placement = pos=(-1e-15,1e-15,21) rot=(0.707107,0.707107,0;3.14159rad)
  shape: bbox 7.778 x 11.08 x 5 mm, 12 faces, 2 solids (baked)
FEATURE [Part::Feature] Fusion103077013004017008006
  Placement = pos=(4.36408,-4.36408,18.9947) rot=(0.707107,0.707107,0;3.76991rad)
  shape: bbox 10.04 x 12.71 x 6.004 mm, 12 faces, 2 solids (baked)
FEATURE [Part::Feature] Fusion103077013004017008007
  Placement = pos=(7.06123,-7.06123,13.7447) rot=(-0.707107,-0.707107,0;1.88496rad)
  shape: bbox 11.79 x 12.81 x 4.715 mm, 12 faces, 2 solids (baked)
FEATURE [Part::Feature] Fusion103077013004017008008
  Placement = pos=(7.06123,-7.06123,7.25532) rot=(-0.707107,-0.707107,0;1.25664rad)
  shape: bbox 12.81 x 11.79 x 4.715 mm, 12 faces, 2 solids (baked)
FEATURE [Part::Feature] Fusion103077013004017008009
  Placement = pos=(4.36408,-4.36408,2.00532) rot=(-0.707107,-0.707107,0;0.628319rad)
  shape: bbox 12.71 x 10.04 x 6.004 mm, 12 faces, 2 solids (baked)
FEATURE [Part::MultiFuse] Fusion103077013004017008010
  Shapes = -> [Fusion103077013004017008001,Fusion103077013004017008003,Fusion103077013004017008007,Fusion103077013004017008005,Fusion103077013004017008009,Fusion103077013004017008008,Fusion103077013004017008004,Fusion103077013004017008002,Fusion103077013004017008,Fusion103077013004017008006]
FEATURE [Part::Cut] Cut173011019  label="Gear with Smaller Teeth 0.2"
  Base = -> Cut173011005
  Tool = -> Fusion103077013004017008010
FEATURE [Part::Box] Box406008012  label="Cube347"
  AttacherType = Attacher::AttachEngine3D
  Height = 10
  Length = 10
  Placement = pos=(12,0.6,0) rot=(0,-1,0;0.698132rad)
  Width = 1
FEATURE [Part::Box] Box406008013  label="Cube348"
  AttacherType = Attacher::AttachEngine3D
  Height = 10
  Length = 10
  Placement = pos=(12,-1.6,0) rot=(0,-1,0;0.698132rad)
  Width = 1
FEATURE [Part::MultiFuse] Fusion103077013004017008011  label="tooth-thin"
  Shapes = -> [Box406008012,Box406008013]
FEATURE [Part::Feature] Fusion103077013004017008011001
  Placement = pos=(0,0,0) rot=(0,0,1;0.314159rad)
  shape: bbox 14.39 x 7.397 x 14.09 mm, 12 faces, 2 solids (baked)
FEATURE [Part::Feature] Fusion103077013004017008011002
  Placement = pos=(0,0,0) rot=(0,0,1;0.628319rad)
  shape: bbox 13.28 x 10.87 x 14.09 mm, 12 faces, 2 solids (baked)
FEATURE [Part::Feature] Fusion103077013004017008011003
  Placement = pos=(0,0,0) rot=(0,0,1;0.942478rad)
  shape: bbox 10.87 x 13.28 x 14.09 mm, 12 faces, 2 solids (baked)
FEATURE [Part::Feature] Fusion103077013004017008011004
  Placement = pos=(0,0,0) rot=(0,0,1;1.25664rad)
  shape: bbox 7.397 x 14.39 x 14.09 mm, 12 faces, 2 solids (baked)
FEATURE [Part::Feature] Fusion103077013004017008011005
  Placement = pos=(0,0,0) rot=(0,0,1;1.5708rad)
  shape: bbox 3.2 x 14.09 x 14.09 mm, 12 faces, 2 solids (baked)
FEATURE [Part::Feature] Fusion103077013004017008011006
  Placement = pos=(0,0,0) rot=(0,0,1;1.88496rad)
  shape: bbox 7.397 x 14.39 x 14.09 mm, 12 faces, 2 solids (baked)
FEATURE [Part::Feature] Fusion103077013004017008011007
  Placement = pos=(0,0,0) rot=(0,0,1;2.19911rad)
  shape: bbox 10.87 x 13.28 x 14.09 mm, 12 faces, 2 solids (baked)
FEATURE [Part::Feature] Fusion103077013004017008011008
  Placement = pos=(0,0,0) rot=(0,0,1;2.51327rad)
  shape: bbox 13.28 x 10.87 x 14.09 mm, 12 faces, 2 solids (baked)
FEATURE [Part::Feature] Fusion103077013004017008011009
  Placement = pos=(0,0,0) rot=(0,0,1;2.82743rad)
  shape: bbox 14.39 x 7.397 x 14.09 mm, 12 faces, 2 solids (baked)
FEATURE [Part::Feature] Fusion103077013004017008011010
  Placement = pos=(0,0,0) rot=(0,0,1;3.14159rad)
  shape: bbox 14.09 x 3.2 x 14.09 mm, 12 faces, 2 solids (baked)
FEATURE [Part::Feature] Fusion103077013004017008011011
  Placement = pos=(0,0,0) rot=(0,0,1;3.45575rad)
  shape: bbox 14.39 x 7.397 x 14.09 mm, 12 faces, 2 solids (baked)
FEATURE [Part::Feature] Fusion103077013004017008011012
  Placement = pos=(0,0,0) rot=(0,0,1;3.76991rad)
  shape: bbox 13.28 x 10.87 x 14.09 mm, 12 faces, 2 solids (baked)
FEATURE [Part::Feature] Fusion103077013004017008011013
  Placement = pos=(0,0,0) rot=(0,0,1;4.08407rad)
  shape: bbox 10.87 x 13.28 x 14.09 mm, 12 faces, 2 solids (baked)
FEATURE [Part::Feature] Fusion103077013004017008011014
  Placement = pos=(0,0,0) rot=(0,0,-1;1.88496rad)
  shape: bbox 7.397 x 14.39 x 14.09 mm, 12 faces, 2 solids (baked)
FEATURE [Part::Feature] Fusion103077013004017008011015
  Placement = pos=(0,0,0) rot=(0,0,-1;1.5708rad)
  shape: bbox 3.2 x 14.09 x 14.09 mm, 12 faces, 2 solids (baked)
FEATURE [Part::Feature] Fusion103077013004017008011016
  Placement = pos=(0,0,0) rot=(0,0,-1;1.25664rad)
  shape: bbox 7.397 x 14.39 x 14.09 mm, 12 faces, 2 solids (baked)
FEATURE [Part::Feature] Fusion103077013004017008011017
  Placement = pos=(0,0,0) rot=(0,0,-1;0.942478rad)
  shape: bbox 10.87 x 13.28 x 14.09 mm, 12 faces, 2 solids (baked)
FEATURE [Part::Feature] Fusion103077013004017008011018
  Placement = pos=(0,0,0) rot=(0,0,-1;0.628319rad)
  shape: bbox 13.28 x 10.87 x 14.09 mm, 12 faces, 2 solids (baked)
FEATURE [Part::Feature] Fusion103077013004017008011019
  Placement = pos=(0,0,0) rot=(0,0,-1;0.314159rad)
  shape: bbox 14.39 x 7.397 x 14.09 mm, 12 faces, 2 solids (baked)
FEATURE [Part::MultiFuse] Fusion103077013004017008011020  label="teeth-thin"
  Shapes = -> [Fusion103077013004017008011,Fusion103077013004017008011015,Fusion103077013004017008011014,Fusion103077013004017008011016,Fusion103077013004017008011017,Fusion103077013004017008011001,Fusion103077013004017008011003,Fusion103077013004017008011005,Fusion103077013004017008011011,Fusion103077013004017008011012,Fusion103077013004017008011013,Fusion103077013004017008011008,Fusion103077013004017008011006,+7 more]
FEATURE [Part::FeaturePython] BevelGear003  # WARN: FeaturePython — macro-defined, semantics opaque (R4)
  Placement = pos=(0,0,2.5) rot=(0,0,1;0rad)
  backlash = 0
  beta = 0
  clearance = 0.1
  height = 3
  m = 1
  numpoints = 6
  pitch_angle = 45
  pressure_angle = 20
  reset_origin = true
  teeth = 20
FEATURE [Part::Cylinder] Cylinder081002
  Angle = 360
  AttacherType = Attacher::AttachEngine3D
  Height = 22
  Radius = 11
FEATURE [Part::MultiCommon] Common006  label="big-gear-a001"
  Shapes = -> [BevelGear003,Cylinder081002]
FEATURE [Part::Cylinder] Cylinder081003  label="shaft-004"
  Angle = 360
  AttacherType = Attacher::AttachEngine3D
  Height = 10
  Placement = pos=(0,0,-2) rot=(0,0,1;0rad)
  Radius = 1.75
FEATURE [Part::Box] Box406008014  label="Cube349"
  AttacherType = Attacher::AttachEngine3D
  Height = 12
  Length = 10
  Placement = pos=(-5,1.125,-2) rot=(0,0,1;0rad)
  Width = 10
FEATURE [Part::Cut] Cut173011020  label="motor-shaft001"
  Base = -> Cylinder081003
  Tool = -> Box406008014
FEATURE [Part::Cut] Cut173011021  label="big-gear-003"
  Base = -> Common006
  Tool = -> Cut173011020
FEATURE [Part::Chamfer] Chamfer035  label="big-gear001"
  Base = -> Cut173011021
  Edges = 3 edges r=0.5: [Edge124,Edge125,Edge126]
FEATURE [Part::Cut] Cut173011022  label="big-gear-with-smaller-teeth"
  Base = -> Chamfer035
  Tool = -> Fusion103077013004017008011020
FEATURE [Part::Cylinder] Cylinder081004  label="Cylinder081003"
  Angle = 360
  AttacherType = Attacher::AttachEngine3D
  Height = 6.5
  Placement = pos=(0,0,4) rot=(0,0,1;0rad)
  Radius = 5
FEATURE [Part::Box] Box406008015  label="Cube350"
  AttacherType = Attacher::AttachEngine3D
  Height = 12
  Length = 10
  Placement = pos=(-5,1.125,0) rot=(0,0,1;0rad)
  Width = 10
FEATURE [Part::Cylinder] Cylinder081005  label="shaft-005"
  Angle = 360
  AttacherType = Attacher::AttachEngine3D
  Height = 10
  Placement = pos=(0,0,1) rot=(0,0,1;0rad)
  Radius = 1.75
FEATURE [Part::Cut] Cut173011023
  Base = -> Cylinder081005
  Tool = -> Box406008015
FEATURE [Part::Fuse] Fusion103077013004017008011021
  Base = -> Cut173011022
  Tool = -> Cylinder081004
FEATURE [Part::Cut] Cut173011024  label="Big Gear with Smaller Teeth and Boss"
  Base = -> Fusion103077013004017008011021
  Tool = -> Cut173011023
FEATURE [Part::Chamfer] Chamfer036
  Base = -> Cut173011024
  Edges = 3 edges r=0.5: [Edge205,Edge206,Edge207]
FEATURE [Part::Chamfer] Chamfer037  label="Big Gear with Smaller Teeth and Boss 0.3"
  Base = -> Chamfer036
  Edges = 3 edges r=0.5: [Edge222,Edge224,Edge225]
  Placement = pos=(-1e-15,1e-15,21) rot=(0.707107,0.707107,0;3.14159rad)
FEATURE [Part::Fuse] Fusion103077013004017008011022
  Base = -> Box406019
  Tool = -> Box406008002
FEATURE [Part::Box] Box406008016  label="Cube351"
  AttacherType = Attacher::AttachEngine3D
  Height = 10
  Length = 17
  Placement = pos=(1.9,-9.6,-1) rot=(0,0,1;0.785398rad)
  Width = 16
FEATURE [Part::Box] Box406008017  label="gearbox006"
  AttacherType = Attacher::AttachEngine3D
  Height = 9
  Length = 12.5
  Placement = pos=(8.125,-0.625,21) rot=(0,0,1;2.35619rad)
  Width = 10.5
FEATURE [Part::Cut] Cut173011025
  Base = -> Fusion103077013004016
  Tool = -> Fusion103077013004013
FEATURE [Part::Cut] Cut173011026
  Base = -> Cut173011025
  Tool = -> Fusion103077013004017008011022
FEATURE [Part::Cut] Cut173011027
  Base = -> Cut173011026
  Tool = -> Common004
FEATURE [Part::Cut] Cut173011028
  Base = -> Cut173011027
  Tool = -> Box406008017
FEATURE [Part::Cut] Cut173011029
  Base = -> Cut173011028
  Tool = -> Box406016
FEATURE [Part::Cylinder] Cylinder081006
  Angle = 360
  AttacherType = Attacher::AttachEngine3D
  Height = 12
  Placement = pos=(0,0,40) rot=(0.281085,0.678598,0.678598;2.59356rad)
  Radius = 1.2
FEATURE [Part::Cylinder] Cylinder081007
  Angle = 360
  AttacherType = Attacher::AttachEngine3D
  Height = 12
  Placement = pos=(8.48528,8.48528,40) rot=(0.281085,0.678598,0.678598;2.59356rad)
  Radius = 2.2
FEATURE [Part::MultiFuse] Fusion103077013004017008011023  label="M2-screw002"
  Placement = pos=(-2,14,0) rot=(0,0,1;3.14159rad)
  Shapes = -> [Cylinder081006,Cylinder081007]
FEATURE [Part::Box] Box406008018  label="Cube352"
  AttacherType = Attacher::AttachEngine3D
  Height = 10.35
  Length = 3.68
  Placement = pos=(13.02,-11.61,32.65) rot=(0,0,1;0.785398rad)
  Width = 10
FEATURE [Part::Chamfer] Chamfer038
  Base = -> Box406008018
  Edges = 1 edges r=9: [Edge9]
FEATURE [Part::Cut] Cut173011030
  Base = -> Chamfer038
  Tool = -> Fusion103077013
FEATURE [Part::Box] Box406008019  label="Cube353"
  AttacherType = Attacher::AttachEngine3D
  Height = 10
  Length = 10
  Placement = pos=(17,-17,35) rot=(0,0,1;0.785398rad)
  Width = 10
FEATURE [Part::Cut] Cut173011031
  Base = -> Cut173011030
  Tool = -> Box406008019
FEATURE [Part::Box] Box406008020  label="Cube354"
  AttacherType = Attacher::AttachEngine3D
  Height = 10
  Length = 10
  Placement = pos=(-13.7,20.31,35) rot=(0,0,1;3.92699rad)
  Width = 10
FEATURE [Part::Box] Box406008021  label="Cube355"
  AttacherType = Attacher::AttachEngine3D
  Height = 10.35
  Length = 3.68
  Placement = pos=(-9.01,15.62,32.65) rot=(0,0,1;3.92699rad)
  Width = 10
FEATURE [Part::Chamfer] Chamfer039
  Base = -> Box406008021
  Edges = 1 edges r=9: [Edge9]
FEATURE [Part::Cut] Cut173011032
  Base = -> Chamfer039
  Tool = -> Box406008020
FEATURE [Part::Cut] Cut173011033
  Base = -> Cut173011032
  Tool = -> Fusion103077013004017008011023
FEATURE [Part::MultiFuse] Fusion103077013004017008011024
  Shapes = -> [Cut173011029,Cut173011031,Cut173011033]
FEATURE [Part::Fillet] Fillet007
  Base = -> Fusion103077013004017008011024
  Edges = 2 edges r=1: [Edge110,Edge115]
FEATURE [Part::Box] Box406008022  label="Cube356"
  AttacherType = Attacher::AttachEngine3D
  Height = 50
  Length = 50
  Placement = pos=(-21,-50,0) rot=(0,0,1;0.785398rad)
  Width = 50
FEATURE [Part::Cylinder] Cylinder081008  label="big-gear-clearance001"
  Angle = 360
  AttacherType = Attacher::AttachEngine3D
  Height = 22
  Radius = 12
FEATURE [Part::Box] Box406008023  label="Cube357"
  AttacherType = Attacher::AttachEngine3D
  Height = 6
  Length = 15
  Placement = pos=(-5,10,2) rot=(0,0,1;0rad)
  Width = 10
FEATURE [Part::Cut] Cut173011034  label="screw-land-002"
  Base = -> Box406008023
  Placement = pos=(0,0,0) rot=(0,0,1;0.785398rad)
  Tool = -> Cylinder081008
FEATURE [Part::Mirroring] Part__Mirroring  label="screw-land-002 (Mirror #1)"
  Base = (0,0,0)
  Normal = (1,0,0)
  Placement = pos=(0,0,0) rot=(0,0,1;5.49779rad)
  Source = -> Cut173011034
FEATURE [Part::Cylinder] Cylinder081009  label="M3-cap-screw-head002"
  Angle = 360
  AttacherType = Attacher::AttachEngine3D
  Height = 10
  Placement = pos=(0,15,4) rot=(0,0,1;0rad)
  Radius = 3
FEATURE [Part::Cylinder] Cylinder081010  label="M3-cap-screw-head003"
  Angle = 360
  AttacherType = Attacher::AttachEngine3D
  Height = 10
  Placement = pos=(0,15,-6) rot=(0,0,1;0rad)
  Radius = 1.7
FEATURE [Part::MultiFuse] Fusion103077013004017008011025  label="M3-cap-screw001"
  Placement = pos=(0,0,5) rot=(0,0,1;0.785398rad)
  Shapes = -> [Cylinder081010,Cylinder081009]
FEATURE [Part::Mirroring] Part__Mirroring001  label="M3-cap-screw001 (Mirror #2)"
  Base = (0,0,0)
  Normal = (1,0,0)
  Placement = pos=(0,0,0) rot=(0,0,1;5.49779rad)
  Source = -> Fusion103077013004017008011025
FEATURE [Part::MultiFuse] Fusion103077013004017008011026
  Shapes = -> [Part__Mirroring,Cut173011007]
FEATURE [Part::MultiFuse] Fusion103077013004017008011027
  Shapes = -> [Part__Mirroring001,Fusion103077013004011,Box406008016]
FEATURE [Part::Cut] Cut173011035
  Base = -> Fusion103077013004017008011026
  Tool = -> Fusion103077013004017008011027
FEATURE [Part::Fillet] Fillet008
  Base = -> Cut173011035
  Edges = 2 edges r=3: [Edge4,Edge50]
FEATURE [Part::Feature] Shape
  Placement = pos=(-3.57,12.43,40) rot=(0,0.816497,-0.57735;4.18879rad)
  shape: bbox 5.276 x 5.276 x 4.461 mm, 8 faces (baked)
FEATURE [Drawing::FeatureViewAnnotation] Annotation010
  Font = Sans
  Rotation = 0
  Scale = 7
  ViewResult = <g transform="translate(10,10) rotate(0)">\n<text id="Annotation010"\n font-family="Sans"\n font-size="7"\n fill="#000000">\n<tspan x="0" dy="1em"></tspan>\n</text>\n</g>
  Visible = true
  X = 10
  Y = 10
FEATURE [Drawing::FeaturePage] Page
  EditableTexts = AUTHOR NAME | CREATION DATE | SUPERVISOR NAME | CHECK DATE | SCALE | WEIGHT | NUMBER | SHEET | TITLE | SUBTITLE
  Group = -> [Annotation,Annotation001,Annotation002,Annotation004,Annotation007,Annotation008,Annotation010]
  Template = <path>
FEATURE [Drawing::FeatureViewAnnotation] Annotation011
  Font = Sans
  Rotation = 0
  Scale = 5
  Text = Rotated Slots and amended screw clamp position and added nut recess. Cut in half. Made slots in the screw lands so the gear can freely rotate.
  ViewResult = <g transform="translate(10,60) rotate(0)">\n<text id="Annotation011"\n font-family="Sans"\n font-size="5"\n fill="#000000">\n<tspan x="0" dy="1em">Rotated Slots and amended screw clamp position and added nut recess. Cut in half. Made slots in the screw lands so the gear can freely rotate.</tspan>\n<tspan x="0" dy="1em"></tspan>\n</text>\n</g>
  Visible = true
  X = 10
  Y = 60
FEATURE [Drawing::FeaturePage] Page001
  EditableTexts = AUTHOR NAME | CREATION DATE | SUPERVISOR NAME | CHECK DATE | SCALE | WEIGHT | NUMBER | SHEET | TITLE | SUBTITLE
  Group = -> [Annotation003,Annotation005,Annotation006,Annotation009,Annotation011]
  Template = <path>
FEATURE [Part::Fillet] Fillet009
  Base = -> Fillet008
  Edges = 2 edges r=3: [Edge3,Edge42]
FEATURE [Part::MultiFuse] Fusion103077013004017008011028
  Shapes = -> [Fillet009,Fillet007]
FEATURE [Part::Cut] Cut173011036
  Base = -> Fusion103077013004017008011028
  Tool = -> Box406008022
FEATURE [Part::Cut] Cut173011037
  Base = -> Cut173011036
  Tool = -> Shape
FEATURE [Part::Cut] Cut173011038
  Base = -> Cut173011037
  Tool = -> Cylinder059
note: 2 file-system paths scrubbed to <path> (originals preserved in the JSON sidecar)
